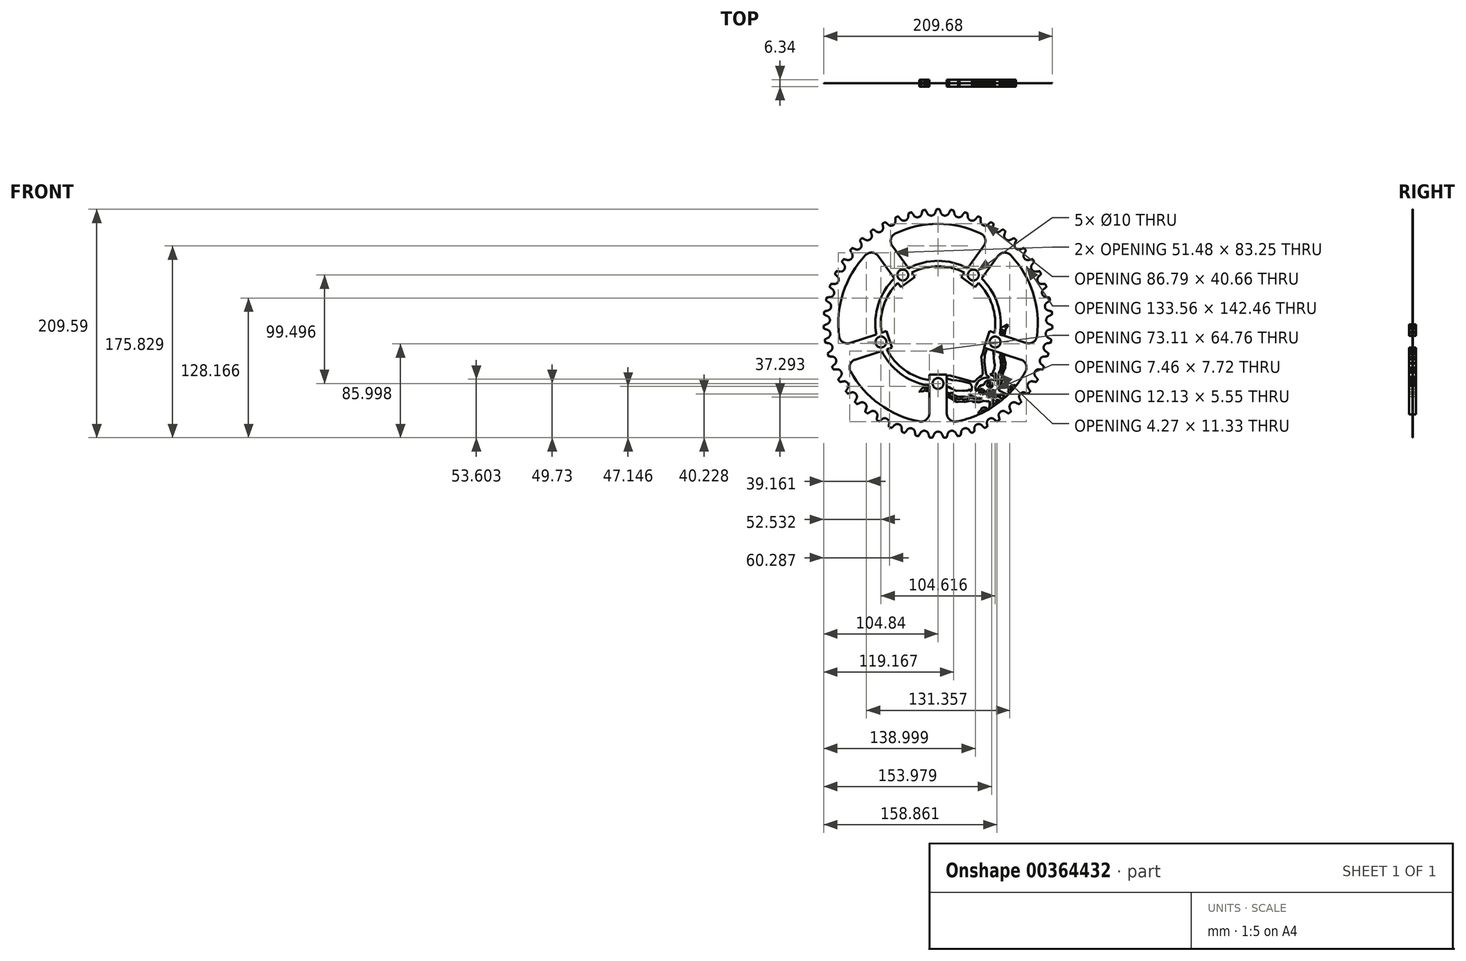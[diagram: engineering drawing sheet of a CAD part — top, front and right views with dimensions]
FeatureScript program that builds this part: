
annotation { "Feature Type Name" : "Feature", "Feature Type Description" : "" }
export const myFeature = defineFeature(function(context is Context, id is Id, definition is map)
    precondition{}
    {
        {
            var Q0;
            Q0=qCreatedBy(makeId("Front.planeOp"),FACE);
            var sketch = newSketch(context, id + "F0", { "sketchPlane" : qUnion([Q0])});
            skLineSegment(sketch, "E0", {"start": v(0, 0) * mm, "end": v(-6.35, 102.95) * mm, "construction": true});
            skLineSegment(sketch, "E1", {"start": v(0, 0) * mm, "end": v(6.35, 102.95) * mm, "construction": true});
            skArc(sketch, "E2", {"start": v(-6.1, 99) * mm, "mid": v(-3.93, 99.81) * mm, "end": v(-2.58, 101.71) * mm, "construction": true});
            skArc(sketch, "E3", {"start": v(-1.4, 104.85) * mm, "mid": v(-2, 103.3) * mm, "end": v(-2.55, 101.74) * mm});
            skLineSegment(sketch, "E4", {"start": v(-6.35, 102.95) * mm, "end": v(-2.58, 101.71) * mm, "construction": true});
            skCircle(sketch, "E5", {"center": v(0, 0) * mm, "radius": 103.19 * mm, "construction": true});
            skArc(sketch, "E6", {"start": v(1.4, 104.85) * mm, "mid": v(0, 104.86) * mm, "end": v(-1.4, 104.85) * mm});
            skLineSegment(sketch, "E7", {"start": v(0, 0) * mm, "end": v(0, 116.9) * mm, "construction": true});
            skArc(sketch, "E8", {"start": v(-6.1, 99) * mm, "mid": v(-3.9, 99.82) * mm, "end": v(-2.55, 101.74) * mm});
            skArc(sketch, "E9", {"start": v(2.58, 101.71) * mm, "mid": v(3.93, 99.81) * mm, "end": v(6.1, 99) * mm, "construction": true});
            skArc(sketch, "E10", {"start": v(2.55, 101.74) * mm, "mid": v(3.9, 99.82) * mm, "end": v(6.1, 99) * mm});
            skArc(sketch, "E11", {"start": v(2.56, 101.7) * mm, "mid": v(2, 103.29) * mm, "end": v(1.4, 104.85) * mm});
            skLineSegment(sketch, "E12", {"start": v(6.35, 102.95) * mm, "end": v(2.56, 101.7) * mm, "construction": true});
            skArc(sketch, "E13.1.0", {"start": v(-18.22, 97.5) * mm, "mid": v(-16.14, 98.58) * mm, "end": v(-15.03, 100.65) * mm});
            skArc(sketch, "E13.1.1", {"start": v(-14.27, 103.88) * mm, "mid": v(-14.68, 102.27) * mm, "end": v(-15.03, 100.65) * mm});
            skArc(sketch, "E13.1.2", {"start": v(-11.5, 104.22) * mm, "mid": v(-12.89, 104.06) * mm, "end": v(-14.27, 103.88) * mm});
            skArc(sketch, "E13.1.3", {"start": v(-9.96, 101.25) * mm, "mid": v(-10.7, 102.75) * mm, "end": v(-11.5, 104.22) * mm});
            skArc(sketch, "E13.1.4", {"start": v(-9.98, 101.28) * mm, "mid": v(-8.4, 99.54) * mm, "end": v(-6.1, 99) * mm});
            skArc(sketch, "E13.2.0", {"start": v(-30.07, 94.51) * mm, "mid": v(-28.13, 95.85) * mm, "end": v(-27.28, 98.04) * mm});
            skArc(sketch, "E13.2.1", {"start": v(-26.93, 101.34) * mm, "mid": v(-27.14, 99.7) * mm, "end": v(-27.28, 98.04) * mm});
            skArc(sketch, "E13.2.2", {"start": v(-24.22, 102.02) * mm, "mid": v(-25.58, 101.69) * mm, "end": v(-26.93, 101.34) * mm});
            skArc(sketch, "E13.2.3", {"start": v(-22.33, 99.26) * mm, "mid": v(-23.25, 100.66) * mm, "end": v(-24.22, 102.02) * mm});
            skArc(sketch, "E13.2.4", {"start": v(-22.35, 99.29) * mm, "mid": v(-20.56, 97.76) * mm, "end": v(-18.22, 97.5) * mm});
            skArc(sketch, "E13.3.0", {"start": v(-41.45, 90.1) * mm, "mid": v(-39.7, 91.67) * mm, "end": v(-39.13, 93.95) * mm});
            skArc(sketch, "E13.3.1", {"start": v(-39.18, 97.26) * mm, "mid": v(-39.18, 95.6) * mm, "end": v(-39.13, 93.95) * mm});
            skArc(sketch, "E13.3.2", {"start": v(-36.57, 98.27) * mm, "mid": v(-37.88, 97.78) * mm, "end": v(-39.18, 97.26) * mm});
            skArc(sketch, "E13.3.3", {"start": v(-34.36, 95.76) * mm, "mid": v(-35.44, 97.04) * mm, "end": v(-36.57, 98.27) * mm});
            skArc(sketch, "E13.3.4", {"start": v(-34.38, 95.79) * mm, "mid": v(-32.42, 94.49) * mm, "end": v(-30.07, 94.51) * mm});
            skArc(sketch, "E13.4.0", {"start": v(-52.21, 84.33) * mm, "mid": v(-50.66, 86.1) * mm, "end": v(-50.37, 88.43) * mm});
            skArc(sketch, "E13.4.1", {"start": v(-50.83, 91.71) * mm, "mid": v(-50.63, 90.06) * mm, "end": v(-50.37, 88.43) * mm});
            skArc(sketch, "E13.4.2", {"start": v(-48.37, 93.03) * mm, "mid": v(-49.6, 92.38) * mm, "end": v(-50.83, 91.71) * mm});
            skArc(sketch, "E13.4.3", {"start": v(-45.86, 90.81) * mm, "mid": v(-47.1, 91.94) * mm, "end": v(-48.37, 93.03) * mm});
            skArc(sketch, "E13.4.4", {"start": v(-45.89, 90.84) * mm, "mid": v(-43.78, 89.79) * mm, "end": v(-41.45, 90.1) * mm});
            skArc(sketch, "E13.5.0", {"start": v(-62.18, 77.27) * mm, "mid": v(-60.86, 79.22) * mm, "end": v(-60.86, 81.57) * mm});
            skArc(sketch, "E13.5.1", {"start": v(-61.72, 84.77) * mm, "mid": v(-61.32, 83.16) * mm, "end": v(-60.86, 81.57) * mm});
            skArc(sketch, "E13.5.2", {"start": v(-59.44, 86.38) * mm, "mid": v(-60.58, 85.58) * mm, "end": v(-61.72, 84.77) * mm});
            skArc(sketch, "E13.5.3", {"start": v(-56.68, 84.49) * mm, "mid": v(-58.04, 85.46) * mm, "end": v(-59.44, 86.38) * mm});
            skArc(sketch, "E13.5.4", {"start": v(-56.7, 84.5) * mm, "mid": v(-54.49, 83.73) * mm, "end": v(-52.21, 84.33) * mm});
            skArc(sketch, "E13.6.0", {"start": v(-71.2, 69.04) * mm, "mid": v(-70.13, 71.14) * mm, "end": v(-70.42, 73.47) * mm});
            skArc(sketch, "E13.6.1", {"start": v(-71.67, 76.54) * mm, "mid": v(-71.07, 75) * mm, "end": v(-70.42, 73.47) * mm});
            skArc(sketch, "E13.6.2", {"start": v(-69.6, 78.42) * mm, "mid": v(-70.64, 77.49) * mm, "end": v(-71.67, 76.54) * mm});
            skArc(sketch, "E13.6.3", {"start": v(-66.63, 76.88) * mm, "mid": v(-68.1, 77.68) * mm, "end": v(-69.6, 78.42) * mm});
            skArc(sketch, "E13.6.4", {"start": v(-66.66, 76.9) * mm, "mid": v(-64.36, 76.4) * mm, "end": v(-62.18, 77.27) * mm});
            skArc(sketch, "E13.7.0", {"start": v(-79.15, 59.77) * mm, "mid": v(-78.34, 61.98) * mm, "end": v(-78.92, 64.26) * mm});
            skArc(sketch, "E13.7.1", {"start": v(-80.53, 67.15) * mm, "mid": v(-79.75, 65.7) * mm, "end": v(-78.92, 64.26) * mm});
            skArc(sketch, "E13.7.2", {"start": v(-78.71, 69.28) * mm, "mid": v(-79.63, 68.22) * mm, "end": v(-80.53, 67.15) * mm});
            skArc(sketch, "E13.7.3", {"start": v(-75.57, 68.11) * mm, "mid": v(-77.13, 68.72) * mm, "end": v(-78.71, 69.28) * mm});
            skArc(sketch, "E13.7.4", {"start": v(-75.6, 68.13) * mm, "mid": v(-73.26, 67.9) * mm, "end": v(-71.2, 69.04) * mm});
            skArc(sketch, "E13.8.0", {"start": v(-85.9, 49.6) * mm, "mid": v(-85.37, 51.88) * mm, "end": v(-86.21, 54.07) * mm});
            skArc(sketch, "E13.8.1", {"start": v(-88.17, 56.75) * mm, "mid": v(-87.22, 55.4) * mm, "end": v(-86.21, 54.07) * mm});
            skArc(sketch, "E13.8.2", {"start": v(-86.63, 59.08) * mm, "mid": v(-87.4, 57.92) * mm, "end": v(-88.17, 56.75) * mm});
            skArc(sketch, "E13.8.3", {"start": v(-83.37, 58.3) * mm, "mid": v(-85, 58.72) * mm, "end": v(-86.63, 59.08) * mm});
            skArc(sketch, "E13.8.4", {"start": v(-83.4, 58.32) * mm, "mid": v(-81.05, 58.4) * mm, "end": v(-79.15, 59.77) * mm});
            skArc(sketch, "E13.9.0", {"start": v(-91.34, 38.66) * mm, "mid": v(-91.1, 41) * mm, "end": v(-92.2, 43.07) * mm});
            skArc(sketch, "E13.9.1", {"start": v(-94.48, 45.48) * mm, "mid": v(-93.36, 44.26) * mm, "end": v(-92.2, 43.07) * mm});
            skArc(sketch, "E13.9.2", {"start": v(-93.23, 47.99) * mm, "mid": v(-93.86, 46.74) * mm, "end": v(-94.48, 45.48) * mm});
            skArc(sketch, "E13.9.3", {"start": v(-89.9, 47.62) * mm, "mid": v(-91.56, 47.83) * mm, "end": v(-93.23, 47.99) * mm});
            skArc(sketch, "E13.9.4", {"start": v(-89.94, 47.63) * mm, "mid": v(-87.61, 47.99) * mm, "end": v(-85.9, 49.6) * mm});
            skArc(sketch, "E13.10.0", {"start": v(-95.4, 27.14) * mm, "mid": v(-95.44, 29.5) * mm, "end": v(-96.8, 31.41) * mm});
            skArc(sketch, "E13.10.1", {"start": v(-99.35, 33.53) * mm, "mid": v(-98.1, 32.45) * mm, "end": v(-96.8, 31.41) * mm});
            skArc(sketch, "E13.10.2", {"start": v(-98.42, 36.16) * mm, "mid": v(-98.9, 34.85) * mm, "end": v(-99.35, 33.53) * mm});
            skArc(sketch, "E13.10.3", {"start": v(-95.07, 36.21) * mm, "mid": v(-96.75, 36.22) * mm, "end": v(-98.42, 36.16) * mm});
            skArc(sketch, "E13.10.4", {"start": v(-95.1, 36.21) * mm, "mid": v(-92.85, 36.86) * mm, "end": v(-91.34, 38.66) * mm});
            skArc(sketch, "E13.11.0", {"start": v(-98, 15.21) * mm, "mid": v(-98.34, 17.54) * mm, "end": v(-99.93, 19.28) * mm});
            skArc(sketch, "E13.11.1", {"start": v(-102.72, 21.07) * mm, "mid": v(-101.34, 20.15) * mm, "end": v(-99.93, 19.28) * mm});
            skArc(sketch, "E13.11.2", {"start": v(-102.12, 23.8) * mm, "mid": v(-102.43, 22.43) * mm, "end": v(-102.72, 21.07) * mm});
            skArc(sketch, "E13.11.3", {"start": v(-98.8, 24.26) * mm, "mid": v(-100.47, 24.05) * mm, "end": v(-102.12, 23.8) * mm});
            skArc(sketch, "E13.11.4", {"start": v(-98.84, 24.25) * mm, "mid": v(-96.67, 25.17) * mm, "end": v(-95.4, 27.14) * mm});
            skArc(sketch, "E13.12.0", {"start": v(-99.13, 3.05) * mm, "mid": v(-99.75, 5.32) * mm, "end": v(-101.54, 6.85) * mm});
            skArc(sketch, "E13.12.1", {"start": v(-104.53, 8.28) * mm, "mid": v(-103.05, 7.54) * mm, "end": v(-101.54, 6.85) * mm});
            skArc(sketch, "E13.12.2", {"start": v(-104.27, 11.07) * mm, "mid": v(-104.4, 9.67) * mm, "end": v(-104.53, 8.28) * mm});
            skArc(sketch, "E13.12.3", {"start": v(-101.03, 11.93) * mm, "mid": v(-102.66, 11.53) * mm, "end": v(-104.27, 11.07) * mm});
            skArc(sketch, "E13.12.4", {"start": v(-101.07, 11.92) * mm, "mid": v(-99.03, 13.1) * mm, "end": v(-98, 15.21) * mm});
            skArc(sketch, "E13.13.0", {"start": v(-98.76, -9.15) * mm, "mid": v(-99.65, -6.98) * mm, "end": v(-101.61, -5.68) * mm});
            skArc(sketch, "E13.13.1", {"start": v(-104.75, -4.63) * mm, "mid": v(-103.2, -5.18) * mm, "end": v(-101.61, -5.68) * mm});
            skArc(sketch, "E13.13.2", {"start": v(-104.84, -1.83) * mm, "mid": v(-104.8, -3.23) * mm, "end": v(-104.75, -4.63) * mm});
            skArc(sketch, "E13.13.3", {"start": v(-101.74, -0.58) * mm, "mid": v(-103.3, -1.18) * mm, "end": v(-104.84, -1.83) * mm});
            skArc(sketch, "E13.13.4", {"start": v(-101.77, -0.59) * mm, "mid": v(-99.9, 0.83) * mm, "end": v(-99.13, 3.05) * mm});
            skArc(sketch, "E13.14.0", {"start": v(-96.88, -21.22) * mm, "mid": v(-98.04, -19.17) * mm, "end": v(-100.14, -18.12) * mm});
            skArc(sketch, "E13.14.1", {"start": v(-103.4, -17.46) * mm, "mid": v(-101.77, -17.82) * mm, "end": v(-100.14, -18.12) * mm});
            skArc(sketch, "E13.14.2", {"start": v(-103.82, -14.7) * mm, "mid": v(-103.62, -16.08) * mm, "end": v(-103.4, -17.46) * mm});
            skArc(sketch, "E13.14.3", {"start": v(-100.9, -13.07) * mm, "mid": v(-102.37, -13.86) * mm, "end": v(-103.82, -14.7) * mm});
            skArc(sketch, "E13.14.4", {"start": v(-100.92, -13.09) * mm, "mid": v(-99.24, -11.45) * mm, "end": v(-98.76, -9.15) * mm});
            skArc(sketch, "E13.15.0", {"start": v(-93.54, -32.96) * mm, "mid": v(-94.94, -31.07) * mm, "end": v(-97.16, -30.3) * mm});
            skArc(sketch, "E13.15.1", {"start": v(-100.46, -30.04) * mm, "mid": v(-98.81, -30.2) * mm, "end": v(-97.16, -30.3) * mm});
            skArc(sketch, "E13.15.2", {"start": v(-101.23, -27.35) * mm, "mid": v(-100.85, -28.7) * mm, "end": v(-100.46, -30.04) * mm});
            skArc(sketch, "E13.15.3", {"start": v(-98.52, -25.37) * mm, "mid": v(-99.9, -26.34) * mm, "end": v(-101.23, -27.35) * mm});
            skArc(sketch, "E13.15.4", {"start": v(-98.55, -25.4) * mm, "mid": v(-97.08, -23.56) * mm, "end": v(-96.88, -21.22) * mm});
            skArc(sketch, "E13.16.0", {"start": v(-88.78, -44.2) * mm, "mid": v(-90.4, -42.5) * mm, "end": v(-92.7, -42) * mm});
            skArc(sketch, "E13.16.1", {"start": v(-96, -42.15) * mm, "mid": v(-94.35, -42.1) * mm, "end": v(-92.7, -42) * mm});
            skArc(sketch, "E13.16.2", {"start": v(-97.1, -39.58) * mm, "mid": v(-96.56, -40.87) * mm, "end": v(-96, -42.15) * mm});
            skArc(sketch, "E13.16.3", {"start": v(-94.66, -37.29) * mm, "mid": v(-95.9, -38.41) * mm, "end": v(-97.1, -39.58) * mm});
            skArc(sketch, "E13.16.4", {"start": v(-94.68, -37.31) * mm, "mid": v(-93.45, -35.31) * mm, "end": v(-93.54, -32.96) * mm});
            skArc(sketch, "E13.17.0", {"start": v(-82.68, -54.78) * mm, "mid": v(-84.5, -53.3) * mm, "end": v(-86.83, -53.07) * mm});
            skArc(sketch, "E13.17.1", {"start": v(-90.1, -53.63) * mm, "mid": v(-88.46, -53.38) * mm, "end": v(-86.83, -53.07) * mm});
            skArc(sketch, "E13.17.2", {"start": v(-91.5, -51.21) * mm, "mid": v(-90.8, -52.43) * mm, "end": v(-90.1, -53.63) * mm});
            skArc(sketch, "E13.17.3", {"start": v(-89.36, -48.64) * mm, "mid": v(-90.45, -49.9) * mm, "end": v(-91.5, -51.21) * mm});
            skArc(sketch, "E13.17.4", {"start": v(-89.38, -48.66) * mm, "mid": v(-88.4, -46.53) * mm, "end": v(-88.78, -44.2) * mm});
            skArc(sketch, "E13.18.0", {"start": v(-75.32, -64.53) * mm, "mid": v(-77.3, -63.27) * mm, "end": v(-79.65, -63.34) * mm});
            skArc(sketch, "E13.18.1", {"start": v(-82.83, -64.3) * mm, "mid": v(-81.23, -63.85) * mm, "end": v(-79.65, -63.34) * mm});
            skArc(sketch, "E13.18.2", {"start": v(-84.51, -62.07) * mm, "mid": v(-83.68, -63.2) * mm, "end": v(-82.83, -64.3) * mm});
            skArc(sketch, "E13.18.3", {"start": v(-82.7, -59.25) * mm, "mid": v(-83.63, -60.64) * mm, "end": v(-84.51, -62.07) * mm});
            skArc(sketch, "E13.18.4", {"start": v(-82.72, -59.28) * mm, "mid": v(-82.01, -57.04) * mm, "end": v(-82.68, -54.78) * mm});
            skArc(sketch, "E13.19.0", {"start": v(-66.82, -73.3) * mm, "mid": v(-68.94, -72.3) * mm, "end": v(-71.27, -72.65) * mm});
            skArc(sketch, "E13.19.1", {"start": v(-74.3, -74) * mm, "mid": v(-72.77, -73.35) * mm, "end": v(-71.27, -72.65) * mm});
            skArc(sketch, "E13.19.2", {"start": v(-76.24, -71.98) * mm, "mid": v(-75.28, -73) * mm, "end": v(-74.3, -74) * mm});
            skArc(sketch, "E13.19.3", {"start": v(-74.8, -68.96) * mm, "mid": v(-75.55, -70.46) * mm, "end": v(-76.24, -71.98) * mm});
            skArc(sketch, "E13.19.4", {"start": v(-74.81, -69) * mm, "mid": v(-74.38, -66.68) * mm, "end": v(-75.32, -64.53) * mm});
            skArc(sketch, "E13.20.0", {"start": v(-57.3, -80.95) * mm, "mid": v(-59.54, -80.22) * mm, "end": v(-61.8, -80.86) * mm});
            skArc(sketch, "E13.20.1", {"start": v(-64.64, -82.56) * mm, "mid": v(-63.2, -81.73) * mm, "end": v(-61.8, -80.86) * mm});
            skArc(sketch, "E13.20.2", {"start": v(-66.82, -80.8) * mm, "mid": v(-65.74, -81.7) * mm, "end": v(-64.64, -82.56) * mm});
            skArc(sketch, "E13.20.3", {"start": v(-65.75, -77.63) * mm, "mid": v(-66.31, -79.21) * mm, "end": v(-66.82, -80.8) * mm});
            skArc(sketch, "E13.20.4", {"start": v(-65.76, -77.66) * mm, "mid": v(-65.62, -75.32) * mm, "end": v(-66.82, -73.3) * mm});
            skArc(sketch, "E13.21.0", {"start": v(-46.92, -87.38) * mm, "mid": v(-49.23, -86.92) * mm, "end": v(-51.4, -87.84) * mm});
            skArc(sketch, "E13.21.1", {"start": v(-54, -89.88) * mm, "mid": v(-52.68, -88.88) * mm, "end": v(-51.4, -87.84) * mm});
            skArc(sketch, "E13.21.2", {"start": v(-56.38, -88.4) * mm, "mid": v(-55.2, -89.15) * mm, "end": v(-54, -89.88) * mm});
            skArc(sketch, "E13.21.3", {"start": v(-55.71, -85.12) * mm, "mid": v(-56.08, -86.76) * mm, "end": v(-56.38, -88.4) * mm});
            skArc(sketch, "E13.21.4", {"start": v(-55.72, -85.16) * mm, "mid": v(-55.87, -82.81) * mm, "end": v(-57.3, -80.95) * mm});
            skArc(sketch, "E13.22.0", {"start": v(-35.83, -92.48) * mm, "mid": v(-38.17, -92.31) * mm, "end": v(-40.2, -93.49) * mm});
            skArc(sketch, "E13.22.1", {"start": v(-42.55, -95.83) * mm, "mid": v(-41.36, -94.68) * mm, "end": v(-40.2, -93.49) * mm});
            skArc(sketch, "E13.22.2", {"start": v(-45.1, -94.67) * mm, "mid": v(-43.83, -95.26) * mm, "end": v(-42.55, -95.83) * mm});
            skArc(sketch, "E13.22.3", {"start": v(-44.83, -91.33) * mm, "mid": v(-45, -93) * mm, "end": v(-45.1, -94.67) * mm});
            skArc(sketch, "E13.22.4", {"start": v(-44.84, -91.36) * mm, "mid": v(-45.27, -89.05) * mm, "end": v(-46.92, -87.38) * mm});
            skArc(sketch, "E13.23.0", {"start": v(-24.2, -96.19) * mm, "mid": v(-26.54, -96.3) * mm, "end": v(-28.42, -97.72) * mm});
            skArc(sketch, "E13.23.1", {"start": v(-30.45, -100.34) * mm, "mid": v(-29.41, -99.05) * mm, "end": v(-28.42, -97.72) * mm});
            skArc(sketch, "E13.23.2", {"start": v(-33.12, -99.49) * mm, "mid": v(-31.79, -99.92) * mm, "end": v(-30.45, -100.34) * mm});
            skArc(sketch, "E13.23.3", {"start": v(-33.27, -96.14) * mm, "mid": v(-33.22, -97.82) * mm, "end": v(-33.12, -99.49) * mm});
            skArc(sketch, "E13.23.4", {"start": v(-33.27, -96.18) * mm, "mid": v(-33.98, -93.94) * mm, "end": v(-35.83, -92.48) * mm});
            skArc(sketch, "E13.24.0", {"start": v(-12.19, -98.43) * mm, "mid": v(-14.5, -98.84) * mm, "end": v(-16.2, -100.47) * mm});
            skArc(sketch, "E13.24.1", {"start": v(-17.9, -103.32) * mm, "mid": v(-17.02, -101.91) * mm, "end": v(-16.2, -100.47) * mm});
            skArc(sketch, "E13.24.2", {"start": v(-20.64, -102.8) * mm, "mid": v(-19.27, -103.07) * mm, "end": v(-17.9, -103.32) * mm});
            skArc(sketch, "E13.24.3", {"start": v(-21.2, -99.5) * mm, "mid": v(-20.95, -101.16) * mm, "end": v(-20.64, -102.8) * mm});
            skArc(sketch, "E13.24.4", {"start": v(-21.2, -99.54) * mm, "mid": v(-22.18, -97.4) * mm, "end": v(-24.2, -96.19) * mm});
            skArc(sketch, "E13.25.0", {"start": v(0, -99.18) * mm, "mid": v(-2.25, -99.87) * mm, "end": v(-3.72, -101.7) * mm});
            skArc(sketch, "E13.25.1", {"start": v(-5.06, -104.73) * mm, "mid": v(-4.36, -103.23) * mm, "end": v(-3.72, -101.7) * mm});
            skArc(sketch, "E13.25.2", {"start": v(-7.85, -104.56) * mm, "mid": v(-6.46, -104.66) * mm, "end": v(-5.06, -104.73) * mm});
            skArc(sketch, "E13.25.3", {"start": v(-8.81, -101.35) * mm, "mid": v(-8.36, -102.97) * mm, "end": v(-7.85, -104.56) * mm});
            skArc(sketch, "E13.25.4", {"start": v(-8.8, -101.39) * mm, "mid": v(-10.04, -99.39) * mm, "end": v(-12.19, -98.43) * mm});
            skArc(sketch, "E13.26.0", {"start": v(12.19, -98.43) * mm, "mid": v(10.04, -99.39) * mm, "end": v(8.8, -101.39) * mm});
            skArc(sketch, "E13.26.1", {"start": v(7.85, -104.56) * mm, "mid": v(8.35, -102.98) * mm, "end": v(8.8, -101.39) * mm});
            skArc(sketch, "E13.26.2", {"start": v(5.06, -104.73) * mm, "mid": v(6.46, -104.66) * mm, "end": v(7.85, -104.56) * mm});
            skArc(sketch, "E13.26.3", {"start": v(3.7, -101.67) * mm, "mid": v(4.36, -103.21) * mm, "end": v(5.06, -104.73) * mm});
            skArc(sketch, "E13.26.4", {"start": v(3.72, -101.7) * mm, "mid": v(2.25, -99.87) * mm, "end": v(0, -99.18) * mm});
            skArc(sketch, "E13.27.0", {"start": v(24.2, -96.19) * mm, "mid": v(22.18, -97.4) * mm, "end": v(21.2, -99.54) * mm});
            skArc(sketch, "E13.27.1", {"start": v(20.64, -102.8) * mm, "mid": v(20.95, -101.18) * mm, "end": v(21.2, -99.54) * mm});
            skArc(sketch, "E13.27.2", {"start": v(17.9, -103.32) * mm, "mid": v(19.27, -103.07) * mm, "end": v(20.64, -102.8) * mm});
            skArc(sketch, "E13.27.3", {"start": v(16.17, -100.44) * mm, "mid": v(17, -101.9) * mm, "end": v(17.9, -103.32) * mm});
            skArc(sketch, "E13.27.4", {"start": v(16.2, -100.47) * mm, "mid": v(14.5, -98.84) * mm, "end": v(12.19, -98.43) * mm});
            skArc(sketch, "E13.28.0", {"start": v(35.83, -92.48) * mm, "mid": v(33.98, -93.94) * mm, "end": v(33.27, -96.18) * mm});
            skArc(sketch, "E13.28.1", {"start": v(33.12, -99.49) * mm, "mid": v(33.22, -97.83) * mm, "end": v(33.27, -96.18) * mm});
            skArc(sketch, "E13.28.2", {"start": v(30.45, -100.34) * mm, "mid": v(31.79, -99.92) * mm, "end": v(33.12, -99.49) * mm});
            skArc(sketch, "E13.28.3", {"start": v(28.4, -97.7) * mm, "mid": v(29.4, -99.03) * mm, "end": v(30.45, -100.34) * mm});
            skArc(sketch, "E13.28.4", {"start": v(28.42, -97.72) * mm, "mid": v(26.54, -96.3) * mm, "end": v(24.2, -96.19) * mm});
            skArc(sketch, "E13.29.0", {"start": v(46.92, -87.38) * mm, "mid": v(45.27, -89.05) * mm, "end": v(44.84, -91.36) * mm});
            skArc(sketch, "E13.29.1", {"start": v(45.1, -94.67) * mm, "mid": v(45, -93.01) * mm, "end": v(44.84, -91.36) * mm});
            skArc(sketch, "E13.29.2", {"start": v(42.55, -95.83) * mm, "mid": v(43.83, -95.26) * mm, "end": v(45.1, -94.67) * mm});
            skArc(sketch, "E13.29.3", {"start": v(40.19, -93.46) * mm, "mid": v(41.35, -94.67) * mm, "end": v(42.55, -95.83) * mm});
            skArc(sketch, "E13.29.4", {"start": v(40.2, -93.49) * mm, "mid": v(38.17, -92.31) * mm, "end": v(35.83, -92.48) * mm});
            skArc(sketch, "E13.30.0", {"start": v(57.3, -80.95) * mm, "mid": v(55.87, -82.81) * mm, "end": v(55.72, -85.16) * mm});
            skArc(sketch, "E13.30.1", {"start": v(56.38, -88.4) * mm, "mid": v(56.08, -86.78) * mm, "end": v(55.72, -85.16) * mm});
            skArc(sketch, "E13.30.2", {"start": v(54, -89.88) * mm, "mid": v(55.2, -89.15) * mm, "end": v(56.38, -88.4) * mm});
            skArc(sketch, "E13.30.3", {"start": v(51.37, -87.82) * mm, "mid": v(52.67, -88.87) * mm, "end": v(54, -89.88) * mm});
            skArc(sketch, "E13.30.4", {"start": v(51.4, -87.84) * mm, "mid": v(49.23, -86.92) * mm, "end": v(46.92, -87.38) * mm});
            skArc(sketch, "E13.31.0", {"start": v(66.82, -73.3) * mm, "mid": v(65.62, -75.32) * mm, "end": v(65.76, -77.66) * mm});
            skArc(sketch, "E13.31.1", {"start": v(66.82, -80.8) * mm, "mid": v(66.32, -79.23) * mm, "end": v(65.76, -77.66) * mm});
            skArc(sketch, "E13.31.2", {"start": v(64.64, -82.56) * mm, "mid": v(65.74, -81.7) * mm, "end": v(66.82, -80.8) * mm});
            skArc(sketch, "E13.31.3", {"start": v(61.77, -80.84) * mm, "mid": v(63.2, -81.72) * mm, "end": v(64.64, -82.56) * mm});
            skArc(sketch, "E13.31.4", {"start": v(61.8, -80.86) * mm, "mid": v(59.54, -80.22) * mm, "end": v(57.3, -80.95) * mm});
            skArc(sketch, "E13.32.0", {"start": v(75.32, -64.53) * mm, "mid": v(74.38, -66.68) * mm, "end": v(74.81, -69) * mm});
            skArc(sketch, "E13.32.1", {"start": v(76.24, -71.98) * mm, "mid": v(75.55, -70.48) * mm, "end": v(74.81, -69) * mm});
            skArc(sketch, "E13.32.2", {"start": v(74.3, -74) * mm, "mid": v(75.28, -73) * mm, "end": v(76.24, -71.98) * mm});
            skArc(sketch, "E13.32.3", {"start": v(71.23, -72.64) * mm, "mid": v(72.75, -73.34) * mm, "end": v(74.3, -74) * mm});
            skArc(sketch, "E13.32.4", {"start": v(71.27, -72.65) * mm, "mid": v(68.94, -72.3) * mm, "end": v(66.82, -73.3) * mm});
            skArc(sketch, "E13.33.0", {"start": v(82.68, -54.78) * mm, "mid": v(82.01, -57.04) * mm, "end": v(82.72, -59.28) * mm});
            skArc(sketch, "E13.33.1", {"start": v(84.51, -62.07) * mm, "mid": v(83.64, -60.66) * mm, "end": v(82.72, -59.28) * mm});
            skArc(sketch, "E13.33.2", {"start": v(82.83, -64.3) * mm, "mid": v(83.68, -63.2) * mm, "end": v(84.51, -62.07) * mm});
            skArc(sketch, "E13.33.3", {"start": v(79.62, -63.33) * mm, "mid": v(81.22, -63.84) * mm, "end": v(82.83, -64.3) * mm});
            skArc(sketch, "E13.33.4", {"start": v(79.65, -63.34) * mm, "mid": v(77.3, -63.27) * mm, "end": v(75.32, -64.53) * mm});
            skArc(sketch, "E13.34.0", {"start": v(88.78, -44.2) * mm, "mid": v(88.4, -46.53) * mm, "end": v(89.38, -48.66) * mm});
            skArc(sketch, "E13.34.1", {"start": v(91.5, -51.21) * mm, "mid": v(90.46, -49.92) * mm, "end": v(89.38, -48.66) * mm});
            skArc(sketch, "E13.34.2", {"start": v(90.1, -53.63) * mm, "mid": v(90.8, -52.43) * mm, "end": v(91.5, -51.21) * mm});
            skArc(sketch, "E13.34.3", {"start": v(86.8, -53.07) * mm, "mid": v(88.45, -53.38) * mm, "end": v(90.1, -53.63) * mm});
            skArc(sketch, "E13.34.4", {"start": v(86.83, -53.07) * mm, "mid": v(84.5, -53.3) * mm, "end": v(82.68, -54.78) * mm});
            skArc(sketch, "E13.35.0", {"start": v(93.54, -32.96) * mm, "mid": v(93.45, -35.31) * mm, "end": v(94.68, -37.31) * mm});
            skArc(sketch, "E13.35.1", {"start": v(97.1, -39.58) * mm, "mid": v(95.91, -38.42) * mm, "end": v(94.68, -37.31) * mm});
            skArc(sketch, "E13.35.2", {"start": v(96, -42.15) * mm, "mid": v(96.56, -40.87) * mm, "end": v(97.1, -39.58) * mm});
            skArc(sketch, "E13.35.3", {"start": v(92.66, -42) * mm, "mid": v(94.34, -42.1) * mm, "end": v(96, -42.15) * mm});
            skArc(sketch, "E13.35.4", {"start": v(92.7, -42) * mm, "mid": v(90.4, -42.5) * mm, "end": v(88.78, -44.2) * mm});
            skArc(sketch, "E13.36.0", {"start": v(96.88, -21.22) * mm, "mid": v(97.08, -23.56) * mm, "end": v(98.55, -25.4) * mm});
            skArc(sketch, "E13.36.1", {"start": v(101.23, -27.35) * mm, "mid": v(99.9, -26.35) * mm, "end": v(98.55, -25.4) * mm});
            skArc(sketch, "E13.36.2", {"start": v(100.46, -30.04) * mm, "mid": v(100.85, -28.7) * mm, "end": v(101.23, -27.35) * mm});
            skArc(sketch, "E13.36.3", {"start": v(97.12, -30.3) * mm, "mid": v(98.8, -30.2) * mm, "end": v(100.46, -30.04) * mm});
            skArc(sketch, "E13.36.4", {"start": v(97.16, -30.3) * mm, "mid": v(94.94, -31.07) * mm, "end": v(93.54, -32.96) * mm});
            skArc(sketch, "E13.37.0", {"start": v(98.76, -9.15) * mm, "mid": v(99.24, -11.45) * mm, "end": v(100.92, -13.09) * mm});
            skArc(sketch, "E13.37.1", {"start": v(103.82, -14.7) * mm, "mid": v(102.39, -13.87) * mm, "end": v(100.92, -13.09) * mm});
            skArc(sketch, "E13.37.2", {"start": v(103.4, -17.46) * mm, "mid": v(103.62, -16.08) * mm, "end": v(103.82, -14.7) * mm});
            skArc(sketch, "E13.37.3", {"start": v(100.1, -18.13) * mm, "mid": v(101.76, -17.82) * mm, "end": v(103.4, -17.46) * mm});
            skArc(sketch, "E13.37.4", {"start": v(100.14, -18.12) * mm, "mid": v(98.04, -19.17) * mm, "end": v(96.88, -21.22) * mm});
            skArc(sketch, "E13.38.0", {"start": v(99.13, 3.05) * mm, "mid": v(99.9, 0.83) * mm, "end": v(101.77, -0.59) * mm});
            skArc(sketch, "E13.38.1", {"start": v(104.84, -1.83) * mm, "mid": v(103.31, -1.18) * mm, "end": v(101.77, -0.59) * mm});
            skArc(sketch, "E13.38.2", {"start": v(104.75, -4.63) * mm, "mid": v(104.8, -3.23) * mm, "end": v(104.84, -1.83) * mm});
            skArc(sketch, "E13.38.3", {"start": v(101.58, -5.69) * mm, "mid": v(103.18, -5.18) * mm, "end": v(104.75, -4.63) * mm});
            skArc(sketch, "E13.38.4", {"start": v(101.61, -5.68) * mm, "mid": v(99.65, -6.98) * mm, "end": v(98.76, -9.15) * mm});
            skArc(sketch, "E13.39.0", {"start": v(98, 15.21) * mm, "mid": v(99.03, 13.1) * mm, "end": v(101.07, 11.92) * mm});
            skArc(sketch, "E13.39.1", {"start": v(104.27, 11.07) * mm, "mid": v(102.68, 11.52) * mm, "end": v(101.07, 11.92) * mm});
            skArc(sketch, "E13.39.2", {"start": v(104.53, 8.28) * mm, "mid": v(104.4, 9.67) * mm, "end": v(104.27, 11.07) * mm});
            skArc(sketch, "E13.39.3", {"start": v(101.5, 6.84) * mm, "mid": v(103.03, 7.53) * mm, "end": v(104.53, 8.28) * mm});
            skArc(sketch, "E13.39.4", {"start": v(101.54, 6.85) * mm, "mid": v(99.75, 5.32) * mm, "end": v(99.13, 3.05) * mm});
            skArc(sketch, "E13.40.0", {"start": v(95.4, 27.14) * mm, "mid": v(96.67, 25.17) * mm, "end": v(98.84, 24.25) * mm});
            skArc(sketch, "E13.40.1", {"start": v(102.12, 23.8) * mm, "mid": v(100.48, 24.05) * mm, "end": v(98.84, 24.25) * mm});
            skArc(sketch, "E13.40.2", {"start": v(102.72, 21.07) * mm, "mid": v(102.43, 22.43) * mm, "end": v(102.12, 23.8) * mm});
            skArc(sketch, "E13.40.3", {"start": v(99.9, 19.26) * mm, "mid": v(101.32, 20.14) * mm, "end": v(102.72, 21.07) * mm});
            skArc(sketch, "E13.40.4", {"start": v(99.93, 19.28) * mm, "mid": v(98.34, 17.54) * mm, "end": v(98, 15.21) * mm});
            skArc(sketch, "E13.41.0", {"start": v(91.34, 38.66) * mm, "mid": v(92.85, 36.86) * mm, "end": v(95.1, 36.21) * mm});
            skArc(sketch, "E13.41.1", {"start": v(98.42, 36.16) * mm, "mid": v(96.77, 36.22) * mm, "end": v(95.1, 36.21) * mm});
            skArc(sketch, "E13.41.2", {"start": v(99.35, 33.53) * mm, "mid": v(98.9, 34.85) * mm, "end": v(98.42, 36.16) * mm});
            skArc(sketch, "E13.41.3", {"start": v(96.77, 31.4) * mm, "mid": v(98.08, 32.44) * mm, "end": v(99.35, 33.53) * mm});
            skArc(sketch, "E13.41.4", {"start": v(96.8, 31.41) * mm, "mid": v(95.44, 29.5) * mm, "end": v(95.4, 27.14) * mm});
            skArc(sketch, "E13.42.0", {"start": v(85.9, 49.6) * mm, "mid": v(87.61, 47.99) * mm, "end": v(89.94, 47.63) * mm});
            skArc(sketch, "E13.42.1", {"start": v(93.23, 47.99) * mm, "mid": v(91.58, 47.83) * mm, "end": v(89.94, 47.63) * mm});
            skArc(sketch, "E13.42.2", {"start": v(94.48, 45.48) * mm, "mid": v(93.86, 46.74) * mm, "end": v(93.23, 47.99) * mm});
            skArc(sketch, "E13.42.3", {"start": v(92.18, 43.04) * mm, "mid": v(93.35, 44.24) * mm, "end": v(94.48, 45.48) * mm});
            skArc(sketch, "E13.42.4", {"start": v(92.2, 43.07) * mm, "mid": v(91.1, 41) * mm, "end": v(91.34, 38.66) * mm});
            skArc(sketch, "E13.43.0", {"start": v(79.15, 59.77) * mm, "mid": v(81.05, 58.4) * mm, "end": v(83.4, 58.32) * mm});
            skArc(sketch, "E13.43.1", {"start": v(86.63, 59.08) * mm, "mid": v(85, 58.73) * mm, "end": v(83.4, 58.32) * mm});
            skArc(sketch, "E13.43.2", {"start": v(88.17, 56.75) * mm, "mid": v(87.4, 57.92) * mm, "end": v(86.63, 59.08) * mm});
            skArc(sketch, "E13.43.3", {"start": v(86.2, 54.05) * mm, "mid": v(87.2, 55.38) * mm, "end": v(88.17, 56.75) * mm});
            skArc(sketch, "E13.43.4", {"start": v(86.21, 54.07) * mm, "mid": v(85.37, 51.88) * mm, "end": v(85.9, 49.6) * mm});
            skArc(sketch, "E14.2.44.0", {"start": v(71.2, 69.04) * mm, "mid": v(73.26, 67.9) * mm, "end": v(75.6, 68.13) * mm});
            skArc(sketch, "E14.4.44.0", {"start": v(78.71, 69.28) * mm, "mid": v(77.15, 68.73) * mm, "end": v(75.6, 68.13) * mm});
            skArc(sketch, "E14.8.44.0", {"start": v(80.53, 67.15) * mm, "mid": v(79.63, 68.22) * mm, "end": v(78.71, 69.28) * mm});
            skArc(sketch, "E14.12.44.0", {"start": v(78.9, 64.23) * mm, "mid": v(79.74, 65.68) * mm, "end": v(80.53, 67.15) * mm});
            skArc(sketch, "E14.16.44.0", {"start": v(78.92, 64.26) * mm, "mid": v(78.34, 61.98) * mm, "end": v(79.15, 59.77) * mm});
            skArc(sketch, "E14.2.45.0", {"start": v(62.18, 77.27) * mm, "mid": v(64.36, 76.4) * mm, "end": v(66.66, 76.9) * mm});
            skArc(sketch, "E14.4.45.0", {"start": v(69.6, 78.42) * mm, "mid": v(68.12, 77.69) * mm, "end": v(66.66, 76.9) * mm});
            skArc(sketch, "E14.8.45.0", {"start": v(71.67, 76.54) * mm, "mid": v(70.64, 77.49) * mm, "end": v(69.6, 78.42) * mm});
            skArc(sketch, "E14.12.45.0", {"start": v(70.4, 73.44) * mm, "mid": v(71.06, 74.98) * mm, "end": v(71.67, 76.54) * mm});
            skArc(sketch, "E14.16.45.0", {"start": v(70.42, 73.47) * mm, "mid": v(70.13, 71.14) * mm, "end": v(71.2, 69.04) * mm});
            skArc(sketch, "E14.2.46.0", {"start": v(52.21, 84.33) * mm, "mid": v(54.49, 83.73) * mm, "end": v(56.7, 84.5) * mm});
            skArc(sketch, "E14.4.46.0", {"start": v(59.44, 86.38) * mm, "mid": v(58.05, 85.47) * mm, "end": v(56.7, 84.5) * mm});
            skArc(sketch, "E14.8.46.0", {"start": v(61.72, 84.77) * mm, "mid": v(60.58, 85.58) * mm, "end": v(59.44, 86.38) * mm});
            skArc(sketch, "E14.12.46.0", {"start": v(60.85, 81.53) * mm, "mid": v(61.31, 83.14) * mm, "end": v(61.72, 84.77) * mm});
            skArc(sketch, "E14.16.46.0", {"start": v(60.86, 81.57) * mm, "mid": v(60.86, 79.22) * mm, "end": v(62.18, 77.27) * mm});
            skArc(sketch, "E14.2.47.0", {"start": v(41.45, 90.1) * mm, "mid": v(43.78, 89.79) * mm, "end": v(45.89, 90.84) * mm});
            skArc(sketch, "E14.4.47.0", {"start": v(48.37, 93.03) * mm, "mid": v(47.11, 91.96) * mm, "end": v(45.89, 90.84) * mm});
            skArc(sketch, "E14.8.47.0", {"start": v(50.83, 91.71) * mm, "mid": v(49.6, 92.38) * mm, "end": v(48.37, 93.03) * mm});
            skArc(sketch, "E14.12.47.0", {"start": v(50.37, 88.4) * mm, "mid": v(50.63, 90.05) * mm, "end": v(50.83, 91.71) * mm});
            skArc(sketch, "E14.16.47.0", {"start": v(50.37, 88.43) * mm, "mid": v(50.66, 86.1) * mm, "end": v(52.21, 84.33) * mm});
            skArc(sketch, "E14.2.48.0", {"start": v(30.07, 94.51) * mm, "mid": v(32.42, 94.49) * mm, "end": v(34.38, 95.79) * mm});
            skArc(sketch, "E14.4.48.0", {"start": v(36.57, 98.27) * mm, "mid": v(35.45, 97.05) * mm, "end": v(34.38, 95.79) * mm});
            skArc(sketch, "E14.8.48.0", {"start": v(39.18, 97.26) * mm, "mid": v(37.88, 97.78) * mm, "end": v(36.57, 98.27) * mm});
            skArc(sketch, "E14.12.48.0", {"start": v(39.12, 93.91) * mm, "mid": v(39.18, 95.59) * mm, "end": v(39.18, 97.26) * mm});
            skArc(sketch, "E14.16.48.0", {"start": v(39.13, 93.95) * mm, "mid": v(39.7, 91.67) * mm, "end": v(41.45, 90.1) * mm});
            skArc(sketch, "E14.2.49.0", {"start": v(18.22, 97.5) * mm, "mid": v(20.56, 97.76) * mm, "end": v(22.35, 99.29) * mm});
            skArc(sketch, "E14.4.49.0", {"start": v(24.22, 102.02) * mm, "mid": v(23.26, 100.67) * mm, "end": v(22.35, 99.29) * mm});
            skArc(sketch, "E14.8.49.0", {"start": v(26.93, 101.34) * mm, "mid": v(25.58, 101.69) * mm, "end": v(24.22, 102.02) * mm});
            skArc(sketch, "E14.12.49.0", {"start": v(27.29, 98) * mm, "mid": v(27.14, 99.68) * mm, "end": v(26.93, 101.34) * mm});
            skArc(sketch, "E14.16.49.0", {"start": v(27.28, 98.04) * mm, "mid": v(28.13, 95.85) * mm, "end": v(30.07, 94.51) * mm});
            skArc(sketch, "E14.2.50.0", {"start": v(6.1, 99) * mm, "mid": v(8.4, 99.54) * mm, "end": v(9.98, 101.28) * mm});
            skArc(sketch, "E14.4.50.0", {"start": v(11.5, 104.22) * mm, "mid": v(10.71, 102.76) * mm, "end": v(9.98, 101.28) * mm});
            skArc(sketch, "E14.8.50.0", {"start": v(14.27, 103.88) * mm, "mid": v(12.89, 104.06) * mm, "end": v(11.5, 104.22) * mm});
            skArc(sketch, "E14.12.50.0", {"start": v(15.04, 100.62) * mm, "mid": v(14.68, 102.26) * mm, "end": v(14.27, 103.88) * mm});
            skArc(sketch, "E14.16.50.0", {"start": v(15.03, 100.65) * mm, "mid": v(16.14, 98.58) * mm, "end": v(18.22, 97.5) * mm});
            skCircle(sketch, "E15", {"center": v(0, 0) * mm, "radius": 55 * mm, "construction": true});
            skCircle(sketch, "E16", {"center": v(0, -55) * mm, "radius": 5 * mm});
            skCircle(sketch, "E17", {"center": v(0, 0) * mm, "radius": 91.43 * mm});
            skLineSegment(sketch, "E18.bottom", {"start": v(-8, -47) * mm, "end": v(8, -47) * mm});
            skLineSegment(sketch, "E18.left", {"start": v(-8, -47) * mm, "end": v(-8, -82.38) * mm});
            skLineSegment(sketch, "E18.right", {"start": v(8, -47) * mm, "end": v(8, -82.38) * mm});
            skArc(sketch, "E19", {"start": v(-17, -89.84) * mm, "mid": v(-10.75, -88.22) * mm, "end": v(-8, -82.38) * mm});
            skArc(sketch, "E20", {"start": v(8, -82.38) * mm, "mid": v(10.75, -88.22) * mm, "end": v(17, -89.84) * mm});
            skArc(sketch, "E21.1.0", {"start": v(80.19, -43.92) * mm, "mid": v(80.59, -37.48) * mm, "end": v(75.88, -33.07) * mm});
            skLineSegment(sketch, "E21.1.1", {"start": v(42.23, -22.13) * mm, "end": v(75.88, -33.07) * mm});
            skLineSegment(sketch, "E21.1.2", {"start": v(42.23, -22.13) * mm, "end": v(47.17, -6.92) * mm});
            skCircle(sketch, "E21.1.3", {"center": v(52.3, -17) * mm, "radius": 5 * mm});
            skLineSegment(sketch, "E21.1.4", {"start": v(47.17, -6.92) * mm, "end": v(80.82, -17.85) * mm});
            skArc(sketch, "E21.1.5", {"start": v(80.82, -17.85) * mm, "mid": v(87.23, -17.04) * mm, "end": v(90.7, -11.6) * mm});
            skArc(sketch, "E21.2.0", {"start": v(66.55, 62.7) * mm, "mid": v(60.55, 65.06) * mm, "end": v(54.9, 61.95) * mm});
            skLineSegment(sketch, "E21.2.1", {"start": v(34.1, 33.32) * mm, "end": v(54.9, 61.95) * mm});
            skLineSegment(sketch, "E21.2.2", {"start": v(34.1, 33.32) * mm, "end": v(21.15, 42.73) * mm});
            skCircle(sketch, "E21.2.3", {"center": v(32.33, 44.5) * mm, "radius": 5 * mm});
            skLineSegment(sketch, "E21.2.4", {"start": v(21.15, 42.73) * mm, "end": v(41.95, 71.35) * mm});
            skArc(sketch, "E21.2.5", {"start": v(41.95, 71.35) * mm, "mid": v(43.16, 77.7) * mm, "end": v(39.06, 82.67) * mm});
            skArc(sketch, "E21.3.0", {"start": v(-39.06, 82.67) * mm, "mid": v(-43.16, 77.7) * mm, "end": v(-41.95, 71.35) * mm});
            skLineSegment(sketch, "E21.3.1", {"start": v(-21.15, 42.73) * mm, "end": v(-41.95, 71.35) * mm});
            skLineSegment(sketch, "E21.3.2", {"start": v(-21.15, 42.73) * mm, "end": v(-34.1, 33.32) * mm});
            skCircle(sketch, "E21.3.3", {"center": v(-32.33, 44.5) * mm, "radius": 5 * mm});
            skLineSegment(sketch, "E21.3.4", {"start": v(-34.1, 33.32) * mm, "end": v(-54.9, 61.95) * mm});
            skArc(sketch, "E21.3.5", {"start": v(-54.9, 61.95) * mm, "mid": v(-60.55, 65.06) * mm, "end": v(-66.55, 62.7) * mm});
            skArc(sketch, "E21.4.0", {"start": v(-90.7, -11.6) * mm, "mid": v(-87.23, -17.04) * mm, "end": v(-80.82, -17.85) * mm});
            skLineSegment(sketch, "E21.4.1", {"start": v(-47.17, -6.92) * mm, "end": v(-80.82, -17.85) * mm});
            skLineSegment(sketch, "E21.4.2", {"start": v(-47.17, -6.92) * mm, "end": v(-42.23, -22.13) * mm});
            skCircle(sketch, "E21.4.3", {"center": v(-52.3, -17) * mm, "radius": 5 * mm});
            skLineSegment(sketch, "E21.4.4", {"start": v(-42.23, -22.13) * mm, "end": v(-75.88, -33.07) * mm});
            skArc(sketch, "E21.4.5", {"start": v(-75.88, -33.07) * mm, "mid": v(-80.59, -37.48) * mm, "end": v(-80.19, -43.92) * mm});
            skCircle(sketch, "E22", {"center": v(0, 0) * mm, "radius": 95.24 * mm});
            skArc(sketch, "E23", {"start": v(-48.46, -20.2) * mm, "mid": v(-30.86, -42.47) * mm, "end": v(-4.23, -52.33) * mm});
            skArc(sketch, "E24", {"start": v(-53.16, -21.92) * mm, "mid": v(-33.8, -46.52) * mm, "end": v(-4.42, -57.33) * mm});
            skArc(sketch, "E25.trimOffspring", {"start": v(51.07, -12.15) * mm, "mid": v(49.93, 16.22) * mm, "end": v(34.18, 39.85) * mm});
            skArc(sketch, "E26.trimOffspring", {"start": v(55.9, -13.5) * mm, "mid": v(54.69, 17.77) * mm, "end": v(37.28, 43.78) * mm});
            skArc(sketch, "E27.trimOffspring", {"start": v(-34.18, 39.85) * mm, "mid": v(-49.93, 16.22) * mm, "end": v(-51.07, -12.15) * mm});
            skArc(sketch, "E28.trimOffspring", {"start": v(-37.28, 43.78) * mm, "mid": v(-54.69, 17.77) * mm, "end": v(-55.9, -13.5) * mm});
            skArc(sketch, "E29.trimOffspring", {"start": v(27.34, 44.82) * mm, "mid": v(0, 52.5) * mm, "end": v(-27.34, 44.82) * mm});
            skArc(sketch, "E30.trimOffspring", {"start": v(30.12, 48.98) * mm, "mid": v(0, 57.5) * mm, "end": v(-30.12, 48.98) * mm});
            skSolve(sketch);
        }
        {
            var Q0;
            Q0=qCreatedBy(makeId("Front.planeOp"),FACE);
            var sketch = newSketch(context, id + "F1", { "sketchPlane" : qUnion([Q0])});
            skLineSegment(sketch, "E31", {"start": v(57.82, -72.41) * mm, "end": v(57.1, -72.98) * mm});
            skLineSegment(sketch, "E32", {"start": v(57.1, -72.98) * mm, "end": v(56.82, -73.15) * mm});
            skLineSegment(sketch, "E33", {"start": v(56.82, -73.15) * mm, "end": v(55.3, -74.24) * mm});
            skLineSegment(sketch, "E34", {"start": v(55.3, -74.24) * mm, "end": v(51.03, -77.37) * mm});
            skLineSegment(sketch, "E35", {"start": v(51.03, -77.37) * mm, "end": v(47.94, -79.39) * mm});
            skLineSegment(sketch, "E36", {"start": v(47.94, -79.39) * mm, "end": v(45.18, -80.98) * mm});
            skLineSegment(sketch, "E37", {"start": v(45.18, -80.98) * mm, "end": v(43.93, -81.67) * mm});
            skLineSegment(sketch, "E38", {"start": v(43.93, -81.67) * mm, "end": v(37.46, -84.65) * mm});
            skLineSegment(sketch, "E39", {"start": v(37.46, -84.65) * mm, "end": v(37.31, -84.68) * mm});
            skLineSegment(sketch, "E40", {"start": v(37.31, -84.68) * mm, "end": v(37.22, -84.06) * mm});
            skLineSegment(sketch, "E41", {"start": v(37.22, -84.06) * mm, "end": v(37.17, -81.72) * mm});
            skLineSegment(sketch, "E42", {"start": v(37.17, -81.72) * mm, "end": v(37.2, -81.52) * mm});
            skLineSegment(sketch, "E43", {"start": v(37.2, -81.52) * mm, "end": v(37.6, -80.93) * mm});
            skLineSegment(sketch, "E44", {"start": v(37.6, -80.93) * mm, "end": v(38.14, -80.6) * mm});
            skLineSegment(sketch, "E45", {"start": v(38.14, -80.6) * mm, "end": v(38.52, -80.24) * mm});
            skLineSegment(sketch, "E46", {"start": v(38.52, -80.24) * mm, "end": v(38.64, -79.82) * mm});
            skLineSegment(sketch, "E47", {"start": v(38.64, -79.82) * mm, "end": v(39.24, -79.1) * mm});
            skLineSegment(sketch, "E48", {"start": v(39.24, -79.1) * mm, "end": v(39.65, -78.59) * mm});
            skLineSegment(sketch, "E49", {"start": v(39.65, -78.59) * mm, "end": v(39.9, -77.63) * mm});
            skLineSegment(sketch, "E50", {"start": v(39.9, -77.63) * mm, "end": v(40.2, -77.36) * mm});
            skLineSegment(sketch, "E51", {"start": v(40.2, -77.36) * mm, "end": v(41.06, -77.25) * mm});
            skLineSegment(sketch, "E52", {"start": v(41.06, -77.25) * mm, "end": v(42.05, -77.04) * mm});
            skLineSegment(sketch, "E53", {"start": v(42.05, -77.04) * mm, "end": v(42.24, -76.97) * mm});
            skLineSegment(sketch, "E54", {"start": v(42.24, -76.97) * mm, "end": v(42.84, -76.94) * mm});
            skLineSegment(sketch, "E55", {"start": v(42.84, -76.94) * mm, "end": v(43.95, -77.21) * mm});
            skLineSegment(sketch, "E56", {"start": v(43.95, -77.21) * mm, "end": v(44.46, -77.53) * mm});
            skLineSegment(sketch, "E57", {"start": v(44.46, -77.53) * mm, "end": v(44.82, -77.93) * mm});
            skLineSegment(sketch, "E58", {"start": v(44.82, -77.93) * mm, "end": v(45.54, -78.86) * mm});
            skLineSegment(sketch, "E59", {"start": v(45.54, -78.86) * mm, "end": v(46.52, -78.37) * mm});
            skLineSegment(sketch, "E60", {"start": v(46.52, -78.37) * mm, "end": v(46.74, -78.2) * mm});
            skLineSegment(sketch, "E61", {"start": v(46.74, -78.2) * mm, "end": v(46.9, -77.93) * mm});
            skLineSegment(sketch, "E62", {"start": v(46.9, -77.93) * mm, "end": v(47.35, -73.44) * mm});
            skLineSegment(sketch, "E63", {"start": v(47.35, -73.44) * mm, "end": v(47.35, -72.02) * mm});
            skLineSegment(sketch, "E64", {"start": v(47.35, -72.02) * mm, "end": v(46.95, -71.35) * mm});
            skLineSegment(sketch, "E65", {"start": v(46.95, -71.35) * mm, "end": v(46.52, -71.24) * mm});
            skLineSegment(sketch, "E66", {"start": v(46.52, -71.24) * mm, "end": v(44.69, -71.36) * mm});
            skLineSegment(sketch, "E67", {"start": v(44.69, -71.36) * mm, "end": v(44.05, -71.32) * mm});
            skLineSegment(sketch, "E68", {"start": v(44.05, -71.32) * mm, "end": v(41.97, -70.97) * mm});
            skLineSegment(sketch, "E69", {"start": v(41.97, -70.97) * mm, "end": v(41.39, -70.97) * mm});
            skLineSegment(sketch, "E70", {"start": v(41.39, -70.97) * mm, "end": v(40.6, -71.24) * mm});
            skLineSegment(sketch, "E71", {"start": v(40.6, -71.24) * mm, "end": v(38.73, -71.92) * mm});
            skLineSegment(sketch, "E72", {"start": v(38.73, -71.92) * mm, "end": v(37.54, -72.26) * mm});
            skLineSegment(sketch, "E73", {"start": v(37.54, -72.26) * mm, "end": v(36.48, -72.45) * mm});
            skLineSegment(sketch, "E74", {"start": v(36.48, -72.45) * mm, "end": v(36.26, -72.4) * mm});
            skLineSegment(sketch, "E75", {"start": v(36.26, -72.4) * mm, "end": v(35.07, -72.03) * mm});
            skLineSegment(sketch, "E76", {"start": v(35.07, -72.03) * mm, "end": v(34.7, -71.97) * mm});
            skLineSegment(sketch, "E77", {"start": v(34.7, -71.97) * mm, "end": v(32.84, -71.95) * mm});
            skLineSegment(sketch, "E78", {"start": v(32.84, -71.95) * mm, "end": v(31.85, -71.75) * mm});
            skLineSegment(sketch, "E79", {"start": v(31.85, -71.75) * mm, "end": v(31.45, -71.25) * mm});
            skLineSegment(sketch, "E80", {"start": v(31.45, -71.25) * mm, "end": v(31.35, -70.68) * mm});
            skLineSegment(sketch, "E81", {"start": v(31.35, -70.68) * mm, "end": v(30.99, -70.74) * mm});
            skLineSegment(sketch, "E82", {"start": v(30.99, -70.74) * mm, "end": v(27.61, -71.27) * mm});
            skLineSegment(sketch, "E83", {"start": v(27.61, -71.27) * mm, "end": v(24.56, -72.04) * mm});
            skLineSegment(sketch, "E84", {"start": v(24.56, -72.04) * mm, "end": v(22.22, -71.68) * mm});
            skLineSegment(sketch, "E85", {"start": v(22.22, -71.68) * mm, "end": v(18, -72.08) * mm});
            skLineSegment(sketch, "E86", {"start": v(18, -72.08) * mm, "end": v(17.08, -71.9) * mm});
            skLineSegment(sketch, "E87", {"start": v(17.08, -71.9) * mm, "end": v(11.63, -68.46) * mm});
            skLineSegment(sketch, "E88", {"start": v(11.63, -68.46) * mm, "end": v(10.84, -68.17) * mm});
            skLineSegment(sketch, "E89", {"start": v(10.84, -68.17) * mm, "end": v(8, -66.78) * mm});
            skLineSegment(sketch, "E90", {"start": v(8, -66.78) * mm, "end": v(5.1, -65.42) * mm});
            skLineSegment(sketch, "E91", {"start": v(5.1, -65.42) * mm, "end": v(3.84, -64.95) * mm});
            skLineSegment(sketch, "E92", {"start": v(3.84, -64.95) * mm, "end": v(-1.7, -63.65) * mm});
            skLineSegment(sketch, "E93", {"start": v(-1.7, -63.65) * mm, "end": v(-8.1, -62.28) * mm});
            skLineSegment(sketch, "E94", {"start": v(-8.1, -62.28) * mm, "end": v(-8.97, -62) * mm});
            skLineSegment(sketch, "E95", {"start": v(-8.97, -62) * mm, "end": v(-11.16, -61.68) * mm});
            skLineSegment(sketch, "E96", {"start": v(-11.16, -61.68) * mm, "end": v(-12.2, -61.45) * mm});
            skLineSegment(sketch, "E97", {"start": v(-12.2, -61.45) * mm, "end": v(-14.72, -62.34) * mm});
            skLineSegment(sketch, "E98", {"start": v(-14.72, -62.34) * mm, "end": v(-15.44, -62.18) * mm});
            skLineSegment(sketch, "E99", {"start": v(-15.44, -62.18) * mm, "end": v(-15.69, -62.04) * mm});
            skLineSegment(sketch, "E100", {"start": v(-15.69, -62.04) * mm, "end": v(-15.85, -62.02) * mm});
            skLineSegment(sketch, "E101", {"start": v(-15.85, -62.02) * mm, "end": v(-16.88, -62.53) * mm});
            skLineSegment(sketch, "E102", {"start": v(-16.88, -62.53) * mm, "end": v(-16.96, -62.62) * mm});
            skLineSegment(sketch, "E103", {"start": v(-16.96, -62.62) * mm, "end": v(-17, -62.58) * mm});
            skLineSegment(sketch, "E104", {"start": v(-17, -62.58) * mm, "end": v(-16.83, -62.29) * mm});
            skLineSegment(sketch, "E105", {"start": v(-16.83, -62.29) * mm, "end": v(-16.75, -62.24) * mm});
            skLineSegment(sketch, "E106", {"start": v(-16.75, -62.24) * mm, "end": v(-16.2, -61.5) * mm});
            skLineSegment(sketch, "E107", {"start": v(-16.2, -61.5) * mm, "end": v(-15.2, -60.22) * mm});
            skLineSegment(sketch, "E108", {"start": v(-15.2, -60.22) * mm, "end": v(-12.64, -57.35) * mm});
            skLineSegment(sketch, "E109", {"start": v(-12.64, -57.35) * mm, "end": v(-10.53, -56.04) * mm});
            skLineSegment(sketch, "E110", {"start": v(-10.53, -56.04) * mm, "end": v(-7.63, -53.51) * mm});
            skLineSegment(sketch, "E111", {"start": v(-7.63, -53.51) * mm, "end": v(-7.06, -53.09) * mm});
            skLineSegment(sketch, "E112", {"start": v(-7.06, -53.09) * mm, "end": v(-3.19, -50.63) * mm});
            skLineSegment(sketch, "E113", {"start": v(-3.19, -50.63) * mm, "end": v(-0.72, -49.52) * mm});
            skLineSegment(sketch, "E114", {"start": v(-0.72, -49.52) * mm, "end": v(-0.18, -49.41) * mm});
            skLineSegment(sketch, "E115", {"start": v(-0.18, -49.41) * mm, "end": v(5.14, -48.5) * mm});
            skLineSegment(sketch, "E116", {"start": v(5.14, -48.5) * mm, "end": v(6.07, -48.37) * mm});
            skLineSegment(sketch, "E117", {"start": v(6.07, -48.37) * mm, "end": v(9.2, -47.74) * mm});
            skLineSegment(sketch, "E118", {"start": v(9.2, -47.74) * mm, "end": v(10.26, -47.6) * mm});
            skLineSegment(sketch, "E119", {"start": v(10.26, -47.6) * mm, "end": v(18.53, -49.67) * mm});
            skLineSegment(sketch, "E120", {"start": v(18.53, -49.67) * mm, "end": v(19.62, -49.9) * mm});
            skLineSegment(sketch, "E121", {"start": v(19.62, -49.9) * mm, "end": v(31.04, -53.18) * mm});
            skLineSegment(sketch, "E122", {"start": v(31.04, -53.18) * mm, "end": v(31.78, -53.36) * mm});
            skLineSegment(sketch, "E123", {"start": v(31.78, -53.36) * mm, "end": v(32.93, -53.16) * mm});
            skLineSegment(sketch, "E124", {"start": v(32.93, -53.16) * mm, "end": v(33.67, -52.83) * mm});
            skLineSegment(sketch, "E125", {"start": v(33.67, -52.83) * mm, "end": v(33.87, -52.68) * mm});
            skLineSegment(sketch, "E126", {"start": v(33.87, -52.68) * mm, "end": v(34.75, -51.98) * mm});
            skLineSegment(sketch, "E127", {"start": v(34.75, -51.98) * mm, "end": v(35.91, -50.67) * mm});
            skLineSegment(sketch, "E128", {"start": v(35.91, -50.67) * mm, "end": v(36.76, -49.95) * mm});
            skLineSegment(sketch, "E129", {"start": v(36.76, -49.95) * mm, "end": v(38.15, -49.16) * mm});
            skLineSegment(sketch, "E130", {"start": v(38.15, -49.16) * mm, "end": v(39.57, -48.25) * mm});
            skLineSegment(sketch, "E131", {"start": v(39.57, -48.25) * mm, "end": v(40.04, -47.8) * mm});
            skLineSegment(sketch, "E132", {"start": v(40.04, -47.8) * mm, "end": v(40.92, -46.46) * mm});
            skLineSegment(sketch, "E133", {"start": v(40.92, -46.46) * mm, "end": v(41.04, -46.18) * mm});
            skLineSegment(sketch, "E134", {"start": v(41.04, -46.18) * mm, "end": v(41.1, -45.9) * mm});
            skLineSegment(sketch, "E135", {"start": v(41.1, -45.9) * mm, "end": v(40.89, -43.37) * mm});
            skLineSegment(sketch, "E136", {"start": v(40.89, -43.37) * mm, "end": v(39.64, -30.68) * mm});
            skLineSegment(sketch, "E137", {"start": v(39.64, -30.68) * mm, "end": v(40.87, -27.5) * mm});
            skLineSegment(sketch, "E138", {"start": v(40.87, -27.5) * mm, "end": v(41.53, -25.06) * mm});
            skLineSegment(sketch, "E139", {"start": v(41.53, -25.06) * mm, "end": v(41.79, -24.1) * mm});
            skLineSegment(sketch, "E140", {"start": v(41.79, -24.1) * mm, "end": v(42.35, -22.6) * mm});
            skLineSegment(sketch, "E141", {"start": v(42.35, -22.6) * mm, "end": v(43.14, -20.72) * mm});
            skLineSegment(sketch, "E142", {"start": v(43.14, -20.72) * mm, "end": v(44.15, -17.54) * mm});
            skLineSegment(sketch, "E143", {"start": v(44.15, -17.54) * mm, "end": v(45.03, -15.94) * mm});
            skLineSegment(sketch, "E144", {"start": v(45.03, -15.94) * mm, "end": v(45.9, -14.58) * mm});
            skLineSegment(sketch, "E145", {"start": v(45.9, -14.58) * mm, "end": v(47.26, -12.52) * mm});
            skLineSegment(sketch, "E146", {"start": v(47.26, -12.52) * mm, "end": v(49.6, -9.18) * mm});
            skLineSegment(sketch, "E147", {"start": v(49.6, -9.18) * mm, "end": v(50.18, -8.57) * mm});
            skLineSegment(sketch, "E148", {"start": v(50.18, -8.57) * mm, "end": v(52.14, -7.13) * mm});
            skLineSegment(sketch, "E149", {"start": v(52.14, -7.13) * mm, "end": v(53.5, -6.38) * mm});
            skLineSegment(sketch, "E150", {"start": v(53.5, -6.38) * mm, "end": v(55.47, -4.86) * mm});
            skLineSegment(sketch, "E151", {"start": v(55.47, -4.86) * mm, "end": v(58.26, -3.5) * mm});
            skLineSegment(sketch, "E152", {"start": v(58.26, -3.5) * mm, "end": v(60.56, -2.6) * mm});
            skLineSegment(sketch, "E153", {"start": v(60.56, -2.6) * mm, "end": v(62.2, -1.88) * mm});
            skLineSegment(sketch, "E154", {"start": v(62.2, -1.88) * mm, "end": v(63.9, -0.84) * mm});
            skLineSegment(sketch, "E155", {"start": v(63.9, -0.84) * mm, "end": v(63.92, -0.94) * mm});
            skLineSegment(sketch, "E156", {"start": v(63.92, -0.94) * mm, "end": v(63.7, -2.37) * mm});
            skLineSegment(sketch, "E157", {"start": v(63.7, -2.37) * mm, "end": v(63.66, -2.53) * mm});
            skLineSegment(sketch, "E158", {"start": v(63.66, -2.53) * mm, "end": v(64, -3.4) * mm});
            skLineSegment(sketch, "E159", {"start": v(64, -3.4) * mm, "end": v(64.02, -3.48) * mm});
            skLineSegment(sketch, "E160", {"start": v(64.02, -3.48) * mm, "end": v(63.9, -3.49) * mm});
            skLineSegment(sketch, "E161", {"start": v(63.9, -3.49) * mm, "end": v(62.78, -3.72) * mm});
            skLineSegment(sketch, "E162", {"start": v(62.78, -3.72) * mm, "end": v(62.58, -3.79) * mm});
            skLineSegment(sketch, "E163", {"start": v(62.58, -3.79) * mm, "end": v(62.17, -4.69) * mm});
            skLineSegment(sketch, "E164", {"start": v(62.17, -4.69) * mm, "end": v(61.42, -7.83) * mm});
            skLineSegment(sketch, "E165", {"start": v(61.42, -7.83) * mm, "end": v(61.33, -8.3) * mm});
            skLineSegment(sketch, "E166", {"start": v(61.33, -8.3) * mm, "end": v(60.88, -12.13) * mm});
            skLineSegment(sketch, "E167", {"start": v(60.88, -12.13) * mm, "end": v(60.6, -13.68) * mm});
            skLineSegment(sketch, "E168", {"start": v(60.6, -13.68) * mm, "end": v(59.7, -17.6) * mm});
            skLineSegment(sketch, "E169", {"start": v(59.7, -17.6) * mm, "end": v(59.6, -18.08) * mm});
            skLineSegment(sketch, "E170", {"start": v(59.6, -18.08) * mm, "end": v(59.56, -19.12) * mm});
            skLineSegment(sketch, "E171", {"start": v(59.56, -19.12) * mm, "end": v(60.7, -30.73) * mm});
            skLineSegment(sketch, "E172", {"start": v(60.7, -30.73) * mm, "end": v(60.8, -32.79) * mm});
            skLineSegment(sketch, "E173", {"start": v(60.8, -32.79) * mm, "end": v(61.87, -36.06) * mm});
            skLineSegment(sketch, "E174", {"start": v(61.87, -36.06) * mm, "end": v(61.97, -36.86) * mm});
            skLineSegment(sketch, "E175", {"start": v(61.97, -36.86) * mm, "end": v(61.57, -40.64) * mm});
            skLineSegment(sketch, "E176", {"start": v(61.57, -40.64) * mm, "end": v(61.33, -41.41) * mm});
            skLineSegment(sketch, "E177", {"start": v(61.33, -41.41) * mm, "end": v(60.23, -43.48) * mm});
            skLineSegment(sketch, "E178", {"start": v(60.23, -43.48) * mm, "end": v(59.56, -45.1) * mm});
            skLineSegment(sketch, "E179", {"start": v(59.56, -45.1) * mm, "end": v(58.27, -49.26) * mm});
            skLineSegment(sketch, "E180", {"start": v(58.27, -49.26) * mm, "end": v(58.35, -49.89) * mm});
            skLineSegment(sketch, "E181", {"start": v(58.35, -49.89) * mm, "end": v(58.52, -50.2) * mm});
            skLineSegment(sketch, "E182", {"start": v(58.52, -50.2) * mm, "end": v(58.51, -51.48) * mm});
            skLineSegment(sketch, "E183", {"start": v(58.51, -51.48) * mm, "end": v(58.34, -52) * mm});
            skLineSegment(sketch, "E184", {"start": v(58.34, -52) * mm, "end": v(58.42, -52.63) * mm});
            skLineSegment(sketch, "E185", {"start": v(58.42, -52.63) * mm, "end": v(58.4, -53.06) * mm});
            skLineSegment(sketch, "E186", {"start": v(58.4, -53.06) * mm, "end": v(57.77, -55.26) * mm});
            skLineSegment(sketch, "E187", {"start": v(57.77, -55.26) * mm, "end": v(57.61, -55.6) * mm});
            skLineSegment(sketch, "E188", {"start": v(57.61, -55.6) * mm, "end": v(56.9, -56.66) * mm});
            skLineSegment(sketch, "E189", {"start": v(56.9, -56.66) * mm, "end": v(55.95, -58.63) * mm});
            skLineSegment(sketch, "E190", {"start": v(55.95, -58.63) * mm, "end": v(55.87, -59.15) * mm});
            skLineSegment(sketch, "E191", {"start": v(55.87, -59.15) * mm, "end": v(55.93, -60.62) * mm});
            skLineSegment(sketch, "E192", {"start": v(55.93, -60.62) * mm, "end": v(56.24, -61.49) * mm});
            skLineSegment(sketch, "E193", {"start": v(56.24, -61.49) * mm, "end": v(56.27, -61.53) * mm});
            skLineSegment(sketch, "E194", {"start": v(56.27, -61.53) * mm, "end": v(56.64, -61.83) * mm});
            skLineSegment(sketch, "E195", {"start": v(56.64, -61.83) * mm, "end": v(58.03, -62.51) * mm});
            skLineSegment(sketch, "E196", {"start": v(58.03, -62.51) * mm, "end": v(60.36, -63.7) * mm});
            skLineSegment(sketch, "E197", {"start": v(60.36, -63.7) * mm, "end": v(63.5, -64.83) * mm});
            skLineSegment(sketch, "E198", {"start": v(63.5, -64.83) * mm, "end": v(63.75, -64.75) * mm});
            skLineSegment(sketch, "E199", {"start": v(63.75, -64.75) * mm, "end": v(65.07, -63.59) * mm});
            skLineSegment(sketch, "E200", {"start": v(65.07, -63.59) * mm, "end": v(65.21, -63.43) * mm});
            skLineSegment(sketch, "E201", {"start": v(65.21, -63.43) * mm, "end": v(64.94, -63.26) * mm});
            skLineSegment(sketch, "E202", {"start": v(64.94, -63.26) * mm, "end": v(64.57, -62.83) * mm});
            skLineSegment(sketch, "E203", {"start": v(64.57, -62.83) * mm, "end": v(64.32, -62.3) * mm});
            skLineSegment(sketch, "E204", {"start": v(64.32, -62.3) * mm, "end": v(64.26, -61.58) * mm});
            skLineSegment(sketch, "E205", {"start": v(64.26, -61.58) * mm, "end": v(64.5, -61.29) * mm});
            skLineSegment(sketch, "E206", {"start": v(64.5, -61.29) * mm, "end": v(64.91, -60.61) * mm});
            skLineSegment(sketch, "E207", {"start": v(64.91, -60.61) * mm, "end": v(64.9, -60.46) * mm});
            skLineSegment(sketch, "E208", {"start": v(64.9, -60.46) * mm, "end": v(64.81, -59.44) * mm});
            skLineSegment(sketch, "E209", {"start": v(64.81, -59.44) * mm, "end": v(64.83, -59.2) * mm});
            skLineSegment(sketch, "E210", {"start": v(64.83, -59.2) * mm, "end": v(65.1, -58.61) * mm});
            skLineSegment(sketch, "E211", {"start": v(65.1, -58.61) * mm, "end": v(65.4, -58.37) * mm});
            skLineSegment(sketch, "E212", {"start": v(65.4, -58.37) * mm, "end": v(66.28, -58.1) * mm});
            skLineSegment(sketch, "E213", {"start": v(66.28, -58.1) * mm, "end": v(66.63, -57.98) * mm});
            skLineSegment(sketch, "E214", {"start": v(66.63, -57.98) * mm, "end": v(66.64, -57.78) * mm});
            skLineSegment(sketch, "E215", {"start": v(66.64, -57.78) * mm, "end": v(66.7, -57.25) * mm});
            skLineSegment(sketch, "E216", {"start": v(66.7, -57.25) * mm, "end": v(67.08, -56.86) * mm});
            skLineSegment(sketch, "E217", {"start": v(67.08, -56.86) * mm, "end": v(67.19, -56.76) * mm});
            skLineSegment(sketch, "E218", {"start": v(67.19, -56.76) * mm, "end": v(67.75, -56.53) * mm});
            skLineSegment(sketch, "E219", {"start": v(67.75, -56.53) * mm, "end": v(68.14, -56.53) * mm});
            skLineSegment(sketch, "E220", {"start": v(68.14, -56.53) * mm, "end": v(68.58, -56.6) * mm});
            skLineSegment(sketch, "E221", {"start": v(68.58, -56.6) * mm, "end": v(69.37, -56.9) * mm});
            skLineSegment(sketch, "E222", {"start": v(69.37, -56.9) * mm, "end": v(69.54, -56.52) * mm});
            skLineSegment(sketch, "E223", {"start": v(69.54, -56.52) * mm, "end": v(70.13, -56.48) * mm});
            skLineSegment(sketch, "E224", {"start": v(70.13, -56.48) * mm, "end": v(70.33, -56.5) * mm});
            skLineSegment(sketch, "E225", {"start": v(70.33, -56.5) * mm, "end": v(71.32, -57.02) * mm});
            skLineSegment(sketch, "E226", {"start": v(71.32, -57.02) * mm, "end": v(72.28, -57.64) * mm});
            skLineSegment(sketch, "E227", {"start": v(72.28, -57.64) * mm, "end": v(72.6, -57.86) * mm});
            skLineSegment(sketch, "E228", {"start": v(72.6, -57.86) * mm, "end": v(72.49, -58.02) * mm});
            skLineSegment(sketch, "E229", {"start": v(72.49, -58.02) * mm, "end": v(70.01, -60.82) * mm});
            skLineSegment(sketch, "E230", {"start": v(70.01, -60.82) * mm, "end": v(66.6, -64.7) * mm});
            skLineSegment(sketch, "E231", {"start": v(66.6, -64.7) * mm, "end": v(65.73, -65.66) * mm});
            skLineSegment(sketch, "E232", {"start": v(65.73, -65.66) * mm, "end": v(62.5, -68.4) * mm});
            skLineSegment(sketch, "E233", {"start": v(62.5, -68.4) * mm, "end": v(58.67, -71.64) * mm});
            skLineSegment(sketch, "E234", {"start": v(58.67, -71.64) * mm, "end": v(57.82, -72.41) * mm});
            skLineSegment(sketch, "E235", {"start": v(35.69, -61.97) * mm, "end": v(36.07, -60.95) * mm});
            skLineSegment(sketch, "E236", {"start": v(36.07, -60.95) * mm, "end": v(37.04, -58.68) * mm});
            skLineSegment(sketch, "E237", {"start": v(37.04, -58.68) * mm, "end": v(38.06, -57.6) * mm});
            skLineSegment(sketch, "E238", {"start": v(38.06, -57.6) * mm, "end": v(39.7, -56.59) * mm});
            skLineSegment(sketch, "E239", {"start": v(39.7, -56.59) * mm, "end": v(40.66, -56.37) * mm});
            skLineSegment(sketch, "E240", {"start": v(40.66, -56.37) * mm, "end": v(41.85, -56.44) * mm});
            skLineSegment(sketch, "E241", {"start": v(41.85, -56.44) * mm, "end": v(41.9, -56.36) * mm});
            skLineSegment(sketch, "E242", {"start": v(41.9, -56.36) * mm, "end": v(42.55, -54.81) * mm});
            skLineSegment(sketch, "E243", {"start": v(42.55, -54.81) * mm, "end": v(43.12, -53.92) * mm});
            skLineSegment(sketch, "E244", {"start": v(43.12, -53.92) * mm, "end": v(43.9, -53.25) * mm});
            skLineSegment(sketch, "E245", {"start": v(43.9, -53.25) * mm, "end": v(44.54, -52.8) * mm});
            skLineSegment(sketch, "E246", {"start": v(44.54, -52.8) * mm, "end": v(45.47, -52.28) * mm});
            skLineSegment(sketch, "E247", {"start": v(45.47, -52.28) * mm, "end": v(46.99, -51.62) * mm});
            skLineSegment(sketch, "E248", {"start": v(46.99, -51.62) * mm, "end": v(48.17, -51.33) * mm});
            skLineSegment(sketch, "E249", {"start": v(48.17, -51.33) * mm, "end": v(49, -51.34) * mm});
            skLineSegment(sketch, "E250", {"start": v(49, -51.34) * mm, "end": v(50.35, -51.74) * mm});
            skLineSegment(sketch, "E251", {"start": v(50.35, -51.74) * mm, "end": v(51.1, -52.06) * mm});
            skLineSegment(sketch, "E252", {"start": v(51.1, -52.06) * mm, "end": v(52.08, -52.64) * mm});
            skLineSegment(sketch, "E253", {"start": v(52.08, -52.64) * mm, "end": v(52.38, -52.8) * mm});
            skLineSegment(sketch, "E254", {"start": v(52.38, -52.8) * mm, "end": v(52.29, -52.28) * mm});
            skLineSegment(sketch, "E255", {"start": v(52.29, -52.28) * mm, "end": v(51.39, -48.7) * mm});
            skLineSegment(sketch, "E256", {"start": v(51.39, -48.7) * mm, "end": v(50.83, -48.06) * mm});
            skLineSegment(sketch, "E257", {"start": v(50.83, -48.06) * mm, "end": v(47.95, -46.9) * mm});
            skLineSegment(sketch, "E258", {"start": v(47.95, -46.9) * mm, "end": v(47.55, -46.72) * mm});
            skLineSegment(sketch, "E259", {"start": v(47.55, -46.72) * mm, "end": v(49, -46.11) * mm});
            skLineSegment(sketch, "E260", {"start": v(49, -46.11) * mm, "end": v(50.26, -45.93) * mm});
            skLineSegment(sketch, "E261", {"start": v(50.26, -45.93) * mm, "end": v(50.28, -45.64) * mm});
            skLineSegment(sketch, "E262", {"start": v(50.28, -45.64) * mm, "end": v(50.36, -44.19) * mm});
            skLineSegment(sketch, "E263", {"start": v(50.36, -44.19) * mm, "end": v(50.65, -43.33) * mm});
            skLineSegment(sketch, "E264", {"start": v(50.65, -43.33) * mm, "end": v(51.45, -42.12) * mm});
            skLineSegment(sketch, "E265", {"start": v(51.45, -42.12) * mm, "end": v(51.8, -41.2) * mm});
            skLineSegment(sketch, "E266", {"start": v(51.8, -41.2) * mm, "end": v(52.22, -38.07) * mm});
            skLineSegment(sketch, "E267", {"start": v(52.22, -38.07) * mm, "end": v(51.49, -35.09) * mm});
            skLineSegment(sketch, "E268", {"start": v(51.49, -35.09) * mm, "end": v(50.82, -26.55) * mm});
            skLineSegment(sketch, "E269", {"start": v(50.82, -26.55) * mm, "end": v(50.6, -24.38) * mm});
            skLineSegment(sketch, "E270", {"start": v(50.6, -24.38) * mm, "end": v(50.14, -22.02) * mm});
            skLineSegment(sketch, "E271", {"start": v(50.14, -22.02) * mm, "end": v(50.14, -21.5) * mm});
            skLineSegment(sketch, "E272", {"start": v(52.65, -12) * mm, "end": v(52.82, -11.6) * mm});
            skLineSegment(sketch, "E273", {"start": v(52.82, -11.6) * mm, "end": v(53.1, -11.07) * mm});
            skLineSegment(sketch, "E274", {"start": v(53.1, -11.07) * mm, "end": v(54.92, -8.4) * mm});
            skLineSegment(sketch, "E275", {"start": v(54.92, -8.4) * mm, "end": v(55.8, -7.44) * mm});
            skLineSegment(sketch, "E276", {"start": v(55.8, -7.44) * mm, "end": v(58.59, -5.18) * mm});
            skLineSegment(sketch, "E277", {"start": v(58.59, -5.18) * mm, "end": v(58.8, -4.98) * mm});
            skLineSegment(sketch, "E278", {"start": v(58.8, -4.98) * mm, "end": v(58.77, -4.93) * mm});
            skLineSegment(sketch, "E279", {"start": v(58.77, -4.93) * mm, "end": v(58.33, -5.1) * mm});
            skLineSegment(sketch, "E280", {"start": v(58.33, -5.1) * mm, "end": v(56.25, -6) * mm});
            skLineSegment(sketch, "E281", {"start": v(56.25, -6) * mm, "end": v(52.72, -8.4) * mm});
            skLineSegment(sketch, "E282", {"start": v(52.72, -8.4) * mm, "end": v(52.05, -9) * mm});
            skLineSegment(sketch, "E283", {"start": v(52.05, -9) * mm, "end": v(49.49, -12.87) * mm});
            skLineSegment(sketch, "E284", {"start": v(47.03, -16.59) * mm, "end": v(46.6, -17.32) * mm});
            skLineSegment(sketch, "E285", {"start": v(46.6, -17.32) * mm, "end": v(42.87, -28.6) * mm});
            skLineSegment(sketch, "E286", {"start": v(42.87, -28.6) * mm, "end": v(42.74, -29.15) * mm});
            skLineSegment(sketch, "E287", {"start": v(42.74, -29.15) * mm, "end": v(42.43, -34.98) * mm});
            skLineSegment(sketch, "E288", {"start": v(42.43, -34.98) * mm, "end": v(43.64, -43.22) * mm});
            skLineSegment(sketch, "E289", {"start": v(43.64, -43.22) * mm, "end": v(43.8, -44.15) * mm});
            skLineSegment(sketch, "E290", {"start": v(43.8, -44.15) * mm, "end": v(43.88, -45.68) * mm});
            skLineSegment(sketch, "E291", {"start": v(43.88, -45.68) * mm, "end": v(44, -46.38) * mm});
            skLineSegment(sketch, "E292", {"start": v(44, -46.38) * mm, "end": v(44.97, -48.17) * mm});
            skLineSegment(sketch, "E293", {"start": v(44.97, -48.17) * mm, "end": v(45.7, -48.54) * mm});
            skLineSegment(sketch, "E294", {"start": v(45.7, -48.54) * mm, "end": v(46.13, -48.57) * mm});
            skLineSegment(sketch, "E295", {"start": v(46.13, -48.57) * mm, "end": v(46.75, -48.78) * mm});
            skLineSegment(sketch, "E296", {"start": v(46.75, -48.78) * mm, "end": v(46.84, -49.59) * mm});
            skLineSegment(sketch, "E297", {"start": v(46.84, -49.59) * mm, "end": v(46.12, -49.62) * mm});
            skLineSegment(sketch, "E298", {"start": v(46.12, -49.62) * mm, "end": v(44.13, -49.55) * mm});
            skLineSegment(sketch, "E299", {"start": v(44.13, -49.55) * mm, "end": v(43.85, -49.57) * mm});
            skLineSegment(sketch, "E300", {"start": v(43.85, -49.57) * mm, "end": v(41.74, -50.1) * mm});
            skLineSegment(sketch, "E301", {"start": v(41.74, -50.1) * mm, "end": v(40.38, -50.67) * mm});
            skLineSegment(sketch, "E302", {"start": v(40.38, -50.67) * mm, "end": v(38.26, -51.85) * mm});
            skLineSegment(sketch, "E303", {"start": v(38.26, -51.85) * mm, "end": v(37.94, -52.1) * mm});
            skLineSegment(sketch, "E304", {"start": v(37.94, -52.1) * mm, "end": v(37.24, -52.86) * mm});
            skLineSegment(sketch, "E305", {"start": v(37.24, -52.86) * mm, "end": v(36.27, -54.07) * mm});
            skLineSegment(sketch, "E306", {"start": v(36.27, -54.07) * mm, "end": v(35.24, -55.8) * mm});
            skLineSegment(sketch, "E307", {"start": v(35.24, -55.8) * mm, "end": v(34.94, -56.44) * mm});
            skLineSegment(sketch, "E308", {"start": v(34.94, -56.44) * mm, "end": v(34.39, -58) * mm});
            skLineSegment(sketch, "E309", {"start": v(34.39, -58) * mm, "end": v(34.28, -58.8) * mm});
            skLineSegment(sketch, "E310", {"start": v(34.28, -58.8) * mm, "end": v(34.51, -61.42) * mm});
            skLineSegment(sketch, "E311", {"start": v(34.51, -61.42) * mm, "end": v(34.55, -61.73) * mm});
            skLineSegment(sketch, "E312", {"start": v(34.55, -61.73) * mm, "end": v(35.69, -61.97) * mm});
            skLineSegment(sketch, "E313", {"start": v(-13.15, -59.87) * mm, "end": v(-13.12, -59.91) * mm});
            skLineSegment(sketch, "E314", {"start": v(-13.12, -59.91) * mm, "end": v(-12.87, -59.8) * mm});
            skLineSegment(sketch, "E315", {"start": v(-12.87, -59.8) * mm, "end": v(-8.54, -57.57) * mm});
            skLineSegment(sketch, "E316", {"start": v(-8.54, -57.57) * mm, "end": v(-7.57, -57.25) * mm});
            skLineSegment(sketch, "E317", {"start": v(-7.57, -57.25) * mm, "end": v(-6.32, -57.04) * mm});
            skLineSegment(sketch, "E318", {"start": v(-6.32, -57.04) * mm, "end": v(-6, -56.95) * mm});
            skLineSegment(sketch, "E319", {"start": v(-6, -56.95) * mm, "end": v(-5.02, -56.37) * mm});
            skLineSegment(sketch, "E320", {"start": v(-5.02, -56.37) * mm, "end": v(-4.84, -56.26) * mm});
            skLineSegment(sketch, "E321", {"start": v(4.87, -56.15) * mm, "end": v(6.18, -56.67) * mm});
            skLineSegment(sketch, "E322", {"start": v(6.18, -56.67) * mm, "end": v(6.52, -56.79) * mm});
            skLineSegment(sketch, "E323", {"start": v(6.52, -56.79) * mm, "end": v(9.7, -58.4) * mm});
            skLineSegment(sketch, "E324", {"start": v(9.7, -58.4) * mm, "end": v(11.43, -59.1) * mm});
            skLineSegment(sketch, "E325", {"start": v(11.43, -59.1) * mm, "end": v(12.83, -59.75) * mm});
            skLineSegment(sketch, "E326", {"start": v(12.83, -59.75) * mm, "end": v(13.88, -60.27) * mm});
            skLineSegment(sketch, "E327", {"start": v(13.88, -60.27) * mm, "end": v(15.9, -61.42) * mm});
            skLineSegment(sketch, "E328", {"start": v(15.9, -61.42) * mm, "end": v(16.72, -61.64) * mm});
            skLineSegment(sketch, "E329", {"start": v(16.72, -61.64) * mm, "end": v(23.14, -61.55) * mm});
            skLineSegment(sketch, "E330", {"start": v(23.14, -61.55) * mm, "end": v(23.92, -61.63) * mm});
            skLineSegment(sketch, "E331", {"start": v(23.92, -61.63) * mm, "end": v(25.65, -61.56) * mm});
            skLineSegment(sketch, "E332", {"start": v(25.65, -61.56) * mm, "end": v(27.48, -61.39) * mm});
            skLineSegment(sketch, "E333", {"start": v(27.48, -61.39) * mm, "end": v(27.92, -61.17) * mm});
            skLineSegment(sketch, "E334", {"start": v(27.92, -61.17) * mm, "end": v(28.5, -60.52) * mm});
            skLineSegment(sketch, "E335", {"start": v(28.5, -60.52) * mm, "end": v(29, -59.97) * mm});
            skLineSegment(sketch, "E336", {"start": v(29, -59.97) * mm, "end": v(29.28, -60.44) * mm});
            skLineSegment(sketch, "E337", {"start": v(29.28, -60.44) * mm, "end": v(29.35, -61.23) * mm});
            skLineSegment(sketch, "E338", {"start": v(29.35, -61.23) * mm, "end": v(29.6, -61.95) * mm});
            skLineSegment(sketch, "E339", {"start": v(29.6, -61.95) * mm, "end": v(30.07, -61.98) * mm});
            skLineSegment(sketch, "E340", {"start": v(30.07, -61.98) * mm, "end": v(30.66, -60.93) * mm});
            skLineSegment(sketch, "E341", {"start": v(30.66, -60.93) * mm, "end": v(30.72, -60.71) * mm});
            skLineSegment(sketch, "E342", {"start": v(30.72, -60.71) * mm, "end": v(31.18, -57.79) * mm});
            skLineSegment(sketch, "E343", {"start": v(31.18, -57.79) * mm, "end": v(31.17, -57.57) * mm});
            skLineSegment(sketch, "E344", {"start": v(31.17, -57.57) * mm, "end": v(30.6, -56.6) * mm});
            skLineSegment(sketch, "E345", {"start": v(30.6, -56.6) * mm, "end": v(30.52, -56.5) * mm});
            skLineSegment(sketch, "E346", {"start": v(30.52, -56.5) * mm, "end": v(29.82, -55.4) * mm});
            skLineSegment(sketch, "E347", {"start": v(29.82, -55.4) * mm, "end": v(29.23, -54.76) * mm});
            skLineSegment(sketch, "E348", {"start": v(29.23, -54.76) * mm, "end": v(20.24, -52.7) * mm});
            skLineSegment(sketch, "E349", {"start": v(20.24, -52.7) * mm, "end": v(19.24, -52.44) * mm});
            skLineSegment(sketch, "E350", {"start": v(19.24, -52.44) * mm, "end": v(17.59, -52.33) * mm});
            skLineSegment(sketch, "E351", {"start": v(17.59, -52.33) * mm, "end": v(13.44, -51.84) * mm});
            skLineSegment(sketch, "E352", {"start": v(13.44, -51.84) * mm, "end": v(13.11, -51.8) * mm});
            skLineSegment(sketch, "E353", {"start": v(13.11, -51.8) * mm, "end": v(7.32, -50.01) * mm});
            skLineSegment(sketch, "E354", {"start": v(7.32, -50.01) * mm, "end": v(6.48, -50.12) * mm});
            skLineSegment(sketch, "E355", {"start": v(6.48, -50.12) * mm, "end": v(3.67, -50.72) * mm});
            skLineSegment(sketch, "E356", {"start": v(3.67, -50.72) * mm, "end": v(2.74, -50.82) * mm});
            skLineSegment(sketch, "E357", {"start": v(-4.88, -53.92) * mm, "end": v(-4.9, -53.94) * mm});
            skLineSegment(sketch, "E358", {"start": v(-4.9, -53.94) * mm, "end": v(-7.2, -55.67) * mm});
            skLineSegment(sketch, "E359", {"start": v(-7.2, -55.67) * mm, "end": v(-12.82, -59.56) * mm});
            skLineSegment(sketch, "E360", {"start": v(-12.82, -59.56) * mm, "end": v(-13.15, -59.87) * mm});
            skLineSegment(sketch, "E361", {"start": v(57.09, -31.17) * mm, "end": v(57.08, -31.56) * mm});
            skLineSegment(sketch, "E362", {"start": v(57.08, -31.56) * mm, "end": v(57.88, -38.14) * mm});
            skLineSegment(sketch, "E363", {"start": v(57.88, -38.14) * mm, "end": v(57.88, -38.92) * mm});
            skLineSegment(sketch, "E364", {"start": v(57.88, -38.92) * mm, "end": v(57.1, -42.3) * mm});
            skLineSegment(sketch, "E365", {"start": v(57.1, -42.3) * mm, "end": v(56.73, -43.1) * mm});
            skLineSegment(sketch, "E366", {"start": v(56.73, -43.1) * mm, "end": v(56.12, -43.92) * mm});
            skLineSegment(sketch, "E367", {"start": v(56.12, -43.92) * mm, "end": v(55.9, -44.43) * mm});
            skLineSegment(sketch, "E368", {"start": v(55.9, -44.43) * mm, "end": v(55.78, -45.95) * mm});
            skLineSegment(sketch, "E369", {"start": v(55.78, -45.95) * mm, "end": v(55.9, -46.5) * mm});
            skLineSegment(sketch, "E370", {"start": v(55.9, -46.5) * mm, "end": v(56.58, -47.3) * mm});
            skLineSegment(sketch, "E371", {"start": v(56.58, -47.3) * mm, "end": v(57, -46.7) * mm});
            skLineSegment(sketch, "E372", {"start": v(57, -46.7) * mm, "end": v(57.59, -44.83) * mm});
            skLineSegment(sketch, "E373", {"start": v(57.59, -44.83) * mm, "end": v(58.33, -43.27) * mm});
            skLineSegment(sketch, "E374", {"start": v(58.33, -43.27) * mm, "end": v(58.75, -42.34) * mm});
            skLineSegment(sketch, "E375", {"start": v(58.75, -42.34) * mm, "end": v(59.37, -40.62) * mm});
            skLineSegment(sketch, "E376", {"start": v(59.37, -40.62) * mm, "end": v(59.45, -40.27) * mm});
            skLineSegment(sketch, "E377", {"start": v(59.45, -40.27) * mm, "end": v(59.84, -37.5) * mm});
            skLineSegment(sketch, "E378", {"start": v(59.84, -37.5) * mm, "end": v(59.73, -36.29) * mm});
            skLineSegment(sketch, "E379", {"start": v(59.73, -36.29) * mm, "end": v(58.85, -31.3) * mm});
            skLineSegment(sketch, "E380", {"start": v(58.85, -31.3) * mm, "end": v(58.65, -27.96) * mm});
            skLineSegment(sketch, "E381", {"start": v(58.65, -27.96) * mm, "end": v(57.8, -20.2) * mm});
            skLineSegment(sketch, "E382", {"start": v(57.8, -20.2) * mm, "end": v(57.78, -19.38) * mm});
            skLineSegment(sketch, "E383", {"start": v(57.78, -19.38) * mm, "end": v(59.59, -8.12) * mm});
            skLineSegment(sketch, "E384", {"start": v(59.59, -8.12) * mm, "end": v(59.72, -7.5) * mm});
            skLineSegment(sketch, "E385", {"start": v(59.72, -7.5) * mm, "end": v(60.1, -6.02) * mm});
            skLineSegment(sketch, "E386", {"start": v(60.1, -6.02) * mm, "end": v(60.12, -5.63) * mm});
            skLineSegment(sketch, "E387", {"start": v(60.12, -5.63) * mm, "end": v(60.01, -5.79) * mm});
            skLineSegment(sketch, "E388", {"start": v(60.01, -5.79) * mm, "end": v(59.14, -8) * mm});
            skLineSegment(sketch, "E389", {"start": v(59.14, -8) * mm, "end": v(58.73, -9.18) * mm});
            skLineSegment(sketch, "E390", {"start": v(58.73, -9.18) * mm, "end": v(58.48, -9.74) * mm});
            skLineSegment(sketch, "E391", {"start": v(58.48, -9.74) * mm, "end": v(58.06, -11.13) * mm});
            skLineSegment(sketch, "E392", {"start": v(58.06, -11.13) * mm, "end": v(57.83, -12.04) * mm});
            skLineSegment(sketch, "E393", {"start": v(57.83, -12.04) * mm, "end": v(56.72, -14.64) * mm});
            skLineSegment(sketch, "E394", {"start": v(56.34, -19.95) * mm, "end": v(56.34, -20.29) * mm});
            skLineSegment(sketch, "E395", {"start": v(56.34, -20.29) * mm, "end": v(56.25, -21.58) * mm});
            skLineSegment(sketch, "E396", {"start": v(56.25, -21.58) * mm, "end": v(56.37, -24.08) * mm});
            skLineSegment(sketch, "E397", {"start": v(56.37, -24.08) * mm, "end": v(56.5, -24.9) * mm});
            skLineSegment(sketch, "E398", {"start": v(56.5, -24.9) * mm, "end": v(57.02, -27.7) * mm});
            skLineSegment(sketch, "E399", {"start": v(57.02, -27.7) * mm, "end": v(57.07, -28.28) * mm});
            skLineSegment(sketch, "E400", {"start": v(57.07, -28.28) * mm, "end": v(57, -29.77) * mm});
            skLineSegment(sketch, "E401", {"start": v(57, -29.77) * mm, "end": v(56.66, -30.3) * mm});
            skLineSegment(sketch, "E402", {"start": v(56.66, -30.3) * mm, "end": v(55.86, -30.93) * mm});
            skLineSegment(sketch, "E403", {"start": v(55.86, -30.93) * mm, "end": v(57.09, -31.17) * mm});
            skLineSegment(sketch, "E404", {"start": v(29.23, -68.98) * mm, "end": v(29.08, -68.83) * mm});
            skLineSegment(sketch, "E405", {"start": v(29.08, -68.83) * mm, "end": v(27.93, -67.8) * mm});
            skLineSegment(sketch, "E406", {"start": v(27.93, -67.8) * mm, "end": v(27.32, -67.5) * mm});
            skLineSegment(sketch, "E407", {"start": v(27.32, -67.5) * mm, "end": v(24.97, -67.2) * mm});
            skLineSegment(sketch, "E408", {"start": v(24.97, -67.2) * mm, "end": v(24.16, -67.16) * mm});
            skLineSegment(sketch, "E409", {"start": v(24.16, -67.16) * mm, "end": v(23.83, -67.11) * mm});
            skLineSegment(sketch, "E410", {"start": v(23.83, -67.11) * mm, "end": v(19.12, -67.32) * mm});
            skLineSegment(sketch, "E411", {"start": v(19.12, -67.32) * mm, "end": v(18.37, -67.2) * mm});
            skLineSegment(sketch, "E412", {"start": v(18.37, -67.2) * mm, "end": v(17.4, -67) * mm});
            skLineSegment(sketch, "E413", {"start": v(17.4, -67) * mm, "end": v(14.07, -65.37) * mm});
            skLineSegment(sketch, "E414", {"start": v(14.07, -65.37) * mm, "end": v(13.55, -64.99) * mm});
            skLineSegment(sketch, "E415", {"start": v(13.55, -64.99) * mm, "end": v(12.76, -62.87) * mm});
            skLineSegment(sketch, "E416", {"start": v(12.76, -62.87) * mm, "end": v(12.68, -62.63) * mm});
            skLineSegment(sketch, "E417", {"start": v(12.68, -62.63) * mm, "end": v(12.03, -64.56) * mm});
            skLineSegment(sketch, "E418", {"start": v(12.03, -64.56) * mm, "end": v(11.88, -64.54) * mm});
            skLineSegment(sketch, "E419", {"start": v(11.88, -64.54) * mm, "end": v(10.64, -64.15) * mm});
            skLineSegment(sketch, "E420", {"start": v(10.64, -64.15) * mm, "end": v(8.5, -63.26) * mm});
            skLineSegment(sketch, "E421", {"start": v(8.5, -63.26) * mm, "end": v(6.72, -62.57) * mm});
            skLineSegment(sketch, "E422", {"start": v(6.72, -62.57) * mm, "end": v(3.41, -61.65) * mm});
            skLineSegment(sketch, "E423", {"start": v(3.41, -61.65) * mm, "end": v(1.26, -61.02) * mm});
            skLineSegment(sketch, "E424", {"start": v(1.26, -61.02) * mm, "end": v(-3.78, -59.17) * mm});
            skLineSegment(sketch, "E425", {"start": v(-3.78, -59.17) * mm, "end": v(-4.71, -59.05) * mm});
            skLineSegment(sketch, "E426", {"start": v(-4.71, -59.05) * mm, "end": v(-6.38, -59.68) * mm});
            skLineSegment(sketch, "E427", {"start": v(-6.38, -59.68) * mm, "end": v(-7.34, -59.77) * mm});
            skLineSegment(sketch, "E428", {"start": v(-7.34, -59.77) * mm, "end": v(-10.5, -59.65) * mm});
            skLineSegment(sketch, "E429", {"start": v(-10.5, -59.65) * mm, "end": v(-10.95, -59.73) * mm});
            skLineSegment(sketch, "E430", {"start": v(-10.95, -59.73) * mm, "end": v(-9.47, -60.08) * mm});
            skLineSegment(sketch, "E431", {"start": v(-9.47, -60.08) * mm, "end": v(-4.7, -60.78) * mm});
            skLineSegment(sketch, "E432", {"start": v(-4.7, -60.78) * mm, "end": v(1.18, -62.5) * mm});
            skLineSegment(sketch, "E433", {"start": v(1.18, -62.5) * mm, "end": v(4.74, -63.68) * mm});
            skLineSegment(sketch, "E434", {"start": v(4.74, -63.68) * mm, "end": v(6.37, -64.17) * mm});
            skLineSegment(sketch, "E435", {"start": v(6.37, -64.17) * mm, "end": v(8.59, -64.93) * mm});
            skLineSegment(sketch, "E436", {"start": v(8.59, -64.93) * mm, "end": v(10.65, -65.94) * mm});
            skLineSegment(sketch, "E437", {"start": v(10.65, -65.94) * mm, "end": v(11.73, -66.45) * mm});
            skLineSegment(sketch, "E438", {"start": v(11.73, -66.45) * mm, "end": v(15, -68.1) * mm});
            skLineSegment(sketch, "E439", {"start": v(15, -68.1) * mm, "end": v(18.58, -69.79) * mm});
            skLineSegment(sketch, "E440", {"start": v(18.58, -69.79) * mm, "end": v(21.32, -69.15) * mm});
            skLineSegment(sketch, "E441", {"start": v(21.32, -69.15) * mm, "end": v(23.04, -69.6) * mm});
            skLineSegment(sketch, "E442", {"start": v(23.04, -69.6) * mm, "end": v(24.38, -69.77) * mm});
            skLineSegment(sketch, "E443", {"start": v(24.38, -69.77) * mm, "end": v(28.77, -69.02) * mm});
            skLineSegment(sketch, "E444", {"start": v(28.77, -69.02) * mm, "end": v(29.23, -68.98) * mm});
            skLineSegment(sketch, "E445", {"start": v(49.2, -63) * mm, "end": v(48.73, -63.06) * mm});
            skLineSegment(sketch, "E446", {"start": v(48.73, -63.06) * mm, "end": v(48.1, -63.26) * mm});
            skLineSegment(sketch, "E447", {"start": v(48.1, -63.26) * mm, "end": v(47.52, -63.81) * mm});
            skLineSegment(sketch, "E448", {"start": v(47.52, -63.81) * mm, "end": v(47.07, -64.5) * mm});
            skLineSegment(sketch, "E449", {"start": v(47.07, -64.5) * mm, "end": v(46.77, -65.28) * mm});
            skLineSegment(sketch, "E450", {"start": v(46.77, -65.28) * mm, "end": v(46.72, -65.38) * mm});
            skLineSegment(sketch, "E451", {"start": v(46.72, -65.38) * mm, "end": v(46.2, -65.22) * mm});
            skLineSegment(sketch, "E452", {"start": v(46.2, -65.22) * mm, "end": v(45.4, -66.31) * mm});
            skLineSegment(sketch, "E453", {"start": v(45.4, -66.31) * mm, "end": v(45.42, -66.72) * mm});
            skLineSegment(sketch, "E454", {"start": v(45.42, -66.72) * mm, "end": v(46.43, -68.09) * mm});
            skLineSegment(sketch, "E455", {"start": v(46.43, -68.09) * mm, "end": v(46.7, -68.36) * mm});
            skLineSegment(sketch, "E456", {"start": v(46.7, -68.36) * mm, "end": v(46.8, -68.23) * mm});
            skLineSegment(sketch, "E457", {"start": v(46.8, -68.23) * mm, "end": v(47.74, -66.97) * mm});
            skLineSegment(sketch, "E458", {"start": v(47.74, -66.97) * mm, "end": v(47.89, -66.74) * mm});
            skLineSegment(sketch, "E459", {"start": v(47.89, -66.74) * mm, "end": v(48.14, -66.28) * mm});
            skLineSegment(sketch, "E460", {"start": v(48.14, -66.28) * mm, "end": v(48.62, -66.54) * mm});
            skLineSegment(sketch, "E461", {"start": v(48.62, -66.54) * mm, "end": v(49.09, -66.49) * mm});
            skLineSegment(sketch, "E462", {"start": v(49.09, -66.49) * mm, "end": v(49.57, -65.97) * mm});
            skLineSegment(sketch, "E463", {"start": v(49.57, -65.97) * mm, "end": v(50.47, -64.74) * mm});
            skLineSegment(sketch, "E464", {"start": v(50.47, -64.74) * mm, "end": v(50.65, -64.32) * mm});
            skLineSegment(sketch, "E465", {"start": v(50.65, -64.32) * mm, "end": v(50.78, -63.69) * mm});
            skLineSegment(sketch, "E466", {"start": v(50.78, -63.69) * mm, "end": v(51.41, -63.86) * mm});
            skLineSegment(sketch, "E467", {"start": v(51.41, -63.86) * mm, "end": v(51.7, -63.7) * mm});
            skLineSegment(sketch, "E468", {"start": v(51.7, -63.7) * mm, "end": v(52.38, -63) * mm});
            skLineSegment(sketch, "E469", {"start": v(52.38, -63) * mm, "end": v(52.87, -62.5) * mm});
            skLineSegment(sketch, "E470", {"start": v(52.87, -62.5) * mm, "end": v(51.53, -61.54) * mm});
            skLineSegment(sketch, "E471", {"start": v(51.53, -61.54) * mm, "end": v(50.28, -60.64) * mm});
            skLineSegment(sketch, "E472", {"start": v(50.28, -60.64) * mm, "end": v(49.58, -61.52) * mm});
            skLineSegment(sketch, "E473", {"start": v(49.58, -61.52) * mm, "end": v(48.87, -62.43) * mm});
            skLineSegment(sketch, "E474", {"start": v(48.87, -62.43) * mm, "end": v(49.2, -63) * mm});
            skLineSegment(sketch, "E475", {"start": v(28.1, -65.24) * mm, "end": v(29.02, -66.19) * mm});
            skLineSegment(sketch, "E476", {"start": v(29.02, -66.19) * mm, "end": v(30.23, -67.13) * mm});
            skLineSegment(sketch, "E477", {"start": v(30.23, -67.13) * mm, "end": v(30.48, -67.37) * mm});
            skLineSegment(sketch, "E478", {"start": v(30.48, -67.37) * mm, "end": v(30.85, -67.92) * mm});
            skLineSegment(sketch, "E479", {"start": v(30.85, -67.92) * mm, "end": v(31.2, -68.17) * mm});
            skLineSegment(sketch, "E480", {"start": v(31.2, -68.17) * mm, "end": v(32.42, -68.55) * mm});
            skLineSegment(sketch, "E481", {"start": v(32.42, -68.55) * mm, "end": v(32.58, -68.63) * mm});
            skLineSegment(sketch, "E482", {"start": v(32.58, -68.63) * mm, "end": v(33.4, -69.46) * mm});
            skLineSegment(sketch, "E483", {"start": v(33.4, -69.46) * mm, "end": v(33.89, -69.9) * mm});
            skLineSegment(sketch, "E484", {"start": v(33.89, -69.9) * mm, "end": v(34.22, -69.99) * mm});
            skLineSegment(sketch, "E485", {"start": v(34.22, -69.99) * mm, "end": v(36.13, -69.93) * mm});
            skLineSegment(sketch, "E486", {"start": v(36.13, -69.93) * mm, "end": v(36.45, -69.96) * mm});
            skLineSegment(sketch, "E487", {"start": v(36.45, -69.96) * mm, "end": v(37.36, -70.21) * mm});
            skLineSegment(sketch, "E488", {"start": v(37.36, -70.21) * mm, "end": v(37.82, -70.18) * mm});
            skLineSegment(sketch, "E489", {"start": v(37.82, -70.18) * mm, "end": v(39.08, -69.92) * mm});
            skLineSegment(sketch, "E490", {"start": v(39.08, -69.92) * mm, "end": v(40.07, -69.74) * mm});
            skLineSegment(sketch, "E491", {"start": v(40.07, -69.74) * mm, "end": v(40.22, -69.64) * mm});
            skLineSegment(sketch, "E492", {"start": v(40.22, -69.64) * mm, "end": v(39.99, -69.48) * mm});
            skLineSegment(sketch, "E493", {"start": v(39.99, -69.48) * mm, "end": v(38.35, -68.5) * mm});
            skLineSegment(sketch, "E494", {"start": v(38.35, -68.5) * mm, "end": v(37.69, -68.25) * mm});
            skLineSegment(sketch, "E495", {"start": v(37.69, -68.25) * mm, "end": v(33.43, -67.44) * mm});
            skLineSegment(sketch, "E496", {"start": v(33.43, -67.44) * mm, "end": v(33.1, -67.33) * mm});
            skLineSegment(sketch, "E497", {"start": v(33.1, -67.33) * mm, "end": v(30.7, -66.22) * mm});
            skLineSegment(sketch, "E498", {"start": v(30.7, -66.22) * mm, "end": v(30.43, -66.06) * mm});
            skLineSegment(sketch, "E499", {"start": v(30.43, -66.06) * mm, "end": v(28.8, -64.88) * mm});
            skLineSegment(sketch, "E500", {"start": v(28.8, -64.88) * mm, "end": v(28.48, -64.66) * mm});
            skLineSegment(sketch, "E501", {"start": v(28.48, -64.66) * mm, "end": v(28.1, -65.24) * mm});
            skLineSegment(sketch, "E502", {"start": v(56.02, -53.95) * mm, "end": v(55.72, -53.32) * mm});
            skLineSegment(sketch, "E503", {"start": v(55.72, -53.32) * mm, "end": v(55.72, -52.92) * mm});
            skLineSegment(sketch, "E504", {"start": v(55.72, -52.92) * mm, "end": v(56.16, -51.67) * mm});
            skLineSegment(sketch, "E505", {"start": v(56.16, -51.67) * mm, "end": v(56.12, -51.37) * mm});
            skLineSegment(sketch, "E506", {"start": v(56.12, -51.37) * mm, "end": v(55.86, -50.53) * mm});
            skLineSegment(sketch, "E507", {"start": v(55.86, -50.53) * mm, "end": v(55.43, -49.6) * mm});
            skLineSegment(sketch, "E508", {"start": v(55.43, -49.6) * mm, "end": v(55.18, -49.25) * mm});
            skLineSegment(sketch, "E509", {"start": v(55.18, -49.25) * mm, "end": v(54.55, -48) * mm});
            skLineSegment(sketch, "E510", {"start": v(54.55, -48) * mm, "end": v(54.07, -47.39) * mm});
            skLineSegment(sketch, "E511", {"start": v(54.07, -47.39) * mm, "end": v(53.28, -46.46) * mm});
            skLineSegment(sketch, "E512", {"start": v(53.28, -46.46) * mm, "end": v(53.01, -46.09) * mm});
            skLineSegment(sketch, "E513", {"start": v(53.01, -46.09) * mm, "end": v(52.85, -45.93) * mm});
            skLineSegment(sketch, "E514", {"start": v(52.85, -45.93) * mm, "end": v(51.88, -45.46) * mm});
            skLineSegment(sketch, "E515", {"start": v(51.88, -45.46) * mm, "end": v(52, -45.85) * mm});
            skLineSegment(sketch, "E516", {"start": v(52, -45.85) * mm, "end": v(52.62, -47.66) * mm});
            skLineSegment(sketch, "E517", {"start": v(52.62, -47.66) * mm, "end": v(53.53, -50.78) * mm});
            skLineSegment(sketch, "E518", {"start": v(53.53, -50.78) * mm, "end": v(54.17, -54.52) * mm});
            skLineSegment(sketch, "E519", {"start": v(54.17, -54.52) * mm, "end": v(54.27, -54.89) * mm});
            skLineSegment(sketch, "E520", {"start": v(54.27, -54.89) * mm, "end": v(54.9, -56.58) * mm});
            skLineSegment(sketch, "E521", {"start": v(54.9, -56.58) * mm, "end": v(55, -56.8) * mm});
            skLineSegment(sketch, "E522", {"start": v(55, -56.8) * mm, "end": v(56.02, -53.95) * mm});
            skLineSegment(sketch, "E523", {"start": v(56.77, -64.5) * mm, "end": v(56.77, -64.86) * mm});
            skLineSegment(sketch, "E524", {"start": v(56.77, -64.86) * mm, "end": v(56.81, -66.13) * mm});
            skLineSegment(sketch, "E525", {"start": v(56.81, -66.13) * mm, "end": v(56.73, -66.91) * mm});
            skLineSegment(sketch, "E526", {"start": v(56.73, -66.91) * mm, "end": v(56.44, -68.1) * mm});
            skLineSegment(sketch, "E527", {"start": v(56.44, -68.1) * mm, "end": v(56.37, -68.45) * mm});
            skLineSegment(sketch, "E528", {"start": v(56.37, -68.45) * mm, "end": v(56.46, -68.47) * mm});
            skLineSegment(sketch, "E529", {"start": v(56.46, -68.47) * mm, "end": v(58.88, -68.63) * mm});
            skLineSegment(sketch, "E530", {"start": v(58.88, -68.63) * mm, "end": v(59.18, -68.53) * mm});
            skLineSegment(sketch, "E531", {"start": v(59.18, -68.53) * mm, "end": v(61.07, -66.98) * mm});
            skLineSegment(sketch, "E532", {"start": v(61.07, -66.98) * mm, "end": v(61.22, -66.84) * mm});
            skLineSegment(sketch, "E533", {"start": v(61.22, -66.84) * mm, "end": v(61.16, -66.78) * mm});
            skLineSegment(sketch, "E534", {"start": v(61.16, -66.78) * mm, "end": v(56.77, -64.5) * mm});
            skLineSegment(sketch, "E535", {"start": v(44.45, -56.2) * mm, "end": v(45.16, -57.17) * mm});
            skLineSegment(sketch, "E536", {"start": v(45.16, -57.17) * mm, "end": v(46.1, -58.02) * mm});
            skLineSegment(sketch, "E537", {"start": v(46.1, -58.02) * mm, "end": v(46.82, -58.43) * mm});
            skLineSegment(sketch, "E538", {"start": v(46.82, -58.43) * mm, "end": v(46.25, -57.34) * mm});
            skLineSegment(sketch, "E539", {"start": v(46.25, -57.34) * mm, "end": v(46.67, -57.25) * mm});
            skLineSegment(sketch, "E540", {"start": v(46.67, -57.25) * mm, "end": v(46.9, -57.16) * mm});
            skLineSegment(sketch, "E541", {"start": v(46.9, -57.16) * mm, "end": v(47.3, -56.8) * mm});
            skLineSegment(sketch, "E542", {"start": v(47.3, -56.8) * mm, "end": v(47.41, -56.52) * mm});
            skLineSegment(sketch, "E543", {"start": v(47.41, -56.52) * mm, "end": v(47.36, -55.88) * mm});
            skLineSegment(sketch, "E544", {"start": v(47.36, -55.88) * mm, "end": v(47.14, -55.48) * mm});
            skLineSegment(sketch, "E545", {"start": v(47.14, -55.48) * mm, "end": v(46.6, -55.04) * mm});
            skLineSegment(sketch, "E546", {"start": v(46.6, -55.04) * mm, "end": v(47.55, -54.1) * mm});
            skLineSegment(sketch, "E547", {"start": v(47.55, -54.1) * mm, "end": v(47.85, -53.55) * mm});
            skLineSegment(sketch, "E548", {"start": v(47.85, -53.55) * mm, "end": v(47.85, -53.43) * mm});
            skLineSegment(sketch, "E549", {"start": v(47.85, -53.43) * mm, "end": v(47.54, -53) * mm});
            skLineSegment(sketch, "E550", {"start": v(47.54, -53) * mm, "end": v(46.47, -53.77) * mm});
            skLineSegment(sketch, "E551", {"start": v(46.47, -53.77) * mm, "end": v(45.3, -54.8) * mm});
            skLineSegment(sketch, "E552", {"start": v(45.3, -54.8) * mm, "end": v(44.45, -56.2) * mm});
            skLineSegment(sketch, "E553", {"start": v(40.06, -59.38) * mm, "end": v(39.78, -59.56) * mm});
            skLineSegment(sketch, "E554", {"start": v(39.78, -59.56) * mm, "end": v(38.58, -60.47) * mm});
            skLineSegment(sketch, "E555", {"start": v(38.58, -60.47) * mm, "end": v(38.14, -60.91) * mm});
            skLineSegment(sketch, "E556", {"start": v(38.14, -60.91) * mm, "end": v(37.32, -61.78) * mm});
            skLineSegment(sketch, "E557", {"start": v(37.32, -61.78) * mm, "end": v(37.01, -62.7) * mm});
            skLineSegment(sketch, "E558", {"start": v(37.01, -62.7) * mm, "end": v(37.7, -63.64) * mm});
            skLineSegment(sketch, "E559", {"start": v(37.7, -63.64) * mm, "end": v(38.7, -64.49) * mm});
            skLineSegment(sketch, "E560", {"start": v(38.7, -64.49) * mm, "end": v(39.31, -64.85) * mm});
            skLineSegment(sketch, "E561", {"start": v(39.31, -64.85) * mm, "end": v(38.75, -63.75) * mm});
            skLineSegment(sketch, "E562", {"start": v(38.75, -63.75) * mm, "end": v(39.45, -63.57) * mm});
            skLineSegment(sketch, "E563", {"start": v(39.45, -63.57) * mm, "end": v(39.8, -63.18) * mm});
            skLineSegment(sketch, "E564", {"start": v(39.8, -63.18) * mm, "end": v(39.9, -62.65) * mm});
            skLineSegment(sketch, "E565", {"start": v(39.9, -62.65) * mm, "end": v(39.77, -62.22) * mm});
            skLineSegment(sketch, "E566", {"start": v(39.77, -62.22) * mm, "end": v(39.13, -61.4) * mm});
            skLineSegment(sketch, "E567", {"start": v(39.13, -61.4) * mm, "end": v(39.33, -61.2) * mm});
            skLineSegment(sketch, "E568", {"start": v(39.33, -61.2) * mm, "end": v(40.11, -60.44) * mm});
            skLineSegment(sketch, "E569", {"start": v(40.11, -60.44) * mm, "end": v(40.24, -59.85) * mm});
            skLineSegment(sketch, "E570", {"start": v(40.24, -59.85) * mm, "end": v(40.06, -59.38) * mm});
            skLineSegment(sketch, "E571", {"start": v(48.01, -61.22) * mm, "end": v(47.48, -60.7) * mm});
            skLineSegment(sketch, "E572", {"start": v(47.48, -60.7) * mm, "end": v(47, -60.46) * mm});
            skLineSegment(sketch, "E573", {"start": v(47, -60.46) * mm, "end": v(46.4, -60.33) * mm});
            skLineSegment(sketch, "E574", {"start": v(46.4, -60.33) * mm, "end": v(45.88, -60.47) * mm});
            skLineSegment(sketch, "E575", {"start": v(45.88, -60.47) * mm, "end": v(45.28, -61.05) * mm});
            skLineSegment(sketch, "E576", {"start": v(45.28, -61.05) * mm, "end": v(44.72, -61.68) * mm});
            skLineSegment(sketch, "E577", {"start": v(44.72, -61.68) * mm, "end": v(44.4, -62.51) * mm});
            skLineSegment(sketch, "E578", {"start": v(44.4, -62.51) * mm, "end": v(44.58, -63.38) * mm});
            skLineSegment(sketch, "E579", {"start": v(44.58, -63.38) * mm, "end": v(44.68, -63.48) * mm});
            skLineSegment(sketch, "E580", {"start": v(44.68, -63.48) * mm, "end": v(45.24, -63.67) * mm});
            skLineSegment(sketch, "E581", {"start": v(45.24, -63.67) * mm, "end": v(45.89, -63.36) * mm});
            skLineSegment(sketch, "E582", {"start": v(45.89, -63.36) * mm, "end": v(46.43, -63.06) * mm});
            skLineSegment(sketch, "E583", {"start": v(46.43, -63.06) * mm, "end": v(47.15, -62.66) * mm});
            skLineSegment(sketch, "E584", {"start": v(47.15, -62.66) * mm, "end": v(48.01, -61.22) * mm});
            skLineSegment(sketch, "E585", {"start": v(56.87, -70.72) * mm, "end": v(56.58, -70.63) * mm});
            skLineSegment(sketch, "E586", {"start": v(56.58, -70.63) * mm, "end": v(54.8, -70.18) * mm});
            skLineSegment(sketch, "E587", {"start": v(54.8, -70.18) * mm, "end": v(54.5, -70.14) * mm});
            skLineSegment(sketch, "E588", {"start": v(54.5, -70.14) * mm, "end": v(53.84, -70.2) * mm});
            skLineSegment(sketch, "E589", {"start": v(53.84, -70.2) * mm, "end": v(53.3, -70.49) * mm});
            skLineSegment(sketch, "E590", {"start": v(53.3, -70.49) * mm, "end": v(53.25, -70.58) * mm});
            skLineSegment(sketch, "E591", {"start": v(53.25, -70.58) * mm, "end": v(53.25, -71.25) * mm});
            skLineSegment(sketch, "E592", {"start": v(53.25, -71.25) * mm, "end": v(53.77, -73.4) * mm});
            skLineSegment(sketch, "E593", {"start": v(53.77, -73.4) * mm, "end": v(53.8, -73.44) * mm});
            skLineSegment(sketch, "E594", {"start": v(53.8, -73.44) * mm, "end": v(54.18, -73.04) * mm});
            skLineSegment(sketch, "E595", {"start": v(54.18, -73.04) * mm, "end": v(54.95, -72.35) * mm});
            skLineSegment(sketch, "E596", {"start": v(54.95, -72.35) * mm, "end": v(56, -71.79) * mm});
            skLineSegment(sketch, "E597", {"start": v(56, -71.79) * mm, "end": v(56.15, -71.69) * mm});
            skLineSegment(sketch, "E598", {"start": v(56.15, -71.69) * mm, "end": v(56.87, -70.72) * mm});
            skLineSegment(sketch, "E599", {"start": v(49.27, -72.56) * mm, "end": v(49.37, -74.3) * mm});
            skLineSegment(sketch, "E600", {"start": v(49.37, -74.3) * mm, "end": v(49.59, -76.06) * mm});
            skLineSegment(sketch, "E601", {"start": v(49.59, -76.06) * mm, "end": v(51.22, -74.78) * mm});
            skLineSegment(sketch, "E602", {"start": v(51.22, -74.78) * mm, "end": v(51.33, -74.51) * mm});
            skLineSegment(sketch, "E603", {"start": v(51.33, -74.51) * mm, "end": v(51.5, -72.79) * mm});
            skLineSegment(sketch, "E604", {"start": v(51.5, -72.79) * mm, "end": v(51.5, -72.55) * mm});
            skLineSegment(sketch, "E605", {"start": v(51.5, -72.55) * mm, "end": v(49.27, -72.56) * mm});
            skLineSegment(sketch, "E606", {"start": v(48.9, -54.27) * mm, "end": v(48.85, -54.29) * mm});
            skLineSegment(sketch, "E607", {"start": v(48.85, -54.29) * mm, "end": v(48.84, -54.56) * mm});
            skLineSegment(sketch, "E608", {"start": v(48.84, -54.56) * mm, "end": v(48.87, -55.37) * mm});
            skLineSegment(sketch, "E609", {"start": v(48.87, -55.37) * mm, "end": v(48.6, -57.19) * mm});
            skLineSegment(sketch, "E610", {"start": v(48.6, -57.19) * mm, "end": v(48.06, -58.15) * mm});
            skLineSegment(sketch, "E611", {"start": v(48.06, -58.15) * mm, "end": v(47.87, -58.82) * mm});
            skLineSegment(sketch, "E612", {"start": v(47.87, -58.82) * mm, "end": v(48.52, -58.87) * mm});
            skLineSegment(sketch, "E613", {"start": v(48.52, -58.87) * mm, "end": v(48.7, -58.81) * mm});
            skLineSegment(sketch, "E614", {"start": v(48.7, -58.81) * mm, "end": v(49.56, -58.25) * mm});
            skLineSegment(sketch, "E615", {"start": v(49.56, -58.25) * mm, "end": v(49.69, -58.07) * mm});
            skLineSegment(sketch, "E616", {"start": v(49.69, -58.07) * mm, "end": v(49.93, -56.85) * mm});
            skLineSegment(sketch, "E617", {"start": v(49.93, -56.85) * mm, "end": v(49.9, -56.3) * mm});
            skLineSegment(sketch, "E618", {"start": v(49.9, -56.3) * mm, "end": v(49.7, -55.6) * mm});
            skLineSegment(sketch, "E619", {"start": v(49.7, -55.6) * mm, "end": v(48.9, -54.27) * mm});
            skLineSegment(sketch, "E620", {"start": v(41.77, -60.6) * mm, "end": v(41.69, -60.6) * mm});
            skLineSegment(sketch, "E621", {"start": v(41.69, -60.6) * mm, "end": v(41.71, -60.77) * mm});
            skLineSegment(sketch, "E622", {"start": v(41.71, -60.77) * mm, "end": v(41.56, -62.88) * mm});
            skLineSegment(sketch, "E623", {"start": v(41.56, -62.88) * mm, "end": v(41.45, -63.34) * mm});
            skLineSegment(sketch, "E624", {"start": v(41.45, -63.34) * mm, "end": v(41.15, -63.9) * mm});
            skLineSegment(sketch, "E625", {"start": v(41.15, -63.9) * mm, "end": v(40.91, -64.07) * mm});
            skLineSegment(sketch, "E626", {"start": v(40.91, -64.07) * mm, "end": v(40.52, -64.16) * mm});
            skLineSegment(sketch, "E627", {"start": v(40.52, -64.16) * mm, "end": v(40.36, -64.95) * mm});
            skLineSegment(sketch, "E628", {"start": v(40.36, -64.95) * mm, "end": v(41.45, -64.95) * mm});
            skLineSegment(sketch, "E629", {"start": v(41.45, -64.95) * mm, "end": v(41.54, -64.92) * mm});
            skLineSegment(sketch, "E630", {"start": v(41.54, -64.92) * mm, "end": v(42.47, -64.02) * mm});
            skLineSegment(sketch, "E631", {"start": v(42.47, -64.02) * mm, "end": v(42.7, -63.17) * mm});
            skLineSegment(sketch, "E632", {"start": v(42.7, -63.17) * mm, "end": v(42.48, -62.2) * mm});
            skLineSegment(sketch, "E633", {"start": v(42.48, -62.2) * mm, "end": v(42.38, -61.96) * mm});
            skLineSegment(sketch, "E634", {"start": v(42.38, -61.96) * mm, "end": v(41.77, -60.6) * mm});
            skLineSegment(sketch, "E635", {"start": v(68.4, -60.3) * mm, "end": v(67.37, -59.5) * mm});
            skLineSegment(sketch, "E636", {"start": v(67.37, -59.5) * mm, "end": v(67.23, -59.45) * mm});
            skLineSegment(sketch, "E637", {"start": v(67.23, -59.45) * mm, "end": v(66.6, -59.38) * mm});
            skLineSegment(sketch, "E638", {"start": v(66.6, -59.38) * mm, "end": v(66.27, -60.21) * mm});
            skLineSegment(sketch, "E639", {"start": v(66.27, -60.21) * mm, "end": v(66.32, -60.72) * mm});
            skLineSegment(sketch, "E640", {"start": v(66.32, -60.72) * mm, "end": v(66.88, -61.5) * mm});
            skLineSegment(sketch, "E641", {"start": v(66.88, -61.5) * mm, "end": v(67.01, -61.64) * mm});
            skLineSegment(sketch, "E642", {"start": v(67.01, -61.64) * mm, "end": v(68.4, -60.3) * mm});
            skLineSegment(sketch, "E643", {"start": v(69.96, -58.8) * mm, "end": v(69.87, -58.72) * mm});
            skLineSegment(sketch, "E644", {"start": v(69.87, -58.72) * mm, "end": v(68.86, -58.04) * mm});
            skLineSegment(sketch, "E645", {"start": v(68.86, -58.04) * mm, "end": v(68.3, -57.95) * mm});
            skLineSegment(sketch, "E646", {"start": v(68.3, -57.95) * mm, "end": v(68.08, -58.3) * mm});
            skLineSegment(sketch, "E647", {"start": v(68.08, -58.3) * mm, "end": v(68.06, -58.37) * mm});
            skLineSegment(sketch, "E648", {"start": v(68.06, -58.37) * mm, "end": v(68.08, -58.7) * mm});
            skLineSegment(sketch, "E649", {"start": v(68.08, -58.7) * mm, "end": v(68.35, -59.14) * mm});
            skLineSegment(sketch, "E650", {"start": v(68.35, -59.14) * mm, "end": v(68.9, -59.84) * mm});
            skLineSegment(sketch, "E651", {"start": v(68.9, -59.84) * mm, "end": v(69.96, -58.8) * mm});
            skLineSegment(sketch, "E652", {"start": v(51.2, -69.74) * mm, "end": v(48.9, -71.04) * mm});
            skLineSegment(sketch, "E653", {"start": v(48.9, -71.04) * mm, "end": v(50.12, -71.2) * mm});
            skLineSegment(sketch, "E654", {"start": v(50.12, -71.2) * mm, "end": v(51.37, -71.07) * mm});
            skLineSegment(sketch, "E655", {"start": v(51.37, -71.07) * mm, "end": v(51.2, -69.74) * mm});
            skLineSegment(sketch, "E656", {"start": v(42.65, -80.3) * mm, "end": v(42, -79.46) * mm});
            skLineSegment(sketch, "E657", {"start": v(42, -79.46) * mm, "end": v(41.33, -78.97) * mm});
            skLineSegment(sketch, "E658", {"start": v(41.33, -78.97) * mm, "end": v(41.24, -80.03) * mm});
            skLineSegment(sketch, "E659", {"start": v(41.24, -80.03) * mm, "end": v(41.49, -81.05) * mm});
            skLineSegment(sketch, "E660", {"start": v(41.49, -81.05) * mm, "end": v(42.65, -80.3) * mm});
            skLineSegment(sketch, "E661", {"start": v(43.28, -79.82) * mm, "end": v(44.89, -79.08) * mm});
            skLineSegment(sketch, "E662", {"start": v(44.89, -79.08) * mm, "end": v(43.84, -78.43) * mm});
            skLineSegment(sketch, "E663", {"start": v(43.84, -78.43) * mm, "end": v(43.6, -78.46) * mm});
            skLineSegment(sketch, "E664", {"start": v(43.6, -78.46) * mm, "end": v(43.04, -78.9) * mm});
            skLineSegment(sketch, "E665", {"start": v(43.04, -78.9) * mm, "end": v(43.28, -79.82) * mm});
            skLineSegment(sketch, "E666", {"start": v(54.4, -67.86) * mm, "end": v(54.45, -67.8) * mm});
            skLineSegment(sketch, "E667", {"start": v(54.45, -67.8) * mm, "end": v(55.01, -66.09) * mm});
            skLineSegment(sketch, "E668", {"start": v(55.01, -66.09) * mm, "end": v(55.16, -65.3) * mm});
            skLineSegment(sketch, "E669", {"start": v(55.16, -65.3) * mm, "end": v(53.77, -66.74) * mm});
            skLineSegment(sketch, "E670", {"start": v(53.77, -66.74) * mm, "end": v(54.4, -67.86) * mm});
            skLineSegment(sketch, "E671", {"start": v(39.81, -81.03) * mm, "end": v(39.98, -81.66) * mm});
            skLineSegment(sketch, "E672", {"start": v(39.98, -81.66) * mm, "end": v(40.7, -81.37) * mm});
            skLineSegment(sketch, "E673", {"start": v(40.7, -81.37) * mm, "end": v(40.28, -80.94) * mm});
            skLineSegment(sketch, "E674", {"start": v(40.28, -80.94) * mm, "end": v(39.81, -81.03) * mm});
            skLineSegment(sketch, "E675.0", {"start": v(0, 0) * mm, "end": v(-6.35, 102.95) * mm});
            skLineSegment(sketch, "E675.1", {"start": v(0, 0) * mm, "end": v(6.35, 102.95) * mm});
            skArc(sketch, "E675.2", {"start": v(-6.1, 99) * mm, "mid": v(-3.93, 99.81) * mm, "end": v(-2.58, 101.71) * mm});
            skArc(sketch, "E675.3", {"start": v(-1.4, 104.85) * mm, "mid": v(-2, 103.3) * mm, "end": v(-2.55, 101.74) * mm});
            skLineSegment(sketch, "E675.4", {"start": v(-6.35, 102.95) * mm, "end": v(-2.58, 101.71) * mm});
            skCircle(sketch, "E675.5", {"center": v(0, 0) * mm, "radius": 103.19 * mm});
            skArc(sketch, "E675.6", {"start": v(1.4, 104.85) * mm, "mid": v(0, 104.86) * mm, "end": v(-1.4, 104.85) * mm});
            skLineSegment(sketch, "E675.7", {"start": v(0, 0) * mm, "end": v(0, 116.9) * mm});
            skArc(sketch, "E675.8", {"start": v(-6.1, 99) * mm, "mid": v(-3.9, 99.82) * mm, "end": v(-2.55, 101.74) * mm});
            skArc(sketch, "E675.9", {"start": v(2.58, 101.71) * mm, "mid": v(3.93, 99.81) * mm, "end": v(6.1, 99) * mm});
            skArc(sketch, "E675.10", {"start": v(2.55, 101.74) * mm, "mid": v(3.9, 99.82) * mm, "end": v(6.1, 99) * mm});
            skArc(sketch, "E675.11", {"start": v(2.56, 101.7) * mm, "mid": v(2, 103.29) * mm, "end": v(1.4, 104.85) * mm});
            skLineSegment(sketch, "E675.12", {"start": v(6.35, 102.95) * mm, "end": v(2.56, 101.7) * mm});
            skArc(sketch, "E675.13", {"start": v(-18.22, 97.5) * mm, "mid": v(-16.14, 98.58) * mm, "end": v(-15.03, 100.65) * mm});
            skArc(sketch, "E675.14", {"start": v(-14.27, 103.88) * mm, "mid": v(-14.68, 102.27) * mm, "end": v(-15.03, 100.65) * mm});
            skArc(sketch, "E675.15", {"start": v(-11.5, 104.22) * mm, "mid": v(-12.89, 104.06) * mm, "end": v(-14.27, 103.88) * mm});
            skArc(sketch, "E675.16", {"start": v(-9.96, 101.25) * mm, "mid": v(-10.7, 102.75) * mm, "end": v(-11.5, 104.22) * mm});
            skArc(sketch, "E675.17", {"start": v(-9.98, 101.28) * mm, "mid": v(-8.4, 99.54) * mm, "end": v(-6.1, 99) * mm});
            skArc(sketch, "E675.18", {"start": v(-30.07, 94.51) * mm, "mid": v(-28.13, 95.85) * mm, "end": v(-27.28, 98.04) * mm});
            skArc(sketch, "E675.19", {"start": v(-26.93, 101.34) * mm, "mid": v(-27.14, 99.7) * mm, "end": v(-27.28, 98.04) * mm});
            skArc(sketch, "E675.20", {"start": v(-24.22, 102.02) * mm, "mid": v(-25.58, 101.69) * mm, "end": v(-26.93, 101.34) * mm});
            skArc(sketch, "E675.21", {"start": v(-22.33, 99.26) * mm, "mid": v(-23.25, 100.66) * mm, "end": v(-24.22, 102.02) * mm});
            skArc(sketch, "E675.22", {"start": v(-22.35, 99.29) * mm, "mid": v(-20.56, 97.76) * mm, "end": v(-18.22, 97.5) * mm});
            skArc(sketch, "E675.23", {"start": v(-41.45, 90.1) * mm, "mid": v(-39.7, 91.67) * mm, "end": v(-39.13, 93.95) * mm});
            skArc(sketch, "E675.24", {"start": v(-39.18, 97.26) * mm, "mid": v(-39.18, 95.6) * mm, "end": v(-39.13, 93.95) * mm});
            skArc(sketch, "E675.25", {"start": v(-36.57, 98.27) * mm, "mid": v(-37.88, 97.78) * mm, "end": v(-39.18, 97.26) * mm});
            skArc(sketch, "E675.26", {"start": v(-34.36, 95.76) * mm, "mid": v(-35.44, 97.04) * mm, "end": v(-36.57, 98.27) * mm});
            skArc(sketch, "E675.27", {"start": v(-34.38, 95.79) * mm, "mid": v(-32.42, 94.49) * mm, "end": v(-30.07, 94.51) * mm});
            skArc(sketch, "E675.28", {"start": v(-52.21, 84.33) * mm, "mid": v(-50.66, 86.1) * mm, "end": v(-50.37, 88.43) * mm});
            skArc(sketch, "E675.29", {"start": v(-50.83, 91.71) * mm, "mid": v(-50.63, 90.06) * mm, "end": v(-50.37, 88.43) * mm});
            skArc(sketch, "E675.30", {"start": v(-48.37, 93.03) * mm, "mid": v(-49.6, 92.38) * mm, "end": v(-50.83, 91.71) * mm});
            skArc(sketch, "E675.31", {"start": v(-45.86, 90.81) * mm, "mid": v(-47.1, 91.94) * mm, "end": v(-48.37, 93.03) * mm});
            skArc(sketch, "E675.32", {"start": v(-45.89, 90.84) * mm, "mid": v(-43.78, 89.79) * mm, "end": v(-41.45, 90.1) * mm});
            skArc(sketch, "E675.33", {"start": v(-62.18, 77.27) * mm, "mid": v(-60.86, 79.22) * mm, "end": v(-60.86, 81.57) * mm});
            skArc(sketch, "E675.34", {"start": v(-61.72, 84.77) * mm, "mid": v(-61.32, 83.16) * mm, "end": v(-60.86, 81.57) * mm});
            skArc(sketch, "E675.35", {"start": v(-59.44, 86.38) * mm, "mid": v(-60.58, 85.58) * mm, "end": v(-61.72, 84.77) * mm});
            skArc(sketch, "E675.36", {"start": v(-56.68, 84.49) * mm, "mid": v(-58.04, 85.46) * mm, "end": v(-59.44, 86.38) * mm});
            skArc(sketch, "E675.37", {"start": v(-56.7, 84.5) * mm, "mid": v(-54.49, 83.73) * mm, "end": v(-52.21, 84.33) * mm});
            skArc(sketch, "E675.38", {"start": v(-71.2, 69.04) * mm, "mid": v(-70.13, 71.14) * mm, "end": v(-70.42, 73.47) * mm});
            skArc(sketch, "E675.39", {"start": v(-71.67, 76.54) * mm, "mid": v(-71.07, 75) * mm, "end": v(-70.42, 73.47) * mm});
            skArc(sketch, "E675.40", {"start": v(-69.6, 78.42) * mm, "mid": v(-70.64, 77.49) * mm, "end": v(-71.67, 76.54) * mm});
            skArc(sketch, "E675.41", {"start": v(-66.63, 76.88) * mm, "mid": v(-68.1, 77.68) * mm, "end": v(-69.6, 78.42) * mm});
            skArc(sketch, "E675.42", {"start": v(-66.66, 76.9) * mm, "mid": v(-64.36, 76.4) * mm, "end": v(-62.18, 77.27) * mm});
            skArc(sketch, "E675.43", {"start": v(-79.15, 59.77) * mm, "mid": v(-78.34, 61.98) * mm, "end": v(-78.92, 64.26) * mm});
            skArc(sketch, "E675.44", {"start": v(-80.53, 67.15) * mm, "mid": v(-79.75, 65.7) * mm, "end": v(-78.92, 64.26) * mm});
            skArc(sketch, "E675.45", {"start": v(-78.71, 69.28) * mm, "mid": v(-79.63, 68.22) * mm, "end": v(-80.53, 67.15) * mm});
            skArc(sketch, "E675.46", {"start": v(-75.57, 68.11) * mm, "mid": v(-77.13, 68.72) * mm, "end": v(-78.71, 69.28) * mm});
            skArc(sketch, "E675.47", {"start": v(-75.6, 68.13) * mm, "mid": v(-73.26, 67.9) * mm, "end": v(-71.2, 69.04) * mm});
            skArc(sketch, "E675.48", {"start": v(-85.9, 49.6) * mm, "mid": v(-85.37, 51.88) * mm, "end": v(-86.21, 54.07) * mm});
            skArc(sketch, "E675.49", {"start": v(-88.17, 56.75) * mm, "mid": v(-87.22, 55.4) * mm, "end": v(-86.21, 54.07) * mm});
            skArc(sketch, "E675.50", {"start": v(-86.63, 59.08) * mm, "mid": v(-87.4, 57.92) * mm, "end": v(-88.17, 56.75) * mm});
            skArc(sketch, "E675.51", {"start": v(-83.37, 58.3) * mm, "mid": v(-85, 58.72) * mm, "end": v(-86.63, 59.08) * mm});
            skArc(sketch, "E675.52", {"start": v(-83.4, 58.32) * mm, "mid": v(-81.05, 58.4) * mm, "end": v(-79.15, 59.77) * mm});
            skArc(sketch, "E675.53", {"start": v(-91.34, 38.66) * mm, "mid": v(-91.1, 41) * mm, "end": v(-92.2, 43.07) * mm});
            skArc(sketch, "E675.54", {"start": v(-94.48, 45.48) * mm, "mid": v(-93.36, 44.26) * mm, "end": v(-92.2, 43.07) * mm});
            skArc(sketch, "E675.55", {"start": v(-93.23, 47.99) * mm, "mid": v(-93.86, 46.74) * mm, "end": v(-94.48, 45.48) * mm});
            skArc(sketch, "E675.56", {"start": v(-89.9, 47.62) * mm, "mid": v(-91.56, 47.83) * mm, "end": v(-93.23, 47.99) * mm});
            skArc(sketch, "E675.57", {"start": v(-89.94, 47.63) * mm, "mid": v(-87.61, 47.99) * mm, "end": v(-85.9, 49.6) * mm});
            skArc(sketch, "E675.58", {"start": v(-95.4, 27.14) * mm, "mid": v(-95.44, 29.5) * mm, "end": v(-96.8, 31.41) * mm});
            skArc(sketch, "E675.59", {"start": v(-99.35, 33.53) * mm, "mid": v(-98.1, 32.45) * mm, "end": v(-96.8, 31.41) * mm});
            skArc(sketch, "E675.60", {"start": v(-98.42, 36.16) * mm, "mid": v(-98.9, 34.85) * mm, "end": v(-99.35, 33.53) * mm});
            skArc(sketch, "E675.61", {"start": v(-95.07, 36.21) * mm, "mid": v(-96.75, 36.22) * mm, "end": v(-98.42, 36.16) * mm});
            skArc(sketch, "E675.62", {"start": v(-95.1, 36.21) * mm, "mid": v(-92.85, 36.86) * mm, "end": v(-91.34, 38.66) * mm});
            skArc(sketch, "E675.63", {"start": v(-98, 15.21) * mm, "mid": v(-98.34, 17.54) * mm, "end": v(-99.93, 19.28) * mm});
            skArc(sketch, "E675.64", {"start": v(-102.72, 21.07) * mm, "mid": v(-101.34, 20.15) * mm, "end": v(-99.93, 19.28) * mm});
            skArc(sketch, "E675.65", {"start": v(-102.12, 23.8) * mm, "mid": v(-102.43, 22.43) * mm, "end": v(-102.72, 21.07) * mm});
            skArc(sketch, "E675.66", {"start": v(-98.8, 24.26) * mm, "mid": v(-100.47, 24.05) * mm, "end": v(-102.12, 23.8) * mm});
            skArc(sketch, "E675.67", {"start": v(-98.84, 24.25) * mm, "mid": v(-96.67, 25.17) * mm, "end": v(-95.4, 27.14) * mm});
            skArc(sketch, "E675.68", {"start": v(-99.13, 3.05) * mm, "mid": v(-99.75, 5.32) * mm, "end": v(-101.54, 6.85) * mm});
            skArc(sketch, "E675.69", {"start": v(-104.53, 8.28) * mm, "mid": v(-103.05, 7.54) * mm, "end": v(-101.54, 6.85) * mm});
            skArc(sketch, "E675.70", {"start": v(-104.27, 11.07) * mm, "mid": v(-104.4, 9.67) * mm, "end": v(-104.53, 8.28) * mm});
            skArc(sketch, "E675.71", {"start": v(-101.03, 11.93) * mm, "mid": v(-102.66, 11.53) * mm, "end": v(-104.27, 11.07) * mm});
            skArc(sketch, "E675.72", {"start": v(-101.07, 11.92) * mm, "mid": v(-99.03, 13.1) * mm, "end": v(-98, 15.21) * mm});
            skArc(sketch, "E675.73", {"start": v(-98.76, -9.15) * mm, "mid": v(-99.65, -6.98) * mm, "end": v(-101.61, -5.68) * mm});
            skArc(sketch, "E675.74", {"start": v(-104.75, -4.63) * mm, "mid": v(-103.2, -5.18) * mm, "end": v(-101.61, -5.68) * mm});
            skArc(sketch, "E675.75", {"start": v(-104.84, -1.83) * mm, "mid": v(-104.8, -3.23) * mm, "end": v(-104.75, -4.63) * mm});
            skArc(sketch, "E675.76", {"start": v(-101.74, -0.58) * mm, "mid": v(-103.3, -1.18) * mm, "end": v(-104.84, -1.83) * mm});
            skArc(sketch, "E675.77", {"start": v(-101.77, -0.59) * mm, "mid": v(-99.9, 0.83) * mm, "end": v(-99.13, 3.05) * mm});
            skArc(sketch, "E675.78", {"start": v(-96.88, -21.22) * mm, "mid": v(-98.04, -19.17) * mm, "end": v(-100.14, -18.12) * mm});
            skArc(sketch, "E675.79", {"start": v(-103.4, -17.46) * mm, "mid": v(-101.77, -17.82) * mm, "end": v(-100.14, -18.12) * mm});
            skArc(sketch, "E675.80", {"start": v(-103.82, -14.7) * mm, "mid": v(-103.62, -16.08) * mm, "end": v(-103.4, -17.46) * mm});
            skArc(sketch, "E675.81", {"start": v(-100.9, -13.07) * mm, "mid": v(-102.37, -13.86) * mm, "end": v(-103.82, -14.7) * mm});
            skArc(sketch, "E675.82", {"start": v(-100.92, -13.09) * mm, "mid": v(-99.24, -11.45) * mm, "end": v(-98.76, -9.15) * mm});
            skArc(sketch, "E675.83", {"start": v(-93.54, -32.96) * mm, "mid": v(-94.94, -31.07) * mm, "end": v(-97.16, -30.3) * mm});
            skArc(sketch, "E675.84", {"start": v(-100.46, -30.04) * mm, "mid": v(-98.81, -30.2) * mm, "end": v(-97.16, -30.3) * mm});
            skArc(sketch, "E675.85", {"start": v(-101.23, -27.35) * mm, "mid": v(-100.85, -28.7) * mm, "end": v(-100.46, -30.04) * mm});
            skArc(sketch, "E675.86", {"start": v(-98.52, -25.37) * mm, "mid": v(-99.9, -26.34) * mm, "end": v(-101.23, -27.35) * mm});
            skArc(sketch, "E675.87", {"start": v(-98.55, -25.4) * mm, "mid": v(-97.08, -23.56) * mm, "end": v(-96.88, -21.22) * mm});
            skArc(sketch, "E675.88", {"start": v(-88.78, -44.2) * mm, "mid": v(-90.4, -42.5) * mm, "end": v(-92.7, -42) * mm});
            skArc(sketch, "E675.89", {"start": v(-96, -42.15) * mm, "mid": v(-94.35, -42.1) * mm, "end": v(-92.7, -42) * mm});
            skArc(sketch, "E675.90", {"start": v(-97.1, -39.58) * mm, "mid": v(-96.56, -40.87) * mm, "end": v(-96, -42.15) * mm});
            skArc(sketch, "E675.91", {"start": v(-94.66, -37.29) * mm, "mid": v(-95.9, -38.41) * mm, "end": v(-97.1, -39.58) * mm});
            skArc(sketch, "E675.92", {"start": v(-94.68, -37.31) * mm, "mid": v(-93.45, -35.31) * mm, "end": v(-93.54, -32.96) * mm});
            skArc(sketch, "E675.93", {"start": v(-82.68, -54.78) * mm, "mid": v(-84.5, -53.3) * mm, "end": v(-86.83, -53.07) * mm});
            skArc(sketch, "E675.94", {"start": v(-90.1, -53.63) * mm, "mid": v(-88.46, -53.38) * mm, "end": v(-86.83, -53.07) * mm});
            skArc(sketch, "E675.95", {"start": v(-91.5, -51.21) * mm, "mid": v(-90.8, -52.43) * mm, "end": v(-90.1, -53.63) * mm});
            skArc(sketch, "E675.96", {"start": v(-89.36, -48.64) * mm, "mid": v(-90.45, -49.9) * mm, "end": v(-91.5, -51.21) * mm});
            skArc(sketch, "E675.97", {"start": v(-89.38, -48.66) * mm, "mid": v(-88.4, -46.53) * mm, "end": v(-88.78, -44.2) * mm});
            skArc(sketch, "E675.98", {"start": v(-75.32, -64.53) * mm, "mid": v(-77.3, -63.27) * mm, "end": v(-79.65, -63.34) * mm});
            skArc(sketch, "E675.99", {"start": v(-82.83, -64.3) * mm, "mid": v(-81.23, -63.85) * mm, "end": v(-79.65, -63.34) * mm});
            skArc(sketch, "E675.100", {"start": v(-84.51, -62.07) * mm, "mid": v(-83.68, -63.2) * mm, "end": v(-82.83, -64.3) * mm});
            skArc(sketch, "E675.101", {"start": v(-82.7, -59.25) * mm, "mid": v(-83.63, -60.64) * mm, "end": v(-84.51, -62.07) * mm});
            skArc(sketch, "E675.102", {"start": v(-82.72, -59.28) * mm, "mid": v(-82.01, -57.04) * mm, "end": v(-82.68, -54.78) * mm});
            skArc(sketch, "E675.103", {"start": v(-66.82, -73.3) * mm, "mid": v(-68.94, -72.3) * mm, "end": v(-71.27, -72.65) * mm});
            skArc(sketch, "E675.104", {"start": v(-74.3, -74) * mm, "mid": v(-72.77, -73.35) * mm, "end": v(-71.27, -72.65) * mm});
            skArc(sketch, "E675.105", {"start": v(-76.24, -71.98) * mm, "mid": v(-75.28, -73) * mm, "end": v(-74.3, -74) * mm});
            skArc(sketch, "E675.106", {"start": v(-74.8, -68.96) * mm, "mid": v(-75.55, -70.46) * mm, "end": v(-76.24, -71.98) * mm});
            skArc(sketch, "E675.107", {"start": v(-74.81, -69) * mm, "mid": v(-74.38, -66.68) * mm, "end": v(-75.32, -64.53) * mm});
            skArc(sketch, "E675.108", {"start": v(-57.3, -80.95) * mm, "mid": v(-59.54, -80.22) * mm, "end": v(-61.8, -80.86) * mm});
            skArc(sketch, "E675.109", {"start": v(-64.64, -82.56) * mm, "mid": v(-63.2, -81.73) * mm, "end": v(-61.8, -80.86) * mm});
            skArc(sketch, "E675.110", {"start": v(-66.82, -80.8) * mm, "mid": v(-65.74, -81.7) * mm, "end": v(-64.64, -82.56) * mm});
            skArc(sketch, "E675.111", {"start": v(-65.75, -77.63) * mm, "mid": v(-66.31, -79.21) * mm, "end": v(-66.82, -80.8) * mm});
            skArc(sketch, "E675.112", {"start": v(-65.76, -77.66) * mm, "mid": v(-65.62, -75.32) * mm, "end": v(-66.82, -73.3) * mm});
            skArc(sketch, "E675.113", {"start": v(-46.92, -87.38) * mm, "mid": v(-49.23, -86.92) * mm, "end": v(-51.4, -87.84) * mm});
            skArc(sketch, "E675.114", {"start": v(-54, -89.88) * mm, "mid": v(-52.68, -88.88) * mm, "end": v(-51.4, -87.84) * mm});
            skArc(sketch, "E675.115", {"start": v(-56.38, -88.4) * mm, "mid": v(-55.2, -89.15) * mm, "end": v(-54, -89.88) * mm});
            skArc(sketch, "E675.116", {"start": v(-55.71, -85.12) * mm, "mid": v(-56.08, -86.76) * mm, "end": v(-56.38, -88.4) * mm});
            skArc(sketch, "E675.117", {"start": v(-55.72, -85.16) * mm, "mid": v(-55.87, -82.81) * mm, "end": v(-57.3, -80.95) * mm});
            skArc(sketch, "E675.118", {"start": v(-35.83, -92.48) * mm, "mid": v(-38.17, -92.31) * mm, "end": v(-40.2, -93.49) * mm});
            skArc(sketch, "E675.119", {"start": v(-42.55, -95.83) * mm, "mid": v(-41.36, -94.68) * mm, "end": v(-40.2, -93.49) * mm});
            skArc(sketch, "E675.120", {"start": v(-45.1, -94.67) * mm, "mid": v(-43.83, -95.26) * mm, "end": v(-42.55, -95.83) * mm});
            skArc(sketch, "E675.121", {"start": v(-44.83, -91.33) * mm, "mid": v(-45, -93) * mm, "end": v(-45.1, -94.67) * mm});
            skArc(sketch, "E675.122", {"start": v(-44.84, -91.36) * mm, "mid": v(-45.27, -89.05) * mm, "end": v(-46.92, -87.38) * mm});
            skArc(sketch, "E675.123", {"start": v(-24.2, -96.19) * mm, "mid": v(-26.54, -96.3) * mm, "end": v(-28.42, -97.72) * mm});
            skArc(sketch, "E675.124", {"start": v(-30.45, -100.34) * mm, "mid": v(-29.41, -99.05) * mm, "end": v(-28.42, -97.72) * mm});
            skArc(sketch, "E675.125", {"start": v(-33.12, -99.49) * mm, "mid": v(-31.79, -99.92) * mm, "end": v(-30.45, -100.34) * mm});
            skArc(sketch, "E675.126", {"start": v(-33.27, -96.14) * mm, "mid": v(-33.22, -97.82) * mm, "end": v(-33.12, -99.49) * mm});
            skArc(sketch, "E675.127", {"start": v(-33.27, -96.18) * mm, "mid": v(-33.98, -93.94) * mm, "end": v(-35.83, -92.48) * mm});
            skArc(sketch, "E675.128", {"start": v(-12.19, -98.43) * mm, "mid": v(-14.5, -98.84) * mm, "end": v(-16.2, -100.47) * mm});
            skArc(sketch, "E675.129", {"start": v(-17.9, -103.32) * mm, "mid": v(-17.02, -101.91) * mm, "end": v(-16.2, -100.47) * mm});
            skArc(sketch, "E675.130", {"start": v(-20.64, -102.8) * mm, "mid": v(-19.27, -103.07) * mm, "end": v(-17.9, -103.32) * mm});
            skArc(sketch, "E675.131", {"start": v(-21.2, -99.5) * mm, "mid": v(-20.95, -101.16) * mm, "end": v(-20.64, -102.8) * mm});
            skArc(sketch, "E675.132", {"start": v(-21.2, -99.54) * mm, "mid": v(-22.18, -97.4) * mm, "end": v(-24.2, -96.19) * mm});
            skArc(sketch, "E675.133", {"start": v(0, -99.18) * mm, "mid": v(-2.25, -99.87) * mm, "end": v(-3.72, -101.7) * mm});
            skArc(sketch, "E675.134", {"start": v(-5.06, -104.73) * mm, "mid": v(-4.36, -103.23) * mm, "end": v(-3.72, -101.7) * mm});
            skArc(sketch, "E675.135", {"start": v(-7.85, -104.56) * mm, "mid": v(-6.46, -104.66) * mm, "end": v(-5.06, -104.73) * mm});
            skArc(sketch, "E675.136", {"start": v(-8.81, -101.35) * mm, "mid": v(-8.36, -102.97) * mm, "end": v(-7.85, -104.56) * mm});
            skArc(sketch, "E675.137", {"start": v(-8.8, -101.39) * mm, "mid": v(-10.04, -99.39) * mm, "end": v(-12.19, -98.43) * mm});
            skArc(sketch, "E675.138", {"start": v(12.19, -98.43) * mm, "mid": v(10.04, -99.39) * mm, "end": v(8.8, -101.39) * mm});
            skArc(sketch, "E675.139", {"start": v(7.85, -104.56) * mm, "mid": v(8.35, -102.98) * mm, "end": v(8.8, -101.39) * mm});
            skArc(sketch, "E675.140", {"start": v(5.06, -104.73) * mm, "mid": v(6.46, -104.66) * mm, "end": v(7.85, -104.56) * mm});
            skArc(sketch, "E675.141", {"start": v(3.7, -101.67) * mm, "mid": v(4.36, -103.21) * mm, "end": v(5.06, -104.73) * mm});
            skArc(sketch, "E675.142", {"start": v(3.72, -101.7) * mm, "mid": v(2.25, -99.87) * mm, "end": v(0, -99.18) * mm});
            skArc(sketch, "E675.143", {"start": v(24.2, -96.19) * mm, "mid": v(22.18, -97.4) * mm, "end": v(21.2, -99.54) * mm});
            skArc(sketch, "E675.144", {"start": v(20.64, -102.8) * mm, "mid": v(20.95, -101.18) * mm, "end": v(21.2, -99.54) * mm});
            skArc(sketch, "E675.145", {"start": v(17.9, -103.32) * mm, "mid": v(19.27, -103.07) * mm, "end": v(20.64, -102.8) * mm});
            skArc(sketch, "E675.146", {"start": v(16.17, -100.44) * mm, "mid": v(17, -101.9) * mm, "end": v(17.9, -103.32) * mm});
            skArc(sketch, "E675.147", {"start": v(16.2, -100.47) * mm, "mid": v(14.5, -98.84) * mm, "end": v(12.19, -98.43) * mm});
            skArc(sketch, "E675.148", {"start": v(35.83, -92.48) * mm, "mid": v(33.98, -93.94) * mm, "end": v(33.27, -96.18) * mm});
            skArc(sketch, "E675.149", {"start": v(33.12, -99.49) * mm, "mid": v(33.22, -97.83) * mm, "end": v(33.27, -96.18) * mm});
            skArc(sketch, "E675.150", {"start": v(30.45, -100.34) * mm, "mid": v(31.79, -99.92) * mm, "end": v(33.12, -99.49) * mm});
            skArc(sketch, "E675.151", {"start": v(28.4, -97.7) * mm, "mid": v(29.4, -99.03) * mm, "end": v(30.45, -100.34) * mm});
            skArc(sketch, "E675.152", {"start": v(28.42, -97.72) * mm, "mid": v(26.54, -96.3) * mm, "end": v(24.2, -96.19) * mm});
            skArc(sketch, "E675.153", {"start": v(46.92, -87.38) * mm, "mid": v(45.27, -89.05) * mm, "end": v(44.84, -91.36) * mm});
            skArc(sketch, "E675.154", {"start": v(45.1, -94.67) * mm, "mid": v(45, -93.01) * mm, "end": v(44.84, -91.36) * mm});
            skArc(sketch, "E675.155", {"start": v(42.55, -95.83) * mm, "mid": v(43.83, -95.26) * mm, "end": v(45.1, -94.67) * mm});
            skArc(sketch, "E675.156", {"start": v(40.19, -93.46) * mm, "mid": v(41.35, -94.67) * mm, "end": v(42.55, -95.83) * mm});
            skArc(sketch, "E675.157", {"start": v(40.2, -93.49) * mm, "mid": v(38.17, -92.31) * mm, "end": v(35.83, -92.48) * mm});
            skArc(sketch, "E675.158", {"start": v(57.3, -80.95) * mm, "mid": v(55.87, -82.81) * mm, "end": v(55.72, -85.16) * mm});
            skArc(sketch, "E675.159", {"start": v(56.38, -88.4) * mm, "mid": v(56.08, -86.78) * mm, "end": v(55.72, -85.16) * mm});
            skArc(sketch, "E675.160", {"start": v(54, -89.88) * mm, "mid": v(55.2, -89.15) * mm, "end": v(56.38, -88.4) * mm});
            skArc(sketch, "E675.161", {"start": v(51.37, -87.82) * mm, "mid": v(52.67, -88.87) * mm, "end": v(54, -89.88) * mm});
            skArc(sketch, "E675.162", {"start": v(51.4, -87.84) * mm, "mid": v(49.23, -86.92) * mm, "end": v(46.92, -87.38) * mm});
            skArc(sketch, "E675.163", {"start": v(66.82, -73.3) * mm, "mid": v(65.62, -75.32) * mm, "end": v(65.76, -77.66) * mm});
            skArc(sketch, "E675.164", {"start": v(66.82, -80.8) * mm, "mid": v(66.32, -79.23) * mm, "end": v(65.76, -77.66) * mm});
            skArc(sketch, "E675.165", {"start": v(64.64, -82.56) * mm, "mid": v(65.74, -81.7) * mm, "end": v(66.82, -80.8) * mm});
            skArc(sketch, "E675.166", {"start": v(61.77, -80.84) * mm, "mid": v(63.2, -81.72) * mm, "end": v(64.64, -82.56) * mm});
            skArc(sketch, "E675.167", {"start": v(61.8, -80.86) * mm, "mid": v(59.54, -80.22) * mm, "end": v(57.3, -80.95) * mm});
            skArc(sketch, "E675.168", {"start": v(75.32, -64.53) * mm, "mid": v(74.38, -66.68) * mm, "end": v(74.81, -69) * mm});
            skArc(sketch, "E675.169", {"start": v(76.24, -71.98) * mm, "mid": v(75.55, -70.48) * mm, "end": v(74.81, -69) * mm});
            skArc(sketch, "E675.170", {"start": v(74.3, -74) * mm, "mid": v(75.28, -73) * mm, "end": v(76.24, -71.98) * mm});
            skArc(sketch, "E675.171", {"start": v(71.23, -72.64) * mm, "mid": v(72.75, -73.34) * mm, "end": v(74.3, -74) * mm});
            skArc(sketch, "E675.172", {"start": v(71.27, -72.65) * mm, "mid": v(68.94, -72.3) * mm, "end": v(66.82, -73.3) * mm});
            skArc(sketch, "E675.173", {"start": v(82.68, -54.78) * mm, "mid": v(82.01, -57.04) * mm, "end": v(82.72, -59.28) * mm});
            skArc(sketch, "E675.174", {"start": v(84.51, -62.07) * mm, "mid": v(83.64, -60.66) * mm, "end": v(82.72, -59.28) * mm});
            skArc(sketch, "E675.175", {"start": v(82.83, -64.3) * mm, "mid": v(83.68, -63.2) * mm, "end": v(84.51, -62.07) * mm});
            skArc(sketch, "E675.176", {"start": v(79.62, -63.33) * mm, "mid": v(81.22, -63.84) * mm, "end": v(82.83, -64.3) * mm});
            skArc(sketch, "E675.177", {"start": v(79.65, -63.34) * mm, "mid": v(77.3, -63.27) * mm, "end": v(75.32, -64.53) * mm});
            skArc(sketch, "E675.178", {"start": v(88.78, -44.2) * mm, "mid": v(88.4, -46.53) * mm, "end": v(89.38, -48.66) * mm});
            skArc(sketch, "E675.179", {"start": v(91.5, -51.21) * mm, "mid": v(90.46, -49.92) * mm, "end": v(89.38, -48.66) * mm});
            skArc(sketch, "E675.180", {"start": v(90.1, -53.63) * mm, "mid": v(90.8, -52.43) * mm, "end": v(91.5, -51.21) * mm});
            skArc(sketch, "E675.181", {"start": v(86.8, -53.07) * mm, "mid": v(88.45, -53.38) * mm, "end": v(90.1, -53.63) * mm});
            skArc(sketch, "E675.182", {"start": v(86.83, -53.07) * mm, "mid": v(84.5, -53.3) * mm, "end": v(82.68, -54.78) * mm});
            skArc(sketch, "E675.183", {"start": v(93.54, -32.96) * mm, "mid": v(93.45, -35.31) * mm, "end": v(94.68, -37.31) * mm});
            skArc(sketch, "E675.184", {"start": v(97.1, -39.58) * mm, "mid": v(95.91, -38.42) * mm, "end": v(94.68, -37.31) * mm});
            skArc(sketch, "E675.185", {"start": v(96, -42.15) * mm, "mid": v(96.56, -40.87) * mm, "end": v(97.1, -39.58) * mm});
            skArc(sketch, "E675.186", {"start": v(92.66, -42) * mm, "mid": v(94.34, -42.1) * mm, "end": v(96, -42.15) * mm});
            skArc(sketch, "E675.187", {"start": v(92.7, -42) * mm, "mid": v(90.4, -42.5) * mm, "end": v(88.78, -44.2) * mm});
            skArc(sketch, "E675.188", {"start": v(96.88, -21.22) * mm, "mid": v(97.08, -23.56) * mm, "end": v(98.55, -25.4) * mm});
            skArc(sketch, "E675.189", {"start": v(101.23, -27.35) * mm, "mid": v(99.9, -26.35) * mm, "end": v(98.55, -25.4) * mm});
            skArc(sketch, "E675.190", {"start": v(100.46, -30.04) * mm, "mid": v(100.85, -28.7) * mm, "end": v(101.23, -27.35) * mm});
            skArc(sketch, "E675.191", {"start": v(97.12, -30.3) * mm, "mid": v(98.8, -30.2) * mm, "end": v(100.46, -30.04) * mm});
            skArc(sketch, "E675.192", {"start": v(97.16, -30.3) * mm, "mid": v(94.94, -31.07) * mm, "end": v(93.54, -32.96) * mm});
            skArc(sketch, "E675.193", {"start": v(98.76, -9.15) * mm, "mid": v(99.24, -11.45) * mm, "end": v(100.92, -13.09) * mm});
            skArc(sketch, "E675.194", {"start": v(103.82, -14.7) * mm, "mid": v(102.39, -13.87) * mm, "end": v(100.92, -13.09) * mm});
            skArc(sketch, "E675.195", {"start": v(103.4, -17.46) * mm, "mid": v(103.62, -16.08) * mm, "end": v(103.82, -14.7) * mm});
            skArc(sketch, "E675.196", {"start": v(100.1, -18.13) * mm, "mid": v(101.76, -17.82) * mm, "end": v(103.4, -17.46) * mm});
            skArc(sketch, "E675.197", {"start": v(100.14, -18.12) * mm, "mid": v(98.04, -19.17) * mm, "end": v(96.88, -21.22) * mm});
            skArc(sketch, "E675.198", {"start": v(99.13, 3.05) * mm, "mid": v(99.9, 0.83) * mm, "end": v(101.77, -0.59) * mm});
            skArc(sketch, "E675.199", {"start": v(104.84, -1.83) * mm, "mid": v(103.31, -1.18) * mm, "end": v(101.77, -0.59) * mm});
            skArc(sketch, "E675.200", {"start": v(104.75, -4.63) * mm, "mid": v(104.8, -3.23) * mm, "end": v(104.84, -1.83) * mm});
            skArc(sketch, "E675.201", {"start": v(101.58, -5.69) * mm, "mid": v(103.18, -5.18) * mm, "end": v(104.75, -4.63) * mm});
            skArc(sketch, "E675.202", {"start": v(101.61, -5.68) * mm, "mid": v(99.65, -6.98) * mm, "end": v(98.76, -9.15) * mm});
            skArc(sketch, "E675.203", {"start": v(98, 15.21) * mm, "mid": v(99.03, 13.1) * mm, "end": v(101.07, 11.92) * mm});
            skArc(sketch, "E675.204", {"start": v(104.27, 11.07) * mm, "mid": v(102.68, 11.52) * mm, "end": v(101.07, 11.92) * mm});
            skArc(sketch, "E675.205", {"start": v(104.53, 8.28) * mm, "mid": v(104.4, 9.67) * mm, "end": v(104.27, 11.07) * mm});
            skArc(sketch, "E675.206", {"start": v(101.5, 6.84) * mm, "mid": v(103.03, 7.53) * mm, "end": v(104.53, 8.28) * mm});
            skArc(sketch, "E675.207", {"start": v(101.54, 6.85) * mm, "mid": v(99.75, 5.32) * mm, "end": v(99.13, 3.05) * mm});
            skArc(sketch, "E675.208", {"start": v(95.4, 27.14) * mm, "mid": v(96.67, 25.17) * mm, "end": v(98.84, 24.25) * mm});
            skArc(sketch, "E675.209", {"start": v(102.12, 23.8) * mm, "mid": v(100.48, 24.05) * mm, "end": v(98.84, 24.25) * mm});
            skArc(sketch, "E675.210", {"start": v(102.72, 21.07) * mm, "mid": v(102.43, 22.43) * mm, "end": v(102.12, 23.8) * mm});
            skArc(sketch, "E675.211", {"start": v(99.9, 19.26) * mm, "mid": v(101.32, 20.14) * mm, "end": v(102.72, 21.07) * mm});
            skArc(sketch, "E675.212", {"start": v(99.93, 19.28) * mm, "mid": v(98.34, 17.54) * mm, "end": v(98, 15.21) * mm});
            skArc(sketch, "E675.213", {"start": v(91.34, 38.66) * mm, "mid": v(92.85, 36.86) * mm, "end": v(95.1, 36.21) * mm});
            skArc(sketch, "E675.214", {"start": v(98.42, 36.16) * mm, "mid": v(96.77, 36.22) * mm, "end": v(95.1, 36.21) * mm});
            skArc(sketch, "E675.215", {"start": v(99.35, 33.53) * mm, "mid": v(98.9, 34.85) * mm, "end": v(98.42, 36.16) * mm});
            skArc(sketch, "E675.216", {"start": v(96.77, 31.4) * mm, "mid": v(98.08, 32.44) * mm, "end": v(99.35, 33.53) * mm});
            skArc(sketch, "E675.217", {"start": v(96.8, 31.41) * mm, "mid": v(95.44, 29.5) * mm, "end": v(95.4, 27.14) * mm});
            skArc(sketch, "E675.218", {"start": v(85.9, 49.6) * mm, "mid": v(87.61, 47.99) * mm, "end": v(89.94, 47.63) * mm});
            skArc(sketch, "E675.219", {"start": v(93.23, 47.99) * mm, "mid": v(91.58, 47.83) * mm, "end": v(89.94, 47.63) * mm});
            skArc(sketch, "E675.220", {"start": v(94.48, 45.48) * mm, "mid": v(93.86, 46.74) * mm, "end": v(93.23, 47.99) * mm});
            skArc(sketch, "E675.221", {"start": v(92.18, 43.04) * mm, "mid": v(93.35, 44.24) * mm, "end": v(94.48, 45.48) * mm});
            skArc(sketch, "E675.222", {"start": v(92.2, 43.07) * mm, "mid": v(91.1, 41) * mm, "end": v(91.34, 38.66) * mm});
            skArc(sketch, "E675.223", {"start": v(79.15, 59.77) * mm, "mid": v(81.05, 58.4) * mm, "end": v(83.4, 58.32) * mm});
            skArc(sketch, "E675.224", {"start": v(86.63, 59.08) * mm, "mid": v(85, 58.73) * mm, "end": v(83.4, 58.32) * mm});
            skArc(sketch, "E675.225", {"start": v(88.17, 56.75) * mm, "mid": v(87.4, 57.92) * mm, "end": v(86.63, 59.08) * mm});
            skArc(sketch, "E675.226", {"start": v(86.2, 54.05) * mm, "mid": v(87.2, 55.38) * mm, "end": v(88.17, 56.75) * mm});
            skArc(sketch, "E675.227", {"start": v(86.21, 54.07) * mm, "mid": v(85.37, 51.88) * mm, "end": v(85.9, 49.6) * mm});
            skPoint(sketch, "E675.228", {"position": v(0, 0) * mm});
            skArc(sketch, "E675.229", {"start": v(71.2, 69.04) * mm, "mid": v(73.26, 67.9) * mm, "end": v(75.6, 68.13) * mm});
            skArc(sketch, "E675.230", {"start": v(78.71, 69.28) * mm, "mid": v(77.15, 68.73) * mm, "end": v(75.6, 68.13) * mm});
            skArc(sketch, "E675.231", {"start": v(80.53, 67.15) * mm, "mid": v(79.63, 68.22) * mm, "end": v(78.71, 69.28) * mm});
            skArc(sketch, "E675.232", {"start": v(78.9, 64.23) * mm, "mid": v(79.74, 65.68) * mm, "end": v(80.53, 67.15) * mm});
            skArc(sketch, "E675.233", {"start": v(78.92, 64.26) * mm, "mid": v(78.34, 61.98) * mm, "end": v(79.15, 59.77) * mm});
            skArc(sketch, "E675.234", {"start": v(62.18, 77.27) * mm, "mid": v(64.36, 76.4) * mm, "end": v(66.66, 76.9) * mm});
            skArc(sketch, "E675.235", {"start": v(69.6, 78.42) * mm, "mid": v(68.12, 77.69) * mm, "end": v(66.66, 76.9) * mm});
            skArc(sketch, "E675.236", {"start": v(71.67, 76.54) * mm, "mid": v(70.64, 77.49) * mm, "end": v(69.6, 78.42) * mm});
            skArc(sketch, "E675.237", {"start": v(70.4, 73.44) * mm, "mid": v(71.06, 74.98) * mm, "end": v(71.67, 76.54) * mm});
            skArc(sketch, "E675.238", {"start": v(70.42, 73.47) * mm, "mid": v(70.13, 71.14) * mm, "end": v(71.2, 69.04) * mm});
            skArc(sketch, "E675.239", {"start": v(52.21, 84.33) * mm, "mid": v(54.49, 83.73) * mm, "end": v(56.7, 84.5) * mm});
            skArc(sketch, "E675.240", {"start": v(59.44, 86.38) * mm, "mid": v(58.05, 85.47) * mm, "end": v(56.7, 84.5) * mm});
            skArc(sketch, "E675.241", {"start": v(61.72, 84.77) * mm, "mid": v(60.58, 85.58) * mm, "end": v(59.44, 86.38) * mm});
            skArc(sketch, "E675.242", {"start": v(60.85, 81.53) * mm, "mid": v(61.31, 83.14) * mm, "end": v(61.72, 84.77) * mm});
            skArc(sketch, "E675.243", {"start": v(60.86, 81.57) * mm, "mid": v(60.86, 79.22) * mm, "end": v(62.18, 77.27) * mm});
            skArc(sketch, "E675.244", {"start": v(41.45, 90.1) * mm, "mid": v(43.78, 89.79) * mm, "end": v(45.89, 90.84) * mm});
            skArc(sketch, "E675.245", {"start": v(48.37, 93.03) * mm, "mid": v(47.11, 91.96) * mm, "end": v(45.89, 90.84) * mm});
            skArc(sketch, "E675.246", {"start": v(50.83, 91.71) * mm, "mid": v(49.6, 92.38) * mm, "end": v(48.37, 93.03) * mm});
            skArc(sketch, "E675.247", {"start": v(50.37, 88.4) * mm, "mid": v(50.63, 90.05) * mm, "end": v(50.83, 91.71) * mm});
            skArc(sketch, "E675.248", {"start": v(50.37, 88.43) * mm, "mid": v(50.66, 86.1) * mm, "end": v(52.21, 84.33) * mm});
            skArc(sketch, "E675.249", {"start": v(30.07, 94.51) * mm, "mid": v(32.42, 94.49) * mm, "end": v(34.38, 95.79) * mm});
            skArc(sketch, "E675.250", {"start": v(36.57, 98.27) * mm, "mid": v(35.45, 97.05) * mm, "end": v(34.38, 95.79) * mm});
            skArc(sketch, "E675.251", {"start": v(39.18, 97.26) * mm, "mid": v(37.88, 97.78) * mm, "end": v(36.57, 98.27) * mm});
            skArc(sketch, "E675.252", {"start": v(39.12, 93.91) * mm, "mid": v(39.18, 95.59) * mm, "end": v(39.18, 97.26) * mm});
            skArc(sketch, "E675.253", {"start": v(39.13, 93.95) * mm, "mid": v(39.7, 91.67) * mm, "end": v(41.45, 90.1) * mm});
            skArc(sketch, "E675.254", {"start": v(18.22, 97.5) * mm, "mid": v(20.56, 97.76) * mm, "end": v(22.35, 99.29) * mm});
            skArc(sketch, "E675.255", {"start": v(24.22, 102.02) * mm, "mid": v(23.26, 100.67) * mm, "end": v(22.35, 99.29) * mm});
            skArc(sketch, "E675.256", {"start": v(26.93, 101.34) * mm, "mid": v(25.58, 101.69) * mm, "end": v(24.22, 102.02) * mm});
            skArc(sketch, "E675.257", {"start": v(27.29, 98) * mm, "mid": v(27.14, 99.68) * mm, "end": v(26.93, 101.34) * mm});
            skArc(sketch, "E675.258", {"start": v(27.28, 98.04) * mm, "mid": v(28.13, 95.85) * mm, "end": v(30.07, 94.51) * mm});
            skArc(sketch, "E675.259", {"start": v(6.1, 99) * mm, "mid": v(8.4, 99.54) * mm, "end": v(9.98, 101.28) * mm});
            skArc(sketch, "E675.260", {"start": v(11.5, 104.22) * mm, "mid": v(10.71, 102.76) * mm, "end": v(9.98, 101.28) * mm});
            skArc(sketch, "E675.261", {"start": v(14.27, 103.88) * mm, "mid": v(12.89, 104.06) * mm, "end": v(11.5, 104.22) * mm});
            skArc(sketch, "E675.262", {"start": v(15.04, 100.62) * mm, "mid": v(14.68, 102.26) * mm, "end": v(14.27, 103.88) * mm});
            skArc(sketch, "E675.263", {"start": v(15.03, 100.65) * mm, "mid": v(16.14, 98.58) * mm, "end": v(18.22, 97.5) * mm});
            skCircle(sketch, "E675.264", {"center": v(0, 0) * mm, "radius": 55 * mm});
            skCircle(sketch, "E675.265", {"center": v(0, -55) * mm, "radius": 5 * mm});
            skCircle(sketch, "E675.266", {"center": v(0, 0) * mm, "radius": 91.43 * mm});
            skLineSegment(sketch, "E675.267", {"start": v(-8, -47) * mm, "end": v(8, -47) * mm});
            skLineSegment(sketch, "E675.268", {"start": v(-8, -47) * mm, "end": v(-8, -82.38) * mm});
            skLineSegment(sketch, "E675.269", {"start": v(8, -47) * mm, "end": v(8, -82.38) * mm});
            skArc(sketch, "E675.270", {"start": v(-17, -89.84) * mm, "mid": v(-10.75, -88.22) * mm, "end": v(-8, -82.38) * mm});
            skArc(sketch, "E675.271", {"start": v(8, -82.38) * mm, "mid": v(10.75, -88.22) * mm, "end": v(17, -89.84) * mm});
            skArc(sketch, "E675.272", {"start": v(80.19, -43.92) * mm, "mid": v(80.59, -37.48) * mm, "end": v(75.88, -33.07) * mm});
            skLineSegment(sketch, "E675.273", {"start": v(42.23, -22.13) * mm, "end": v(75.88, -33.07) * mm});
            skLineSegment(sketch, "E675.274", {"start": v(42.23, -22.13) * mm, "end": v(47.17, -6.92) * mm});
            skCircle(sketch, "E675.275", {"center": v(52.3, -17) * mm, "radius": 5 * mm});
            skLineSegment(sketch, "E675.276", {"start": v(47.17, -6.92) * mm, "end": v(80.82, -17.85) * mm});
            skArc(sketch, "E675.277", {"start": v(80.82, -17.85) * mm, "mid": v(87.23, -17.04) * mm, "end": v(90.7, -11.6) * mm});
            skArc(sketch, "E675.278", {"start": v(66.55, 62.7) * mm, "mid": v(60.55, 65.06) * mm, "end": v(54.9, 61.95) * mm});
            skLineSegment(sketch, "E675.279", {"start": v(34.1, 33.32) * mm, "end": v(54.9, 61.95) * mm});
            skLineSegment(sketch, "E675.280", {"start": v(34.1, 33.32) * mm, "end": v(21.15, 42.73) * mm});
            skCircle(sketch, "E675.281", {"center": v(32.33, 44.5) * mm, "radius": 5 * mm});
            skLineSegment(sketch, "E675.282", {"start": v(21.15, 42.73) * mm, "end": v(41.95, 71.35) * mm});
            skArc(sketch, "E675.283", {"start": v(41.95, 71.35) * mm, "mid": v(43.16, 77.7) * mm, "end": v(39.06, 82.67) * mm});
            skArc(sketch, "E675.284", {"start": v(-39.06, 82.67) * mm, "mid": v(-43.16, 77.7) * mm, "end": v(-41.95, 71.35) * mm});
            skLineSegment(sketch, "E675.285", {"start": v(-21.15, 42.73) * mm, "end": v(-41.95, 71.35) * mm});
            skLineSegment(sketch, "E675.286", {"start": v(-21.15, 42.73) * mm, "end": v(-34.1, 33.32) * mm});
            skCircle(sketch, "E675.287", {"center": v(-32.33, 44.5) * mm, "radius": 5 * mm});
            skLineSegment(sketch, "E675.288", {"start": v(-34.1, 33.32) * mm, "end": v(-54.9, 61.95) * mm});
            skArc(sketch, "E675.289", {"start": v(-54.9, 61.95) * mm, "mid": v(-60.55, 65.06) * mm, "end": v(-66.55, 62.7) * mm});
            skArc(sketch, "E675.290", {"start": v(-90.7, -11.6) * mm, "mid": v(-87.23, -17.04) * mm, "end": v(-80.82, -17.85) * mm});
            skLineSegment(sketch, "E675.291", {"start": v(-47.17, -6.92) * mm, "end": v(-80.82, -17.85) * mm});
            skLineSegment(sketch, "E675.292", {"start": v(-47.17, -6.92) * mm, "end": v(-42.23, -22.13) * mm});
            skCircle(sketch, "E675.293", {"center": v(-52.3, -17) * mm, "radius": 5 * mm});
            skLineSegment(sketch, "E675.294", {"start": v(-42.23, -22.13) * mm, "end": v(-75.88, -33.07) * mm});
            skArc(sketch, "E675.295", {"start": v(-75.88, -33.07) * mm, "mid": v(-80.59, -37.48) * mm, "end": v(-80.19, -43.92) * mm});
            skPoint(sketch, "E675.296", {"position": v(0, 0) * mm});
            skCircle(sketch, "E675.297", {"center": v(0, 0) * mm, "radius": 95.24 * mm});
            skArc(sketch, "E675.298", {"start": v(-48.46, -20.2) * mm, "mid": v(-30.86, -42.47) * mm, "end": v(-4.23, -52.33) * mm});
            skArc(sketch, "E675.299", {"start": v(-53.16, -21.92) * mm, "mid": v(-33.8, -46.52) * mm, "end": v(-4.42, -57.33) * mm});
            skArc(sketch, "E675.300", {"start": v(51.07, -12.15) * mm, "mid": v(49.93, 16.22) * mm, "end": v(34.18, 39.85) * mm});
            skArc(sketch, "E675.301", {"start": v(55.9, -13.5) * mm, "mid": v(54.69, 17.77) * mm, "end": v(37.28, 43.78) * mm});
            skArc(sketch, "E675.302", {"start": v(-34.18, 39.85) * mm, "mid": v(-49.93, 16.22) * mm, "end": v(-51.07, -12.15) * mm});
            skArc(sketch, "E675.303", {"start": v(-37.28, 43.78) * mm, "mid": v(-54.69, 17.77) * mm, "end": v(-55.9, -13.5) * mm});
            skArc(sketch, "E675.304", {"start": v(27.34, 44.82) * mm, "mid": v(0, 52.5) * mm, "end": v(-27.34, 44.82) * mm});
            skArc(sketch, "E675.305", {"start": v(30.12, 48.98) * mm, "mid": v(0, 57.5) * mm, "end": v(-30.12, 48.98) * mm});
            skLineSegment(sketch, "E676.trimOffspring", {"start": v(47.4, -16.01) * mm, "end": v(47.03, -16.59) * mm});
            skSolve(sketch);
        }
        {
            var Q0;
            {var subQ5=sQuery(id+"F0.wireOp",EDGE,"E21.3.0");Q0=makeQuery(id+"F0.imprint","IMPRINT",FACE,{"disambiguationData":[TD([[makeQuery(id+"F0.imprint","IMPRINT",EDGE,{"derivedFrom":subQ5}),-1.0]])]});}
            var Q1;
            {var subQ5=sQuery(id+"F0.wireOp",EDGE,"E21.2.0");Q1=makeQuery(id+"F0.imprint","IMPRINT",FACE,{"disambiguationData":[TD([[makeQuery(id+"F0.imprint","IMPRINT",EDGE,{"derivedFrom":subQ5}),-1.0]])]});}
            var Q2;
            {var subQ1=sQuery(id+"F0.wireOp",EDGE,"E21.1.0");Q2=makeQuery(id+"F0.imprint","IMPRINT",FACE,{"disambiguationData":[TD([[makeQuery(id+"F0.imprint","IMPRINT",EDGE,{"derivedFrom":subQ1}),-1.0]])]});}
            var Q3;
            {var subQ0=sQuery(id+"F0.wireOp",EDGE,"E18.bottom");Q3=makeQuery(id+"F0.imprint","IMPRINT",FACE,{"disambiguationData":[TD([[makeQuery(id+"F0.imprint","IMPRINT",EDGE,{"derivedFrom":subQ0}),-1.0]])]});}
            var Q4;
            {var subQ0=sQuery(id+"F0.wireOp",EDGE,"E23");var subQ1=sQuery(id+"F0.wireOp",EDGE,"E18.left");var subQ2=makeQuery(id+"F0.imprint","INTERSECT",VERTEX,{"derivedFrom":[subQ1,subQ0]});Q4=makeQuery(id+"F0.imprint","IMPRINT",FACE,{"disambiguationData":[TD([[makeQuery(id+"F0.imprint","IMPRINT",EDGE,{"disambiguationData":[TD([[subQ2,-1.0]])],"derivedFrom":subQ1}),-1.0]])]});}
            var Q5;
            {var subQ0=sQuery(id+"F0.wireOp",EDGE,"E27.trimOffspring");var subQ1=sQuery(id+"F0.wireOp",EDGE,"E21.3.4");var subQ2=makeQuery(id+"F0.imprint","INTERSECT",VERTEX,{"derivedFrom":[subQ1,subQ0]});Q5=makeQuery(id+"F0.imprint","IMPRINT",FACE,{"disambiguationData":[TD([[makeQuery(id+"F0.imprint","IMPRINT",EDGE,{"disambiguationData":[TD([[subQ2,-1.0]])],"derivedFrom":subQ1}),1.0]])]});}
            var Q6;
            {var subQ0=sQuery(id+"F0.wireOp",EDGE,"E29.trimOffspring");var subQ1=sQuery(id+"F0.wireOp",EDGE,"E21.2.4");var subQ2=makeQuery(id+"F0.imprint","INTERSECT",VERTEX,{"derivedFrom":[subQ1,subQ0]});Q6=makeQuery(id+"F0.imprint","IMPRINT",FACE,{"disambiguationData":[TD([[makeQuery(id+"F0.imprint","IMPRINT",EDGE,{"disambiguationData":[TD([[subQ2,-1.0]])],"derivedFrom":subQ1}),1.0]])]});}
            var Q7;
            {var subQ0=sQuery(id+"F0.wireOp",EDGE,"E25.trimOffspring");var subQ1=sQuery(id+"F0.wireOp",EDGE,"E21.1.4");var subQ2=makeQuery(id+"F0.imprint","INTERSECT",VERTEX,{"derivedFrom":[subQ1,subQ0]});Q7=makeQuery(id+"F0.imprint","IMPRINT",FACE,{"disambiguationData":[TD([[makeQuery(id+"F0.imprint","IMPRINT",EDGE,{"disambiguationData":[TD([[subQ2,-1.0]])],"derivedFrom":subQ1}),1.0]])]});}
            var Q8;
            Q8=makeQuery(id+"F0.imprint","IMPRINT",FACE,{"disambiguationData":[TD([[makeQuery(id+"F0.imprint","IMPRINT",EDGE,{"derivedFrom":sQuery(id+"F0.wireOp",EDGE,"E22")}),1.0]])]});
            var Q9;
            {var subQ6=sQuery(id+"F0.wireOp",EDGE,"E21.2.2");Q9=makeQuery(id+"F0.imprint","IMPRINT",FACE,{"disambiguationData":[TD([[makeQuery(id+"F0.imprint","IMPRINT",EDGE,{"derivedFrom":subQ6}),-1.0]])]});}
            var Q10;
            {var subQ6=sQuery(id+"F0.wireOp",EDGE,"E21.3.2");Q10=makeQuery(id+"F0.imprint","IMPRINT",FACE,{"disambiguationData":[TD([[makeQuery(id+"F0.imprint","IMPRINT",EDGE,{"derivedFrom":subQ6}),-1.0]])]});}
            var Q11;
            {var subQ6=sQuery(id+"F0.wireOp",EDGE,"E21.4.2");Q11=makeQuery(id+"F0.imprint","IMPRINT",FACE,{"disambiguationData":[TD([[makeQuery(id+"F0.imprint","IMPRINT",EDGE,{"derivedFrom":subQ6}),-1.0]])]});}
            var Q12;
            {var subQ0=sQuery(id+"F0.wireOp",EDGE,"E25.trimOffspring");var subQ1=sQuery(id+"F0.wireOp",EDGE,"E21.2.1");var subQ2=makeQuery(id+"F0.imprint","INTERSECT",VERTEX,{"derivedFrom":[subQ1,subQ0]});Q12=makeQuery(id+"F0.imprint","IMPRINT",FACE,{"disambiguationData":[TD([[makeQuery(id+"F0.imprint","IMPRINT",EDGE,{"disambiguationData":[TD([[subQ2,-1.0]])],"derivedFrom":subQ1}),1.0]])]});}
            var Q13;
            {var subQ0=sQuery(id+"F0.wireOp",EDGE,"E29.trimOffspring");var subQ1=sQuery(id+"F0.wireOp",EDGE,"E21.2.3");var subQ2=makeQuery(id+"F0.imprint","INTERSECT",VERTEX,{"derivedFrom":[subQ1,subQ0]});Q13=makeQuery(id+"F0.imprint","IMPRINT",FACE,{"disambiguationData":[TD([[makeQuery(id+"F0.imprint","IMPRINT",EDGE,{"disambiguationData":[TD([[subQ2,1.0]])],"derivedFrom":subQ1}),-1.0]])]});}
            var Q14;
            {var subQ0=sQuery(id+"F0.wireOp",EDGE,"E27.trimOffspring");var subQ1=sQuery(id+"F0.wireOp",EDGE,"E21.3.3");var subQ2=makeQuery(id+"F0.imprint","INTERSECT",VERTEX,{"derivedFrom":[subQ1,subQ0]});Q14=makeQuery(id+"F0.imprint","IMPRINT",FACE,{"disambiguationData":[TD([[makeQuery(id+"F0.imprint","IMPRINT",EDGE,{"disambiguationData":[TD([[subQ2,1.0]])],"derivedFrom":subQ1}),-1.0]])]});}
            var Q15;
            {var subQ0=sQuery(id+"F0.wireOp",EDGE,"E29.trimOffspring");var subQ1=sQuery(id+"F0.wireOp",EDGE,"E21.3.1");var subQ2=makeQuery(id+"F0.imprint","INTERSECT",VERTEX,{"derivedFrom":[subQ1,subQ0]});Q15=makeQuery(id+"F0.imprint","IMPRINT",FACE,{"disambiguationData":[TD([[makeQuery(id+"F0.imprint","IMPRINT",EDGE,{"disambiguationData":[TD([[subQ2,-1.0]])],"derivedFrom":subQ1}),1.0]])]});}
            var Q16;
            {var subQ0=sQuery(id+"F0.wireOp",EDGE,"E27.trimOffspring");var subQ1=sQuery(id+"F0.wireOp",EDGE,"E21.4.1");var subQ2=makeQuery(id+"F0.imprint","INTERSECT",VERTEX,{"derivedFrom":[subQ1,subQ0]});Q16=makeQuery(id+"F0.imprint","IMPRINT",FACE,{"disambiguationData":[TD([[makeQuery(id+"F0.imprint","IMPRINT",EDGE,{"disambiguationData":[TD([[subQ2,-1.0]])],"derivedFrom":subQ1}),1.0]])]});}
            var Q17;
            {var subQ0=sQuery(id+"F0.wireOp",EDGE,"E23");var subQ1=sQuery(id+"F0.wireOp",EDGE,"E21.4.3");var subQ2=makeQuery(id+"F0.imprint","INTERSECT",VERTEX,{"derivedFrom":[subQ1,subQ0]});Q17=makeQuery(id+"F0.imprint","IMPRINT",FACE,{"disambiguationData":[TD([[makeQuery(id+"F0.imprint","IMPRINT",EDGE,{"disambiguationData":[TD([[subQ2,1.0]])],"derivedFrom":subQ1}),-1.0]])]});}
            var Q18;
            {var subQ0=sQuery(id+"F0.wireOp",EDGE,"E23");var subQ1=sQuery(id+"F0.wireOp",EDGE,"E16");var subQ2=makeQuery(id+"F0.imprint","INTERSECT",VERTEX,{"derivedFrom":[subQ1,subQ0]});Q18=makeQuery(id+"F0.imprint","IMPRINT",FACE,{"disambiguationData":[TD([[makeQuery(id+"F0.imprint","IMPRINT",EDGE,{"disambiguationData":[TD([[subQ2,-1.0]])],"derivedFrom":subQ1}),-1.0]])]});}
            var Q19;
            {var subQ1=sQuery(id+"F0.wireOp",EDGE,"E21.4.0");Q19=makeQuery(id+"F0.imprint","IMPRINT",FACE,{"disambiguationData":[TD([[makeQuery(id+"F0.imprint","IMPRINT",EDGE,{"derivedFrom":subQ1}),-1.0]])]});}
            var Q20;
            Q20=makeQuery(id+"F0.imprint","IMPRINT",FACE,{"disambiguationData":[TD([[makeQuery(id+"F0.imprint","IMPRINT",EDGE,{"derivedFrom":sQuery(id+"F0.wireOp",EDGE,"E3")}),1.0]])]});
            var Q21;
            {var subQ0=sQuery(id+"F0.wireOp",EDGE,"E25.trimOffspring");var subQ1=sQuery(id+"F0.wireOp",EDGE,"E21.1.3");var subQ2=makeQuery(id+"F0.imprint","INTERSECT",VERTEX,{"derivedFrom":[subQ1,subQ0]});Q21=makeQuery(id+"F0.imprint","IMPRINT",FACE,{"disambiguationData":[TD([[makeQuery(id+"F0.imprint","IMPRINT",EDGE,{"disambiguationData":[TD([[subQ2,1.0]])],"derivedFrom":subQ1}),-1.0]])]});}
            extrude(context, id + "F2", {"entities" : qUnion([Q0, Q1, Q2, Q3, Q4, Q5, Q6, Q7, Q8, Q9, Q10, Q11, Q12, Q13, Q14, Q15, Q16, Q17, Q18, Q19, Q20, Q21]), "endBound" : BoundingType.SYMMETRIC, "depth" : 1 / 101.6 * mm});
        }
        {
            var Q0;
            {var subQ35=sQuery(id+"F1.wireOp",EDGE,"E42");Q0=makeQuery(id+"F1.imprint","IMPRINT",FACE,{"disambiguationData":[TD([[makeQuery(id+"F1.imprint","IMPRINT",EDGE,{"derivedFrom":subQ35}),-1.0]])]});}
            var Q1;
            {var subQ6=sQuery(id+"F1.wireOp",EDGE,"E118");Q1=makeQuery(id+"F1.imprint","IMPRINT",FACE,{"disambiguationData":[TD([[makeQuery(id+"F1.imprint","IMPRINT",EDGE,{"derivedFrom":subQ6}),-1.0]])]});}
            var Q2;
            {var subQ16=sQuery(id+"F1.wireOp",EDGE,"E94");Q2=makeQuery(id+"F1.imprint","IMPRINT",FACE,{"disambiguationData":[TD([[makeQuery(id+"F1.imprint","IMPRINT",EDGE,{"derivedFrom":subQ16}),-1.0]])]});}
            var Q3;
            {var subQ10=sQuery(id+"F1.wireOp",EDGE,"E137");Q3=makeQuery(id+"F1.imprint","IMPRINT",FACE,{"disambiguationData":[TD([[makeQuery(id+"F1.imprint","IMPRINT",EDGE,{"derivedFrom":subQ10}),-1.0]])]});}
            var Q4;
            {var subQ16=sQuery(id+"F1.wireOp",EDGE,"E152");Q4=makeQuery(id+"F1.imprint","IMPRINT",FACE,{"disambiguationData":[TD([[makeQuery(id+"F1.imprint","IMPRINT",EDGE,{"derivedFrom":subQ16}),-1.0]])]});}
            var Q5;
            {var subQ0=sQuery(id+"F1.wireOp",EDGE,"E675.276");var subQ1=sQuery(id+"F1.wireOp",EDGE,"E148");var subQ2=makeQuery(id+"F1.imprint","INTERSECT",VERTEX,{"derivedFrom":[subQ1,subQ0]});Q5=makeQuery(id+"F1.imprint","IMPRINT",FACE,{"disambiguationData":[TD([[makeQuery(id+"F1.imprint","IMPRINT",EDGE,{"disambiguationData":[TD([[subQ2,-1.0]])],"derivedFrom":subQ1}),-1.0]])]});}
            extrude(context, id + "F3", {"entities" : qUnion([Q0, Q1, Q2, Q3, Q4, Q5]), "operationType" : NewBodyOperationType.ADD, "endBound" : BoundingType.SYMMETRIC, "depth" : 6.35 * mm});
        }
    });
